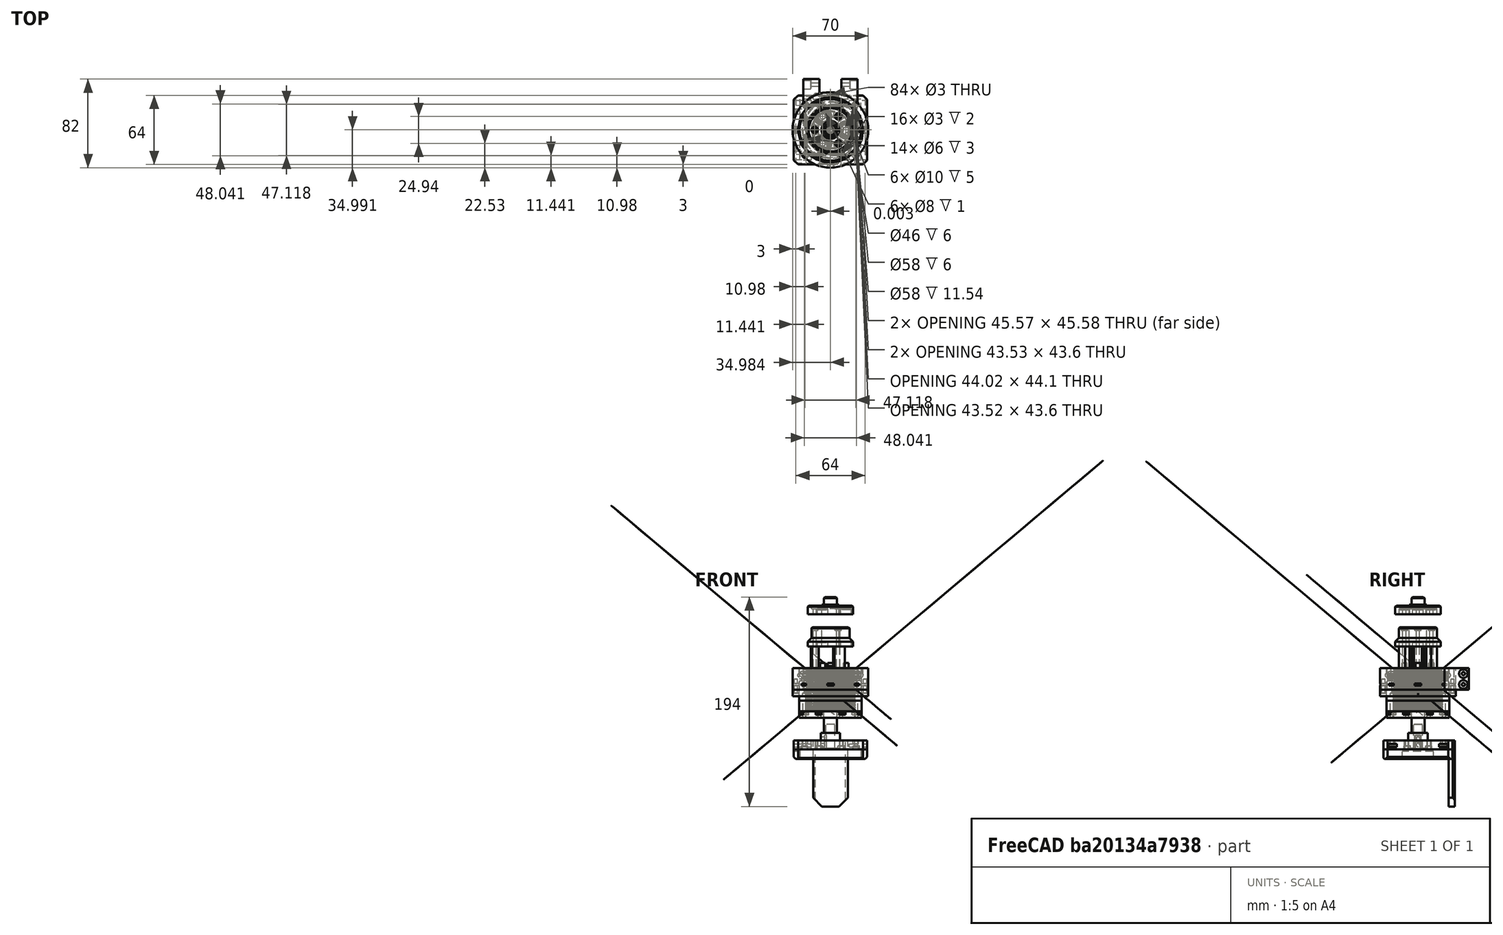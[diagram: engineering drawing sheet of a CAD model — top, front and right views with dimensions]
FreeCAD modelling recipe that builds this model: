
FCSTD DOCUMENT  (FreeCAD 0.19R24276 (Git))
Label: G-midi_gearbox_049
License: All rights reserved
LicenseURL: http://en.wikipedia.org/wiki/All_rights_reserved
objects: Part::Cylinder×393, Part::Cut×179, Part::Compound×131, Part::Box×129, Part::FeaturePython×71, Mesh::Feature×26, Part::Chamfer×22, Part::Torus×9
note: 934 computed .brp shape members not serialized (recipe doc carries the construction recipe); baked Part::Feature solids carry a one-line shape summary decoded from their .brp

FEATURE [Part::FeaturePython] wormgear031  # WARN: FeaturePython — macro-defined, semantics opaque (R4)
  AttacherType = Attacher::AttachEngine3D
  Placement = pos=(14.4,0,-10) rot=(0,0,1;0.991347rad)
  beta = 34.439
  clearance = 0.25
  diameter = 14
  head = 0.5
  height = 10
  module = 0.8
  pressure_angle = 20
  reverse_pitch = false
  teeth = 12
  version = 0.0.3
FEATURE [Part::FeaturePython] wormgear025  # WARN: FeaturePython — macro-defined, semantics opaque (R4)
  AttacherType = Attacher::AttachEngine3D
  Placement = pos=(14.4,0,0) rot=(0,0,1;0.977384rad)
  beta = 34.439
  clearance = 0.25
  diameter = 14
  head = 0.5
  height = 10
  module = 0.8
  pressure_angle = 20
  reverse_pitch = true
  teeth = 12
  version = 0.0.3
FEATURE [Part::FeaturePython] wormgear033  # WARN: FeaturePython — macro-defined, semantics opaque (R4)
  AttacherType = Attacher::AttachEngine3D
  Placement = pos=(14.4,0,10) rot=(0,0,1;0.977384rad)
  beta = 38.6598
  clearance = 0.25
  diameter = 12
  head = 0.5
  height = 10
  module = 0.8
  pressure_angle = 20
  reverse_pitch = false
  teeth = 12
  version = 0.0.3
FEATURE [Part::FeaturePython] wormgear032  # WARN: FeaturePython — macro-defined, semantics opaque (R4)
  AttacherType = Attacher::AttachEngine3D
  Placement = pos=(14.4,0,20) rot=(0,0,1;0.968658rad)
  beta = 38.6598
  clearance = 0.25
  diameter = 12
  head = 0.5
  height = 10
  module = 0.8
  pressure_angle = 20
  reverse_pitch = true
  teeth = 12
  version = 0.0.3
FEATURE [Part::Cylinder] Cylinder017  label="Válec017"
  Angle = 360
  AttacherType = Attacher::AttachEngine3D
  Height = 60
  Placement = pos=(14.4,0,-20) rot=(0,0,1;0rad)
  Radius = 2.65
FEATURE [Part::Cut] Cut317
  Base = -> wormgear031
  Tool = -> Cylinder017
FEATURE [Part::Cylinder] Cylinder025  label="Válec025"
  Angle = 360
  AttacherType = Attacher::AttachEngine3D
  Height = 5
  Placement = pos=(14.4,0,30) rot=(0,0,1;0rad)
  Radius = 2.45
FEATURE [Part::Cylinder] Cylinder016  label="Válec016"
  Angle = 360
  AttacherType = Attacher::AttachEngine3D
  Height = 60
  Placement = pos=(14.4,0,-20) rot=(0,0,1;0rad)
  Radius = 2.65
FEATURE [Part::Cut] Cut314
  Base = -> wormgear025
  Tool = -> Cylinder016
FEATURE [Part::Cylinder] Cylinder018  label="Válec018"
  Angle = 360
  AttacherType = Attacher::AttachEngine3D
  Height = 20
  Placement = pos=(14.4,0,-20) rot=(0,0,1;0rad)
  Radius = 2.65
FEATURE [Part::Cut] Cut316
  Base = -> wormgear032
  Tool = -> Cylinder018
FEATURE [Part::Cylinder] Cylinder019  label="Válec019"
  Angle = 360
  AttacherType = Attacher::AttachEngine3D
  Height = 60
  Placement = pos=(14.4,0,40) rot=(0,0,1;0rad)
  Radius = 2.65
FEATURE [Part::Cut] Cut313
  Base = -> wormgear033
  Tool = -> Cylinder019
FEATURE [Part::Compound] Compound539  label="gearovina_midi_vnejskove"
  Links = -> [Cylinder025,Cut313,Cut316,Cut314,Cut317]
FEATURE [Part::FeaturePython] cycloidgear  # WARN: FeaturePython — macro-defined, semantics opaque (R4)
  AttacherType = Attacher::AttachEngine3D
  Placement = pos=(0,0,10) rot=(0,0,1;0rad)
  backlash = 0
  beta = 50
  clearance = 0.25
  double_helix = true
  height = 20
  inner_diameter = 5
  module = 1
  numpoints = 15
  outer_diameter = 5
  teeth = 12
  version = 0.0.3
FEATURE [Part::FeaturePython] wormgear034  # WARN: FeaturePython — macro-defined, semantics opaque (R4)
  AttacherType = Attacher::AttachEngine3D
  Placement = pos=(0,0,10) rot=(0,0,1;0.977384rad)
  beta = 38.6598
  clearance = 0.25
  diameter = 12
  head = 0.5
  height = 10
  module = 0.8
  pressure_angle = 20
  reverse_pitch = false
  teeth = 12
  version = 0.0.3
FEATURE [Part::FeaturePython] cycloidgear001  # WARN: FeaturePython — macro-defined, semantics opaque (R4)
  AttacherType = Attacher::AttachEngine3D
  Placement = pos=(0,0,-10) rot=(0,0,1;0.331613rad)
  backlash = 0
  beta = 50
  clearance = 0.25
  double_helix = true
  height = 20
  inner_diameter = 5
  module = 1.2
  numpoints = 15
  outer_diameter = 5
  teeth = 12
  version = 0.0.3
FEATURE [Part::FeaturePython] wormgear035  # WARN: FeaturePython — macro-defined, semantics opaque (R4)
  AttacherType = Attacher::AttachEngine3D
  Placement = pos=(0,0,0) rot=(0,0,1;0.977384rad)
  beta = 34.439
  clearance = 0.25
  diameter = 14
  head = 0.5
  height = 10
  module = 0.8
  pressure_angle = 20
  reverse_pitch = true
  teeth = 12
  version = 0.0.3
FEATURE [Part::Cylinder] Cylinder026  label="Válec026"
  Angle = 360
  AttacherType = Attacher::AttachEngine3D
  Height = 5
  Placement = pos=(0,0,30) rot=(0,0,1;0rad)
  Radius = 2.45
FEATURE [Part::Cylinder] Cylinder027  label="Válec027"
  Angle = 360
  AttacherType = Attacher::AttachEngine3D
  Height = 60
  Placement = pos=(0,0,-20) rot=(0,0,1;0rad)
  Radius = 2.65
FEATURE [Part::Cylinder] Cylinder028  label="Válec028"
  Angle = 360
  AttacherType = Attacher::AttachEngine3D
  Height = 60
  Placement = pos=(0,0,-20) rot=(0,0,1;0rad)
  Radius = 2.65
FEATURE [Part::Cut] Cut
  Base = -> cycloidgear001
  Tool = -> Cylinder027
FEATURE [Part::Compound] Compound  label="G-midi_outer-gear"
  Links = -> [Cut,Cylinder026,cycloidgear]
FEATURE [Mesh::Feature] Mesh  label="G-midi_outer-gear (Meshed)"
FEATURE [Part::Torus] Torus006  label="Anuloid006"
  Angle1 = -180
  Angle2 = 180
  Angle3 = 360
  AttacherType = Attacher::AttachEngine3D
  Placement = pos=(0,0,22.5) rot=(0,0,1;0rad)
  Radius1 = 27.75
  Radius2 = 2.2
FEATURE [Part::Cylinder] Cylinder864  label="Válec864"
  Angle = 360
  AttacherType = Attacher::AttachEngine3D
  Height = 9
  Placement = pos=(0,0,11) rot=(0,0,1;0rad)
  Radius = 28.5
FEATURE [Part::Cylinder] Cylinder874  label="Válec874"
  Angle = 360
  AttacherType = Attacher::AttachEngine3D
  Height = 10
  Placement = pos=(0,0,20) rot=(0,0,1;0rad)
  Radius = 28.5
FEATURE [Part::Cylinder] Cylinder875  label="Válec875"
  Angle = 360
  AttacherType = Attacher::AttachEngine3D
  Height = 10
  Placement = pos=(28,0,23.5) rot=(0,0,1;0.392699rad)
  Radius = 2.2
FEATURE [Part::Box] Box332  label="Krychle332"
  AttacherType = Attacher::AttachEngine3D
  Height = 2
  Length = 6
  Placement = pos=(-11.1907,19.1773,25) rot=(0,0,1;0.392699rad)
  Width = 7
FEATURE [Part::Box] Box333  label="Krychle333"
  AttacherType = Attacher::AttachEngine3D
  Height = 2
  Length = 6
  Placement = pos=(-21.4734,5.6474,25) rot=(0,0,1;1.1781rad)
  Width = 7
FEATURE [Part::FeaturePython] wormgear046  # WARN: FeaturePython — macro-defined, semantics opaque (R4)
  AttacherType = Attacher::AttachEngine3D
  Placement = pos=(0,0,9) rot=(0,0,1;1.17286rad)
  beta = 29.1676
  clearance = 0.25
  diameter = 43
  head = 0
  height = 12
  module = 0.8
  pressure_angle = 20
  reverse_pitch = false
  teeth = 30
  version = 0.0.3
FEATURE [Part::Cut] Cut352
  Base = -> Cylinder864
  Tool = -> wormgear046
FEATURE [Part::FeaturePython] wormgear049  # WARN: FeaturePython — macro-defined, semantics opaque (R4)
  AttacherType = Attacher::AttachEngine3D
  Placement = pos=(0,0,19) rot=(0,0,1;1.1205rad)
  beta = 29.1676
  clearance = 0.25
  diameter = 43
  head = 0
  height = 12
  module = 0.8
  pressure_angle = 20
  reverse_pitch = true
  teeth = 30
  version = 0.0.3
FEATURE [Part::Cut] Cut362
  Base = -> Cylinder874
  Tool = -> wormgear049
FEATURE [Part::Cut] Cut361
  Base = -> Cut362
  Tool = -> Torus006
FEATURE [Part::Cut] Cut360
  Base = -> Cut361
  Tool = -> Cylinder875
FEATURE [Part::Box] Box335  label="Krychle335"
  AttacherType = Attacher::AttachEngine3D
  Height = 2
  Length = 6
  Placement = pos=(-5.6474,-21.4734,25) rot=(0,0,1;2.74889rad)
  Width = 7
FEATURE [Part::Box] Box339  label="Krychle339"
  AttacherType = Attacher::AttachEngine3D
  Height = 2
  Length = 6
  Placement = pos=(5.6474,21.4734,25) rot=(0,0,-1;0.392699rad)
  Width = 7
FEATURE [Part::Cylinder] Cylinder883  label="Válec883"
  Angle = 360
  AttacherType = Attacher::AttachEngine3D
  Height = 10
  Placement = pos=(23.5589,9.75843,25) rot=(0,0,-1;1.1781rad)
  Radius = 1.5
FEATURE [Part::Cylinder] Cylinder878  label="Válec878"
  Angle = 360
  AttacherType = Attacher::AttachEngine3D
  Height = 10
  Placement = pos=(-23.5589,-9.75843,25) rot=(0,0,1;1.96349rad)
  Radius = 1.5
FEATURE [Part::Cylinder] Cylinder879  label="Válec879"
  Angle = 360
  AttacherType = Attacher::AttachEngine3D
  Height = 10
  Placement = pos=(9.75843,-23.5589,25) rot=(0,0,1;3.53429rad)
  Radius = 1.5
FEATURE [Part::Cylinder] Cylinder880  label="Válec880"
  Angle = 360
  AttacherType = Attacher::AttachEngine3D
  Height = 10
  Placement = pos=(9.75843,23.5589,25) rot=(0,0,-1;0.392699rad)
  Radius = 1.5
FEATURE [Part::Cylinder] Cylinder877  label="Válec877"
  Angle = 360
  AttacherType = Attacher::AttachEngine3D
  Height = 10
  Placement = pos=(-9.75843,23.5589,25) rot=(0,0,1;0.392699rad)
  Radius = 1.5
FEATURE [Part::Cylinder] Cylinder881  label="Válec881"
  Angle = 360
  AttacherType = Attacher::AttachEngine3D
  Height = 10
  Placement = pos=(23.5589,-9.75843,25) rot=(0,0,-1;1.96349rad)
  Radius = 1.5
FEATURE [Part::Box] Box334  label="Krychle334"
  AttacherType = Attacher::AttachEngine3D
  Height = 2
  Length = 6
  Placement = pos=(-19.1773,-11.1907,25) rot=(0,0,1;1.96349rad)
  Width = 7
FEATURE [Part::Cylinder] Cylinder882  label="Válec882"
  Angle = 360
  AttacherType = Attacher::AttachEngine3D
  Height = 10
  Placement = pos=(-9.75843,-23.5589,25) rot=(0,0,1;2.74889rad)
  Radius = 1.5
FEATURE [Part::Box] Box338  label="Krychle338"
  AttacherType = Attacher::AttachEngine3D
  Height = 2
  Length = 6
  Placement = pos=(19.1773,11.1907,25) rot=(0,0,-1;1.1781rad)
  Width = 7
FEATURE [Part::Box] Box337  label="Krychle337"
  AttacherType = Attacher::AttachEngine3D
  Height = 2
  Length = 6
  Placement = pos=(21.4734,-5.6474,25) rot=(0,0,-1;1.96349rad)
  Width = 7
FEATURE [Part::Box] Box336  label="Krychle336"
  AttacherType = Attacher::AttachEngine3D
  Height = 2
  Length = 6
  Placement = pos=(11.1907,-19.1773,25) rot=(0,0,1;3.53429rad)
  Width = 7
FEATURE [Part::Compound] Compound561
  Links = -> [Box332,Box333,Box334,Box335,Box336,Box337,Box338,Box339]
FEATURE [Part::Cut] Cut363
  Base = -> Cut360
  Tool = -> Compound561
FEATURE [Part::Cylinder] Cylinder876  label="Válec876"
  Angle = 360
  AttacherType = Attacher::AttachEngine3D
  Height = 10
  Placement = pos=(-23.5589,9.75843,25) rot=(0,0,1;1.1781rad)
  Radius = 1.5
FEATURE [Part::Compound] Compound562
  Links = -> [Cylinder877,Cylinder876,Cylinder878,Cylinder882,Cylinder879,Cylinder881,Cylinder883,Cylinder880]
FEATURE [Part::Cut] Cut364
  Base = -> Cut363
  Tool = -> Compound562
FEATURE [Part::Compound] Compound563  label="gearovina_midi_rybovina"
  Links = -> [Cut364,Cut352]
FEATURE [Part::FeaturePython] wormgear050  # WARN: FeaturePython — macro-defined, semantics opaque (R4)
  AttacherType = Attacher::AttachEngine3D
  Placement = pos=(0,0,19) rot=(0,0,1;1.1205rad)
  beta = 29.1676
  clearance = 0.25
  diameter = 43
  head = 0
  height = 12
  module = 0.8
  pressure_angle = 20
  reverse_pitch = true
  teeth = 30
  version = 0.0.3
FEATURE [Part::FeaturePython] cycloidgear002  # WARN: FeaturePython — macro-defined, semantics opaque (R4)
  AttacherType = Attacher::AttachEngine3D
  Placement = pos=(0,0,-1) rot=(0,0,1;0rad)
  backlash = 0
  beta = 50
  clearance = 0.25
  double_helix = true
  height = 22
  inner_diameter = 5
  module = 1.35
  numpoints = 15
  outer_diameter = 5
  teeth = 33
  version = 0.0.3
FEATURE [Part::Cylinder] Cylinder884  label="Válec884"
  Angle = 360
  AttacherType = Attacher::AttachEngine3D
  Height = 20
  Radius = 29
FEATURE [Part::Cut] Cut365  label="G-midi_exp-ring-cyclo"
  Base = -> Cylinder884
  Tool = -> cycloidgear002
FEATURE [Part::FeaturePython] cycloidgear003  # WARN: FeaturePython — macro-defined, semantics opaque (R4)
  AttacherType = Attacher::AttachEngine3D
  Placement = pos=(0,0,10) rot=(0,0,1;0.418879rad)
  backlash = 0
  beta = 50
  clearance = 0
  double_helix = true
  height = 20
  inner_diameter = 3
  module = 1.25
  numpoints = 15
  outer_diameter = 5
  teeth = 9
  version = 0.0.3
FEATURE [Part::FeaturePython] cycloidgear004  # WARN: FeaturePython — macro-defined, semantics opaque (R4)
  AttacherType = Attacher::AttachEngine3D
  Placement = pos=(0,0,-10) rot=(0,0,-1;0.453786rad)
  backlash = 0
  beta = 50
  clearance = 0.25
  double_helix = true
  height = 20
  inner_diameter = 5
  module = 1.32
  numpoints = 15
  outer_diameter = 5
  teeth = 12
  version = 0.0.3
FEATURE [Part::Cylinder] Cylinder885  label="Válec885"
  Angle = 360
  AttacherType = Attacher::AttachEngine3D
  Height = 60
  Placement = pos=(0,0,-20) rot=(0,0,1;0rad)
  Radius = 2.65
FEATURE [Part::Cut] Cut366
  Base = -> cycloidgear004
  Tool = -> Cylinder885
FEATURE [Part::Cylinder] Cylinder886  label="Válec886"
  Angle = 360
  AttacherType = Attacher::AttachEngine3D
  Height = 5
  Placement = pos=(0,0,30) rot=(0,0,1;0rad)
  Radius = 2.45
FEATURE [Part::Compound] Compound564  label="G-midi_outer-gear001-cyclo"
  Links = -> [Cut366,Cylinder886,cycloidgear003]
  Placement = pos=(-14,0,10) rot=(0,0,-1;0.331613rad)
FEATURE [Part::Cylinder] Cylinder887  label="Válec887"
  Angle = 360
  AttacherType = Attacher::AttachEngine3D
  Height = 20
  Radius = 26
FEATURE [Part::FeaturePython] involutegear  # WARN: FeaturePython — macro-defined, semantics opaque (R4)
  AttacherType = Attacher::AttachEngine3D
  Placement = pos=(0,0,-1) rot=(0,0,1;0rad)
  backlash = 0
  beta = 50
  clearance = 0.25
  da = 45.6
  df = 40.2
  double_helix = true
  dw = 43.2
  head = 0
  height = 22
  module = 1.2
  numpoints = 6
  pressure_angle = 20
  properties_from_tool = false
  reversed_backlash = false
  shift = 0
  simple = false
  teeth = 36
  transverse_pitch = 3.76991
  undercut = false
  version = 0.0.3
FEATURE [Part::Cut] Cut367  label="G-midi_exp-ring-invo"
  Base = -> Cylinder887
  Tool = -> involutegear
FEATURE [Part::Cylinder] Cylinder119  label="Válec119"
  Angle = 360
  AttacherType = Attacher::AttachEngine3D
  Height = 3
  Placement = pos=(0,32,4) rot=(0,0,1;0rad)
  Radius = 3
FEATURE [Part::Cylinder] Cylinder109  label="Válec109"
  Angle = 360
  AttacherType = Attacher::AttachEngine3D
  Height = 10
  Radius = 29
FEATURE [Part::Cylinder] Cylinder120  label="Válec120"
  Angle = 360
  AttacherType = Attacher::AttachEngine3D
  Height = 3
  Placement = pos=(-22.6274,22.6274,4) rot=(0,0,1;0.785398rad)
  Radius = 3
FEATURE [Part::Cylinder] Cylinder110  label="Válec110"
  Angle = 360
  AttacherType = Attacher::AttachEngine3D
  Height = 10
  Radius = 29
FEATURE [Part::Cylinder] Cylinder121  label="Válec121"
  Angle = 360
  AttacherType = Attacher::AttachEngine3D
  Height = 3
  Placement = pos=(-32,0,4) rot=(0,0,1;1.5708rad)
  Radius = 3
FEATURE [Part::FeaturePython] wormgear041  # WARN: FeaturePython — macro-defined, semantics opaque (R4)
  AttacherType = Attacher::AttachEngine3D
  Placement = pos=(0,0,0) rot=(0,0,1;1.13796rad)
  beta = 30.9638
  clearance = 0.25
  diameter = 44
  head = 0
  height = 12
  module = 0.8
  pressure_angle = 20
  reverse_pitch = false
  teeth = 33
  version = 0.0.3
FEATURE [Part::Cut] Cut038
  Base = -> Cylinder110
  Placement = pos=(0,0,-10) rot=(0,0,1;0rad)
  Tool = -> wormgear041
FEATURE [Part::FeaturePython] wormgear042  # WARN: FeaturePython — macro-defined, semantics opaque (R4)
  AttacherType = Attacher::AttachEngine3D
  Placement = pos=(0,0,0) rot=(0,0,1;1.13446rad)
  beta = 30.9638
  clearance = 0.25
  diameter = 44
  head = 0
  height = 12
  module = 0.8
  pressure_angle = 20
  reverse_pitch = true
  teeth = 33
  version = 0.0.3
FEATURE [Part::Cut] Cut039
  Base = -> Cylinder109
  Tool = -> wormgear042
FEATURE [Part::Compound] Compound038  label="superokruh"
  Links = -> [Cut038,Cut039]
FEATURE [Part::FeaturePython] Tube008  # WARN: FeaturePython — macro-defined, semantics opaque (R4)
  AttacherType = Attacher::AttachEngine3D
  Height = 6
  InnerRadius = 29
  OuterRadius = 35
  Placement = pos=(0,0,4) rot=(0,0,1;0rad)
FEATURE [Part::Cylinder] Cylinder131  label="Válec131"
  Angle = 360
  AttacherType = Attacher::AttachEngine3D
  Height = 15
  Placement = pos=(1e-14,-32,0) rot=(0,0,1;3.14159rad)
  Radius = 1.5
FEATURE [Part::Cylinder] Cylinder123  label="Válec123"
  Angle = 360
  AttacherType = Attacher::AttachEngine3D
  Height = 3
  Placement = pos=(1e-14,-32,4) rot=(0,0,1;3.14159rad)
  Radius = 3
FEATURE [Part::Cylinder] Cylinder122  label="Válec122"
  Angle = 360
  AttacherType = Attacher::AttachEngine3D
  Height = 3
  Placement = pos=(-22.6274,-22.6274,4) rot=(0,0,1;2.35619rad)
  Radius = 3
FEATURE [Part::Cylinder] Cylinder132  label="Válec132"
  Angle = 360
  AttacherType = Attacher::AttachEngine3D
  Height = 15
  Placement = pos=(22.6274,-22.6274,0) rot=(0,0,1;3.92699rad)
  Radius = 1.5
FEATURE [Part::Cylinder] Cylinder129  label="Válec129"
  Angle = 360
  AttacherType = Attacher::AttachEngine3D
  Height = 15
  Placement = pos=(-32,0,0) rot=(0,0,1;1.5708rad)
  Radius = 1.5
FEATURE [Part::Cylinder] Cylinder127  label="Válec127"
  Angle = 360
  AttacherType = Attacher::AttachEngine3D
  Height = 15
  Placement = pos=(0,32,0) rot=(0,0,1;0rad)
  Radius = 1.5
FEATURE [Part::Cylinder] Cylinder124  label="Válec124"
  Angle = 360
  AttacherType = Attacher::AttachEngine3D
  Height = 3
  Placement = pos=(22.6274,-22.6274,4) rot=(0,0,1;3.92699rad)
  Radius = 3
FEATURE [Part::Cylinder] Cylinder133  label="Válec133"
  Angle = 360
  AttacherType = Attacher::AttachEngine3D
  Height = 15
  Placement = pos=(32,1.1e-14,0) rot=(0,0,-1;1.5708rad)
  Radius = 1.5
FEATURE [Part::Cylinder] Cylinder126  label="Válec126"
  Angle = 360
  AttacherType = Attacher::AttachEngine3D
  Height = 3
  Placement = pos=(22.6274,22.6274,4) rot=(0,0,-1;0.785398rad)
  Radius = 3
FEATURE [Part::Cylinder] Cylinder125  label="Válec125"
  Angle = 360
  AttacherType = Attacher::AttachEngine3D
  Height = 3
  Placement = pos=(32,1.1e-14,4) rot=(0,0,-1;1.5708rad)
  Radius = 3
FEATURE [Part::Compound] Compound040
  Links = -> [Cylinder119,Cylinder120,Cylinder121,Cylinder122,Cylinder123,Cylinder124,Cylinder125,Cylinder126]
FEATURE [Part::Cut] Cut041
  Base = -> Tube008
  Tool = -> Compound040
FEATURE [Part::Cylinder] Cylinder134  label="Válec134"
  Angle = 360
  AttacherType = Attacher::AttachEngine3D
  Height = 15
  Placement = pos=(22.6274,22.6274,0) rot=(0,0,-1;0.785398rad)
  Radius = 1.5
FEATURE [Part::Cylinder] Cylinder128  label="Válec128"
  Angle = 360
  AttacherType = Attacher::AttachEngine3D
  Height = 15
  Placement = pos=(-22.6274,22.6274,0) rot=(0,0,1;0.785398rad)
  Radius = 1.5
FEATURE [Part::Cylinder] Cylinder130  label="Válec130"
  Angle = 360
  AttacherType = Attacher::AttachEngine3D
  Height = 15
  Placement = pos=(-22.6274,-22.6274,0) rot=(0,0,1;2.35619rad)
  Radius = 1.5
FEATURE [Part::Compound] Compound041
  Links = -> [Cylinder127,Cylinder128,Cylinder129,Cylinder130,Cylinder131,Cylinder132,Cylinder133,Cylinder134]
FEATURE [Part::Cut] Cut042
  Base = -> Cut041
  Tool = -> Compound041
FEATURE [Part::Cylinder] Cylinder139  label="Válec139"
  Angle = 360
  AttacherType = Attacher::AttachEngine3D
  Height = 20
  Placement = pos=(-24,38,-11) rot=(0,1,0;1.5708rad)
  Radius = 1.5
FEATURE [Part::Cylinder] Cylinder141  label="Válec141"
  Angle = 360
  AttacherType = Attacher::AttachEngine3D
  Height = 20
  Placement = pos=(-34,38,-11) rot=(0,1,0;1.5708rad)
  Radius = 4
FEATURE [Part::Cylinder] Cylinder142  label="Válec142"
  Angle = 360
  AttacherType = Attacher::AttachEngine3D
  Height = 20
  Placement = pos=(4,38,5) rot=(0,1,0;1.5708rad)
  Radius = 1.5
FEATURE [Part::Cylinder] Cylinder144  label="Válec144"
  Angle = 360
  AttacherType = Attacher::AttachEngine3D
  Height = 20
  Placement = pos=(14,38,5) rot=(0,1,0;1.5708rad)
  Radius = 4
FEATURE [Part::Cylinder] Cylinder145  label="Válec145"
  Angle = 360
  AttacherType = Attacher::AttachEngine3D
  Height = 20
  Placement = pos=(14,38,-11) rot=(0,1,0;1.5708rad)
  Radius = 4
FEATURE [Part::Compound] Compound044
  Links = -> [Cylinder144,Cylinder145]
FEATURE [Part::Box] Box057  label="Krychle057"
  AttacherType = Attacher::AttachEngine3D
  Height = 26
  Length = 16
  Placement = pos=(-8,20,-16) rot=(0,0,1;0rad)
  Width = 25
FEATURE [Part::Cylinder] Cylinder138  label="Válec138"
  Angle = 360
  AttacherType = Attacher::AttachEngine3D
  Height = 20
  Placement = pos=(-24,38,5) rot=(0,1,0;1.5708rad)
  Radius = 1.5
FEATURE [Part::Compound] Compound043
  Links = -> [Cylinder138,Cylinder139]
FEATURE [Part::Box] Box055  label="Krychle055"
  AttacherType = Attacher::AttachEngine3D
  Height = 26
  Length = 40
  Placement = pos=(-20,15,-16) rot=(0,0,1;0rad)
  Width = 30
FEATURE [Part::Cylinder] Cylinder140  label="Válec140"
  Angle = 360
  AttacherType = Attacher::AttachEngine3D
  Height = 20
  Placement = pos=(-34,38,5) rot=(0,1,0;1.5708rad)
  Radius = 4
FEATURE [Part::Compound] Compound042
  Links = -> [Cylinder140,Cylinder141]
FEATURE [Part::Cylinder] Cylinder143  label="Válec143"
  Angle = 360
  AttacherType = Attacher::AttachEngine3D
  Height = 20
  Placement = pos=(4,38,-11) rot=(0,1,0;1.5708rad)
  Radius = 1.5
FEATURE [Part::Compound] Compound045
  Links = -> [Cylinder142,Cylinder143]
FEATURE [Part::Cylinder] Cylinder136  label="Válec136"
  Angle = 360
  AttacherType = Attacher::AttachEngine3D
  Height = 26
  Placement = pos=(0,0,-16) rot=(0,0,1;0rad)
  Radius = 29
FEATURE [Part::Cut] Cut045
  Base = -> Box055
  Tool = -> Cylinder136
FEATURE [Part::Cut] Cut047
  Base = -> Cut045
  Tool = -> Box057
FEATURE [Part::Cut] Cut048
  Base = -> Cut047
  Tool = -> Compound042
FEATURE [Part::Cut] Cut049
  Base = -> Cut048
  Tool = -> Compound043
FEATURE [Part::Cut] Cut050
  Base = -> Cut049
  Tool = -> Compound044
FEATURE [Part::Cut] Cut051
  Base = -> Cut050
  Tool = -> Compound045
FEATURE [Part::Compound] Compound046  label="gearovina_midi_superokruh1"
  Links = -> [Cut051,Cut042,Compound038]
FEATURE [Part::Cylinder] Cylinder111  label="Válec111"
  Angle = 360
  AttacherType = Attacher::AttachEngine3D
  Height = 15
  Placement = pos=(0,26,-20) rot=(0,0,1;0rad)
  Radius = 1.5
FEATURE [Part::Cylinder] Cylinder112  label="Válec112"
  Angle = 360
  AttacherType = Attacher::AttachEngine3D
  Height = 15
  Placement = pos=(-18.3848,18.3848,-20) rot=(0,0,1;0.785398rad)
  Radius = 1.5
FEATURE [Part::FeaturePython] Tube007  # WARN: FeaturePython — macro-defined, semantics opaque (R4)
  AttacherType = Attacher::AttachEngine3D
  Height = 6
  InnerRadius = 23
  OuterRadius = 29
  Placement = pos=(0,0,-16) rot=(0,0,1;0rad)
FEATURE [Part::Box] Box047  label="Krychle047"
  AttacherType = Attacher::AttachEngine3D
  Height = 2
  Length = 6
  Placement = pos=(-3,23,-13) rot=(0,0,1;0rad)
  Width = 6
FEATURE [Part::Cylinder] Cylinder114  label="Válec114"
  Angle = 360
  AttacherType = Attacher::AttachEngine3D
  Height = 15
  Placement = pos=(-18.3848,-18.3848,-20) rot=(0,0,1;2.35619rad)
  Radius = 1.5
FEATURE [Part::Cylinder] Cylinder113  label="Válec113"
  Angle = 360
  AttacherType = Attacher::AttachEngine3D
  Height = 15
  Placement = pos=(-26,-4e-15,-20) rot=(0,0,1;1.5708rad)
  Radius = 1.5
FEATURE [Part::Cylinder] Cylinder115  label="Válec115"
  Angle = 360
  AttacherType = Attacher::AttachEngine3D
  Height = 15
  Placement = pos=(1.1e-14,-26,-20) rot=(0,0,1;3.14159rad)
  Radius = 1.5
FEATURE [Part::Cylinder] Cylinder116  label="Válec116"
  Angle = 360
  AttacherType = Attacher::AttachEngine3D
  Height = 15
  Placement = pos=(18.3848,-18.3848,-20) rot=(0,0,1;3.92699rad)
  Radius = 1.5
FEATURE [Part::Cylinder] Cylinder118  label="Válec118"
  Angle = 360
  AttacherType = Attacher::AttachEngine3D
  Height = 15
  Placement = pos=(18.3848,18.3848,-20) rot=(0,0,-1;0.785398rad)
  Radius = 1.5
FEATURE [Part::Cylinder] Cylinder117  label="Válec117"
  Angle = 360
  AttacherType = Attacher::AttachEngine3D
  Height = 15
  Placement = pos=(26,1e-14,-20) rot=(0,0,-1;1.5708rad)
  Radius = 1.5
FEATURE [Part::Compound] Compound565
  Links = -> [Cylinder111,Cylinder112,Cylinder113,Cylinder114,Cylinder115,Cylinder116,Cylinder117,Cylinder118]
  Placement = pos=(0,0,0) rot=(0,0,1;0.392699rad)
FEATURE [Part::Cut] Cut368
  Base = -> Tube007
  Tool = -> Compound565
FEATURE [Part::Box] Box048  label="Krychle048"
  AttacherType = Attacher::AttachEngine3D
  Height = 2
  Length = 6
  Placement = pos=(-18.3848,14.1421,-13) rot=(0,0,1;0.785398rad)
  Width = 6
FEATURE [Part::Box] Box050  label="Krychle050"
  AttacherType = Attacher::AttachEngine3D
  Height = 2
  Length = 6
  Placement = pos=(-14.1421,-18.3848,-13) rot=(0,0,1;2.35619rad)
  Width = 6
FEATURE [Part::Box] Box052  label="Krychle052"
  AttacherType = Attacher::AttachEngine3D
  Height = 2
  Length = 6
  Placement = pos=(18.3848,-14.1421,-13) rot=(0,0,1;3.92699rad)
  Width = 6
FEATURE [Part::Box] Box054  label="Krychle054"
  AttacherType = Attacher::AttachEngine3D
  Height = 2
  Length = 6
  Placement = pos=(14.1421,18.3848,-13) rot=(0,0,-1;0.785398rad)
  Width = 6
FEATURE [Part::Box] Box049  label="Krychle049"
  AttacherType = Attacher::AttachEngine3D
  Height = 2
  Length = 6
  Placement = pos=(-23,-3,-13) rot=(0,0,1;1.5708rad)
  Width = 6
FEATURE [Part::Box] Box051  label="Krychle051"
  AttacherType = Attacher::AttachEngine3D
  Height = 2
  Length = 6
  Placement = pos=(3,-23,-13) rot=(0,0,1;3.14159rad)
  Width = 6
FEATURE [Part::Box] Box053  label="Krychle053"
  AttacherType = Attacher::AttachEngine3D
  Height = 2
  Length = 6
  Placement = pos=(23,3,-13) rot=(0,0,-1;1.5708rad)
  Width = 6
FEATURE [Part::Compound] Compound039
  Links = -> [Box048,Box049,Box050,Box051,Box052,Box053,Box054,Box047]
  Placement = pos=(0,0,0) rot=(0,0,1;0.392699rad)
FEATURE [Part::Cut] Cut311
  Base = -> Cut368
  Tool = -> Compound039
FEATURE [Part::Compound] Compound538  label="gearovina_midi_superokruh"
  Links = -> [Compound046,Cut311]
FEATURE [Part::Cylinder] Cylinder889  label="Válec889"
  Angle = 360
  AttacherType = Attacher::AttachEngine3D
  Height = 15
  Placement = pos=(1e-14,-32,0) rot=(0,0,1;3.14159rad)
  Radius = 1.5
FEATURE [Part::Cylinder] Cylinder890  label="Válec890"
  Angle = 360
  AttacherType = Attacher::AttachEngine3D
  Height = 15
  Placement = pos=(22.6274,-22.6274,0) rot=(0,0,1;3.92699rad)
  Radius = 1.5
FEATURE [Part::Cylinder] Cylinder891  label="Válec891"
  Angle = 360
  AttacherType = Attacher::AttachEngine3D
  Height = 3
  Placement = pos=(-22.6274,-22.6274,4) rot=(0,0,1;2.35619rad)
  Radius = 3
FEATURE [Part::Cylinder] Cylinder892  label="Válec892"
  Angle = 360
  AttacherType = Attacher::AttachEngine3D
  Height = 15
  Placement = pos=(0,32,0) rot=(0,0,1;0rad)
  Radius = 1.5
FEATURE [Part::Cylinder] Cylinder893  label="Válec893"
  Angle = 360
  AttacherType = Attacher::AttachEngine3D
  Height = 3
  Placement = pos=(0,32,4) rot=(0,0,1;0rad)
  Radius = 3
FEATURE [Part::Cylinder] Cylinder894  label="Válec894"
  Angle = 360
  AttacherType = Attacher::AttachEngine3D
  Height = 3
  Placement = pos=(-22.6274,22.6274,4) rot=(0,0,1;0.785398rad)
  Radius = 3
FEATURE [Part::Cylinder] Cylinder895  label="Válec895"
  Angle = 360
  AttacherType = Attacher::AttachEngine3D
  Height = 3
  Placement = pos=(-32,0,4) rot=(0,0,1;1.5708rad)
  Radius = 3
FEATURE [Part::Cylinder] Cylinder896  label="Válec896"
  Angle = 360
  AttacherType = Attacher::AttachEngine3D
  Height = 3
  Placement = pos=(1e-14,-32,4) rot=(0,0,1;3.14159rad)
  Radius = 3
FEATURE [Part::Cylinder] Cylinder897  label="Válec897"
  Angle = 360
  AttacherType = Attacher::AttachEngine3D
  Height = 15
  Placement = pos=(-32,0,0) rot=(0,0,1;1.5708rad)
  Radius = 1.5
FEATURE [Part::Cylinder] Cylinder898  label="Válec898"
  Angle = 360
  AttacherType = Attacher::AttachEngine3D
  Height = 3
  Placement = pos=(22.6274,-22.6274,4) rot=(0,0,1;3.92699rad)
  Radius = 3
FEATURE [Part::Cylinder] Cylinder899  label="Válec899"
  Angle = 360
  AttacherType = Attacher::AttachEngine3D
  Height = 3
  Placement = pos=(22.6274,22.6274,4) rot=(0,0,-1;0.785398rad)
  Radius = 3
FEATURE [Part::Cylinder] Cylinder900  label="Válec900"
  Angle = 360
  AttacherType = Attacher::AttachEngine3D
  Height = 15
  Placement = pos=(-22.6274,22.6274,0) rot=(0,0,1;0.785398rad)
  Radius = 1.5
FEATURE [Part::Cylinder] Cylinder901  label="Válec901"
  Angle = 360
  AttacherType = Attacher::AttachEngine3D
  Height = 15
  Placement = pos=(22.6274,22.6274,0) rot=(0,0,-1;0.785398rad)
  Radius = 1.5
FEATURE [Part::Cylinder] Cylinder902  label="Válec902"
  Angle = 360
  AttacherType = Attacher::AttachEngine3D
  Height = 15
  Placement = pos=(32,1.1e-14,0) rot=(0,0,-1;1.5708rad)
  Radius = 1.5
FEATURE [Part::Cylinder] Cylinder903  label="Válec903"
  Angle = 360
  AttacherType = Attacher::AttachEngine3D
  Height = 3
  Placement = pos=(32,1.1e-14,4) rot=(0,0,-1;1.5708rad)
  Radius = 3
FEATURE [Part::Cylinder] Cylinder904  label="Válec904"
  Angle = 360
  AttacherType = Attacher::AttachEngine3D
  Height = 15
  Placement = pos=(-22.6274,-22.6274,0) rot=(0,0,1;2.35619rad)
  Radius = 1.5
FEATURE [Part::FeaturePython] Tube009  # WARN: FeaturePython — macro-defined, semantics opaque (R4)
  AttacherType = Attacher::AttachEngine3D
  Height = 6
  InnerRadius = 29
  OuterRadius = 35
  Placement = pos=(0,0,4) rot=(0,0,1;0rad)
FEATURE [Part::Compound] Compound566
  Links = -> [Cylinder893,Cylinder894,Cylinder895,Cylinder891,Cylinder896,Cylinder898,Cylinder903,Cylinder899]
FEATURE [Part::Compound] Compound567
  Links = -> [Cylinder892,Cylinder900,Cylinder897,Cylinder904,Cylinder889,Cylinder890,Cylinder902,Cylinder901]
FEATURE [Part::Cut] Cut371
  Base = -> Tube009
  Tool = -> Compound566
FEATURE [Part::Cut] Cut370
  Base = -> Cut371
  Placement = pos=(0,0,10) rot=(0,0,1;0rad)
  Tool = -> Compound567
FEATURE [Part::FeaturePython] Tube010  # WARN: FeaturePython — macro-defined, semantics opaque (R4)
  AttacherType = Attacher::AttachEngine3D
  Height = 6
  InnerRadius = 23
  OuterRadius = 29
  Placement = pos=(0,0,-16) rot=(0,0,1;0rad)
FEATURE [Part::Cylinder] Cylinder905  label="Válec905"
  Angle = 360
  AttacherType = Attacher::AttachEngine3D
  Height = 15
  Placement = pos=(-18.3848,-18.3848,-20) rot=(0,0,1;2.35619rad)
  Radius = 1.5
FEATURE [Part::Cylinder] Cylinder906  label="Válec906"
  Angle = 360
  AttacherType = Attacher::AttachEngine3D
  Height = 15
  Placement = pos=(-26,-4e-15,-20) rot=(0,0,1;1.5708rad)
  Radius = 1.5
FEATURE [Part::Box] Box340  label="Krychle340"
  AttacherType = Attacher::AttachEngine3D
  Height = 2
  Length = 6
  Placement = pos=(-3,23,-13) rot=(0,0,1;0rad)
  Width = 6
FEATURE [Part::Box] Box341  label="Krychle341"
  AttacherType = Attacher::AttachEngine3D
  Height = 2
  Length = 6
  Placement = pos=(-14.1421,-18.3848,-13) rot=(0,0,1;2.35619rad)
  Width = 6
FEATURE [Part::Cylinder] Cylinder907  label="Válec907"
  Angle = 360
  AttacherType = Attacher::AttachEngine3D
  Height = 15
  Placement = pos=(-18.3848,18.3848,-20) rot=(0,0,1;0.785398rad)
  Radius = 1.5
FEATURE [Part::Cylinder] Cylinder908  label="Válec908"
  Angle = 360
  AttacherType = Attacher::AttachEngine3D
  Height = 15
  Placement = pos=(18.3848,18.3848,-20) rot=(0,0,-1;0.785398rad)
  Radius = 1.5
FEATURE [Part::Cylinder] Cylinder909  label="Válec909"
  Angle = 360
  AttacherType = Attacher::AttachEngine3D
  Height = 15
  Placement = pos=(0,26,-20) rot=(0,0,1;0rad)
  Radius = 1.5
FEATURE [Part::Cylinder] Cylinder910  label="Válec910"
  Angle = 360
  AttacherType = Attacher::AttachEngine3D
  Height = 15
  Placement = pos=(1.1e-14,-26,-20) rot=(0,0,1;3.14159rad)
  Radius = 1.5
FEATURE [Part::Cylinder] Cylinder911  label="Válec911"
  Angle = 360
  AttacherType = Attacher::AttachEngine3D
  Height = 15
  Placement = pos=(18.3848,-18.3848,-20) rot=(0,0,1;3.92699rad)
  Radius = 1.5
FEATURE [Part::Cylinder] Cylinder912  label="Válec912"
  Angle = 360
  AttacherType = Attacher::AttachEngine3D
  Height = 15
  Placement = pos=(26,1e-14,-20) rot=(0,0,-1;1.5708rad)
  Radius = 1.5
FEATURE [Part::Compound] Compound568
  Links = -> [Cylinder909,Cylinder907,Cylinder906,Cylinder905,Cylinder910,Cylinder911,Cylinder912,Cylinder908]
  Placement = pos=(0,0,0) rot=(0,0,1;0.392699rad)
FEATURE [Part::Cut] Cut372
  Base = -> Tube010
  Tool = -> Compound568
FEATURE [Part::Box] Box342  label="Krychle342"
  AttacherType = Attacher::AttachEngine3D
  Height = 2
  Length = 6
  Placement = pos=(-18.3848,14.1421,-13) rot=(0,0,1;0.785398rad)
  Width = 6
FEATURE [Part::Box] Box343  label="Krychle343"
  AttacherType = Attacher::AttachEngine3D
  Height = 2
  Length = 6
  Placement = pos=(18.3848,-14.1421,-13) rot=(0,0,1;3.92699rad)
  Width = 6
FEATURE [Part::Box] Box344  label="Krychle344"
  AttacherType = Attacher::AttachEngine3D
  Height = 2
  Length = 6
  Placement = pos=(14.1421,18.3848,-13) rot=(0,0,-1;0.785398rad)
  Width = 6
FEATURE [Part::Box] Box345  label="Krychle345"
  AttacherType = Attacher::AttachEngine3D
  Height = 2
  Length = 6
  Placement = pos=(-23,-3,-13) rot=(0,0,1;1.5708rad)
  Width = 6
FEATURE [Part::Box] Box346  label="Krychle346"
  AttacherType = Attacher::AttachEngine3D
  Height = 2
  Length = 6
  Placement = pos=(3,-23,-13) rot=(0,0,1;3.14159rad)
  Width = 6
FEATURE [Part::Box] Box347  label="Krychle347"
  AttacherType = Attacher::AttachEngine3D
  Height = 2
  Length = 6
  Placement = pos=(23,3,-13) rot=(0,0,-1;1.5708rad)
  Width = 6
FEATURE [Part::Compound] Compound569
  Links = -> [Box342,Box345,Box341,Box346,Box343,Box347,Box344,Box340]
  Placement = pos=(0,0,0) rot=(0,0,1;0.392699rad)
FEATURE [Part::Cut] Cut373
  Base = -> Cut372
  Placement = pos=(0,0,10) rot=(0,0,1;0rad)
  Tool = -> Compound569
FEATURE [Part::Cylinder] Cylinder913  label="Válec913"
  Angle = 360
  AttacherType = Attacher::AttachEngine3D
  Height = 20
  Radius = 29
FEATURE [Part::FeaturePython] cycloidgear006  # WARN: FeaturePython — macro-defined, semantics opaque (R4)
  AttacherType = Attacher::AttachEngine3D
  Placement = pos=(0,0,-1) rot=(0,0,1;0rad)
  backlash = 0
  beta = 50
  clearance = 0.25
  double_helix = true
  height = 22
  inner_diameter = 5
  module = 1.32
  numpoints = 15
  outer_diameter = 5
  teeth = 33
  version = 0.0.3
FEATURE [Part::Cut] Cut374  label="G-midi_exp-ring-cyclo002"
  Base = -> Cylinder913
  Tool = -> cycloidgear006
FEATURE [Part::Compound] Compound570  label="G-midi_monoblock-cyclo"
  Links = -> [Cut370,Cut373,Cut374]
FEATURE [Part::Cylinder] Cylinder888  label="Válec888"
  Angle = 360
  AttacherType = Attacher::AttachEngine3D
  Height = 19
  Placement = pos=(0,0,1) rot=(0,0,1;0rad)
  Radius = 28.5
FEATURE [Part::FeaturePython] cycloidgear005  # WARN: FeaturePython — macro-defined, semantics opaque (R4)
  AttacherType = Attacher::AttachEngine3D
  Placement = pos=(0,0,-1) rot=(0,0,1;0rad)
  backlash = 0
  beta = 50
  clearance = 0.25
  double_helix = true
  height = 22
  inner_diameter = 5
  module = 1.2
  numpoints = 15
  outer_diameter = 5
  teeth = 33
  version = 0.0.3
FEATURE [Part::Cut] Cut369  label="G-midi_exp-ring-cyclo001"
  Base = -> Cylinder888
  Placement = pos=(0,0,10) rot=(0,0,1;0rad)
  Tool = -> cycloidgear005
FEATURE [Mesh::Feature] Mesh001  label="G-midi_monoblock-cyclo (Meshed)"
FEATURE [Part::Torus] Torus007  label="Anuloid007"
  Angle1 = -180
  Angle2 = 180
  Angle3 = 360
  AttacherType = Attacher::AttachEngine3D
  Placement = pos=(0,0,22.5) rot=(0,0,1;0rad)
  Radius1 = 27.75
  Radius2 = 2.2
FEATURE [Part::Cylinder] Cylinder914  label="Válec914"
  Angle = 360
  AttacherType = Attacher::AttachEngine3D
  Height = 10
  Placement = pos=(0,0,20) rot=(0,0,1;0rad)
  Radius = 28.5
FEATURE [Part::Cylinder] Cylinder915  label="Válec915"
  Angle = 360
  AttacherType = Attacher::AttachEngine3D
  Height = 10
  Placement = pos=(23.5589,9.75843,25) rot=(0,0,-1;1.1781rad)
  Radius = 1.5
FEATURE [Part::Cylinder] Cylinder916  label="Válec916"
  Angle = 360
  AttacherType = Attacher::AttachEngine3D
  Height = 10
  Placement = pos=(28,0,23.5) rot=(0,0,1;0.392699rad)
  Radius = 2.2
FEATURE [Part::Box] Box348  label="Krychle348"
  AttacherType = Attacher::AttachEngine3D
  Height = 2
  Length = 6
  Placement = pos=(-21.4734,5.6474,25) rot=(0,0,1;1.1781rad)
  Width = 7
FEATURE [Part::Cylinder] Cylinder917  label="Válec917"
  Angle = 360
  AttacherType = Attacher::AttachEngine3D
  Height = 10
  Placement = pos=(9.75843,-23.5589,25) rot=(0,0,1;3.53429rad)
  Radius = 1.5
FEATURE [Part::Cylinder] Cylinder918  label="Válec918"
  Angle = 360
  AttacherType = Attacher::AttachEngine3D
  Height = 10
  Placement = pos=(9.75843,23.5589,25) rot=(0,0,-1;0.392699rad)
  Radius = 1.5
FEATURE [Part::Cylinder] Cylinder919  label="Válec919"
  Angle = 360
  AttacherType = Attacher::AttachEngine3D
  Height = 9
  Placement = pos=(0,0,11) rot=(0,0,1;0rad)
  Radius = 28.5
FEATURE [Part::Box] Box349  label="Krychle349"
  AttacherType = Attacher::AttachEngine3D
  Height = 2
  Length = 6
  Placement = pos=(-11.1907,19.1773,25) rot=(0,0,1;0.392699rad)
  Width = 7
FEATURE [Part::Box] Box350  label="Krychle350"
  AttacherType = Attacher::AttachEngine3D
  Height = 2
  Length = 6
  Placement = pos=(-5.6474,-21.4734,25) rot=(0,0,1;2.74889rad)
  Width = 7
FEATURE [Part::Box] Box351  label="Krychle351"
  AttacherType = Attacher::AttachEngine3D
  Height = 2
  Length = 6
  Placement = pos=(5.6474,21.4734,25) rot=(0,0,-1;0.392699rad)
  Width = 7
FEATURE [Part::Cylinder] Cylinder920  label="Válec920"
  Angle = 360
  AttacherType = Attacher::AttachEngine3D
  Height = 10
  Placement = pos=(-23.5589,-9.75843,25) rot=(0,0,1;1.96349rad)
  Radius = 1.5
FEATURE [Part::FeaturePython] wormgear051  # WARN: FeaturePython — macro-defined, semantics opaque (R4)
  AttacherType = Attacher::AttachEngine3D
  Placement = pos=(0,0,19) rot=(0,0,1;1.1205rad)
  beta = 29.1676
  clearance = 0.25
  diameter = 43
  head = 0
  height = 12
  module = 0.8
  pressure_angle = 20
  reverse_pitch = true
  teeth = 30
  version = 0.0.3
FEATURE [Part::Cut] Cut380
  Base = -> Cylinder914
  Tool = -> wormgear051
FEATURE [Part::Cut] Cut376
  Base = -> Cut380
  Tool = -> Torus007
FEATURE [Part::Cut] Cut379
  Base = -> Cut376
  Tool = -> Cylinder916
FEATURE [Part::FeaturePython] wormgear052  # WARN: FeaturePython — macro-defined, semantics opaque (R4)
  AttacherType = Attacher::AttachEngine3D
  Placement = pos=(0,0,9) rot=(0,0,1;1.17286rad)
  beta = 29.1676
  clearance = 0.25
  diameter = 43
  head = 0
  height = 12
  module = 0.8
  pressure_angle = 20
  reverse_pitch = false
  teeth = 30
  version = 0.0.3
FEATURE [Part::Cut] Cut375
  Base = -> Cylinder919
  Tool = -> wormgear052
FEATURE [Part::Box] Box352  label="Krychle352"
  AttacherType = Attacher::AttachEngine3D
  Height = 2
  Length = 6
  Placement = pos=(19.1773,11.1907,25) rot=(0,0,-1;1.1781rad)
  Width = 7
FEATURE [Part::Cylinder] Cylinder921  label="Válec921"
  Angle = 360
  AttacherType = Attacher::AttachEngine3D
  Height = 10
  Placement = pos=(-23.5589,9.75843,25) rot=(0,0,1;1.1781rad)
  Radius = 1.5
FEATURE [Part::Cylinder] Cylinder922  label="Válec922"
  Angle = 360
  AttacherType = Attacher::AttachEngine3D
  Height = 10
  Placement = pos=(-9.75843,-23.5589,25) rot=(0,0,1;2.74889rad)
  Radius = 1.5
FEATURE [Part::Cylinder] Cylinder923  label="Válec923"
  Angle = 360
  AttacherType = Attacher::AttachEngine3D
  Height = 10
  Placement = pos=(-9.75843,23.5589,25) rot=(0,0,1;0.392699rad)
  Radius = 1.5
FEATURE [Part::Box] Box353  label="Krychle353"
  AttacherType = Attacher::AttachEngine3D
  Height = 2
  Length = 6
  Placement = pos=(21.4734,-5.6474,25) rot=(0,0,-1;1.96349rad)
  Width = 7
FEATURE [Part::Box] Box354  label="Krychle354"
  AttacherType = Attacher::AttachEngine3D
  Height = 2
  Length = 6
  Placement = pos=(-19.1773,-11.1907,25) rot=(0,0,1;1.96349rad)
  Width = 7
FEATURE [Part::Cylinder] Cylinder924  label="Válec924"
  Angle = 360
  AttacherType = Attacher::AttachEngine3D
  Height = 10
  Placement = pos=(23.5589,-9.75843,25) rot=(0,0,-1;1.96349rad)
  Radius = 1.5
FEATURE [Part::Box] Box355  label="Krychle355"
  AttacherType = Attacher::AttachEngine3D
  Height = 2
  Length = 6
  Placement = pos=(11.1907,-19.1773,25) rot=(0,0,1;3.53429rad)
  Width = 7
FEATURE [Part::Compound] Compound572
  Links = -> [Cylinder923,Cylinder921,Cylinder920,Cylinder922,Cylinder917,Cylinder924,Cylinder915,Cylinder918]
FEATURE [Part::Compound] Compound573
  Links = -> [Box349,Box348,Box354,Box350,Box355,Box353,Box352,Box351]
FEATURE [Part::Cut] Cut378
  Base = -> Cut379
  Tool = -> Compound573
FEATURE [Part::Cut] Cut377
  Base = -> Cut378
  Tool = -> Compound572
FEATURE [Part::Compound] Compound571  label="G-midi_rybovina-cyclo1"
  Links = -> [Cut377,Cut375]
FEATURE [Part::Box] Box356  label="Krychle356"
  AttacherType = Attacher::AttachEngine3D
  Height = 2
  Length = 6
  Placement = pos=(19.1773,11.1907,25) rot=(0,0,-1;1.1781rad)
  Width = 7
FEATURE [Part::Box] Box357  label="Krychle357"
  AttacherType = Attacher::AttachEngine3D
  Height = 2
  Length = 6
  Placement = pos=(5.6474,21.4734,25) rot=(0,0,-1;0.392699rad)
  Width = 7
FEATURE [Part::Box] Box358  label="Krychle358"
  AttacherType = Attacher::AttachEngine3D
  Height = 2
  Length = 6
  Placement = pos=(-5.6474,-21.4734,25) rot=(0,0,1;2.74889rad)
  Width = 7
FEATURE [Part::Box] Box359  label="Krychle359"
  AttacherType = Attacher::AttachEngine3D
  Height = 2
  Length = 6
  Placement = pos=(-21.4734,5.6474,25) rot=(0,0,1;1.1781rad)
  Width = 7
FEATURE [Part::Box] Box360  label="Krychle360"
  AttacherType = Attacher::AttachEngine3D
  Height = 2
  Length = 6
  Placement = pos=(-11.1907,19.1773,25) rot=(0,0,1;0.392699rad)
  Width = 7
FEATURE [Part::Box] Box361  label="Krychle361"
  AttacherType = Attacher::AttachEngine3D
  Height = 2
  Length = 6
  Placement = pos=(-19.1773,-11.1907,25) rot=(0,0,1;1.96349rad)
  Width = 7
FEATURE [Part::Box] Box362  label="Krychle362"
  AttacherType = Attacher::AttachEngine3D
  Height = 2
  Length = 6
  Placement = pos=(21.4734,-5.6474,25) rot=(0,0,-1;1.96349rad)
  Width = 7
FEATURE [Part::Box] Box363  label="Krychle363"
  AttacherType = Attacher::AttachEngine3D
  Height = 2
  Length = 6
  Placement = pos=(11.1907,-19.1773,25) rot=(0,0,1;3.53429rad)
  Width = 7
FEATURE [Part::Compound] Compound574
  Links = -> [Box360,Box359,Box361,Box358,Box363,Box362,Box356,Box357]
FEATURE [Part::Cylinder] Cylinder925  label="Válec925"
  Angle = 360
  AttacherType = Attacher::AttachEngine3D
  Height = 10
  Placement = pos=(9.75843,23.5589,25) rot=(0,0,-1;0.392699rad)
  Radius = 1.5
FEATURE [Part::Cylinder] Cylinder926  label="Válec926"
  Angle = 360
  AttacherType = Attacher::AttachEngine3D
  Height = 10
  Placement = pos=(-23.5589,-9.75843,25) rot=(0,0,1;1.96349rad)
  Radius = 1.5
FEATURE [Part::Cylinder] Cylinder927  label="Válec927"
  Angle = 360
  AttacherType = Attacher::AttachEngine3D
  Height = 10
  Placement = pos=(23.5589,9.75843,25) rot=(0,0,-1;1.1781rad)
  Radius = 1.5
FEATURE [Part::Cylinder] Cylinder928  label="Válec928"
  Angle = 360
  AttacherType = Attacher::AttachEngine3D
  Height = 10
  Placement = pos=(9.75843,-23.5589,25) rot=(0,0,1;3.53429rad)
  Radius = 1.5
FEATURE [Part::Cylinder] Cylinder929  label="Válec929"
  Angle = 360
  AttacherType = Attacher::AttachEngine3D
  Height = 10
  Placement = pos=(23.5589,-9.75843,25) rot=(0,0,-1;1.96349rad)
  Radius = 1.5
FEATURE [Part::Cylinder] Cylinder930  label="Válec930"
  Angle = 360
  AttacherType = Attacher::AttachEngine3D
  Height = 10
  Placement = pos=(-23.5589,9.75843,25) rot=(0,0,1;1.1781rad)
  Radius = 1.5
FEATURE [Part::Cylinder] Cylinder931  label="Válec931"
  Angle = 360
  AttacherType = Attacher::AttachEngine3D
  Height = 10
  Placement = pos=(-9.75843,23.5589,25) rot=(0,0,1;0.392699rad)
  Radius = 1.5
FEATURE [Part::Cylinder] Cylinder932  label="Válec932"
  Angle = 360
  AttacherType = Attacher::AttachEngine3D
  Height = 10
  Placement = pos=(-9.75843,-23.5589,25) rot=(0,0,1;2.74889rad)
  Radius = 1.5
FEATURE [Part::Compound] Compound575
  Links = -> [Cylinder931,Cylinder930,Cylinder926,Cylinder932,Cylinder928,Cylinder929,Cylinder927,Cylinder925]
FEATURE [Part::Torus] Torus008  label="Anuloid008"
  Angle1 = -180
  Angle2 = 180
  Angle3 = 360
  AttacherType = Attacher::AttachEngine3D
  Placement = pos=(0,0,22.5) rot=(0,0,1;0rad)
  Radius1 = 27.75
  Radius2 = 2.2
FEATURE [Part::Cylinder] Cylinder933  label="Válec933"
  Angle = 360
  AttacherType = Attacher::AttachEngine3D
  Height = 10
  Placement = pos=(28,0,23.5) rot=(0,0,1;0.392699rad)
  Radius = 2.2
FEATURE [Part::Cut] Cut381
  Base = -> Cut369
  Tool = -> Compound574
FEATURE [Part::Cut] Cut382
  Base = -> Cut381
  Tool = -> Torus008
FEATURE [Part::Cut] Cut383
  Base = -> Cut382
  Tool = -> Cylinder933
FEATURE [Part::Cut] Cut384  label="G-midi_rybovina-cyclo"
  Base = -> Cut383
  Placement = pos=(0,0,10) rot=(0,0,1;0rad)
  Tool = -> Compound575
FEATURE [Mesh::Feature] Mesh002  label="G-midi_rybovina-cyclo (Meshed)"
FEATURE [Mesh::Feature] Mesh003  label="G-midi_outer-gear001 (Meshed)"
FEATURE [Part::Torus] Torus002  label="Anuloid002"
  Angle1 = -180
  Angle2 = 180
  Angle3 = 360
  AttacherType = Attacher::AttachEngine3D
  Placement = pos=(0,0,23.5) rot=(0,0,1;0rad)
  Radius1 = 28
  Radius2 = 2.2
FEATURE [Part::FeaturePython] Tube011  # WARN: FeaturePython — macro-defined, semantics opaque (R4)
  AttacherType = Attacher::AttachEngine3D
  Height = 20
  InnerRadius = 29
  OuterRadius = 35
  Placement = pos=(0,0,10) rot=(0,0,1;0rad)
FEATURE [Part::Cut] Cut052
  Base = -> Tube011
  Tool = -> Torus002
FEATURE [Part::Cylinder] Cylinder152  label="Válec152"
  Angle = 360
  AttacherType = Attacher::AttachEngine3D
  Height = 10
  Placement = pos=(22.6274,-22.6274,10) rot=(0,0,1;3.92699rad)
  Radius = 1.5
FEATURE [Part::Cylinder] Cylinder153  label="Válec153"
  Angle = 360
  AttacherType = Attacher::AttachEngine3D
  Height = 10
  Placement = pos=(32,1.1e-14,10) rot=(0,0,-1;1.5708rad)
  Radius = 1.5
FEATURE [Part::Cylinder] Cylinder154  label="Válec154"
  Angle = 360
  AttacherType = Attacher::AttachEngine3D
  Height = 10
  Placement = pos=(22.6274,22.6274,10) rot=(0,0,-1;0.785398rad)
  Radius = 1.5
FEATURE [Part::Cylinder] Cylinder157  label="Válec157"
  Angle = 360
  AttacherType = Attacher::AttachEngine3D
  Height = 20
  Placement = pos=(18,38,25) rot=(0,1,0;1.5708rad)
  Radius = 4
FEATURE [Part::Box] Box067  label="Krychle067"
  AttacherType = Attacher::AttachEngine3D
  Height = 20
  Length = 20.4
  Placement = pos=(-10.2,20,10) rot=(0,0,1;0rad)
  Width = 27
FEATURE [Part::Cylinder] Cylinder156  label="Válec156"
  Angle = 360
  AttacherType = Attacher::AttachEngine3D
  Height = 20
  Placement = pos=(4,38,25) rot=(0,1,0;1.5708rad)
  Radius = 1.5
FEATURE [Part::Box] Box059  label="Krychle059"
  AttacherType = Attacher::AttachEngine3D
  Height = 2
  Length = 6
  Placement = pos=(-22.6274,18.3848,14) rot=(0,0,1;0.785398rad)
  Width = 6
FEATURE [Part::Cylinder] Cylinder151  label="Válec151"
  Angle = 360
  AttacherType = Attacher::AttachEngine3D
  Height = 10
  Placement = pos=(1e-14,-32,10) rot=(0,0,1;3.14159rad)
  Radius = 1.5
FEATURE [Part::Box] Box063  label="Krychle063"
  AttacherType = Attacher::AttachEngine3D
  Height = 2
  Length = 6
  Placement = pos=(22.6274,-18.3848,14) rot=(0,0,1;3.92699rad)
  Width = 6
FEATURE [Part::Box] Box065  label="Krychle065"
  AttacherType = Attacher::AttachEngine3D
  Height = 2
  Length = 6
  Placement = pos=(18.3848,22.6274,14) rot=(0,0,-1;0.785398rad)
  Width = 6
FEATURE [Part::Box] Box062  label="Krychle062"
  AttacherType = Attacher::AttachEngine3D
  Height = 2
  Length = 6
  Placement = pos=(3,-29,14) rot=(0,0,1;3.14159rad)
  Width = 6
FEATURE [Part::Cylinder] Cylinder158  label="Válec158"
  Angle = 360
  AttacherType = Attacher::AttachEngine3D
  Height = 20
  Placement = pos=(-24,38,25) rot=(0,1,0;1.5708rad)
  Radius = 1.5
FEATURE [Part::Cylinder] Cylinder146  label="Válec146"
  Angle = 360
  AttacherType = Attacher::AttachEngine3D
  Height = 10
  Placement = pos=(28,0,23.5) rot=(0,0,1;0rad)
  Radius = 2.2
FEATURE [Part::Cut] Cut053
  Base = -> Cut052
  Tool = -> Cylinder146
FEATURE [Part::Box] Box060  label="Krychle060"
  AttacherType = Attacher::AttachEngine3D
  Height = 2
  Length = 6
  Placement = pos=(-29,-3,14) rot=(0,0,1;1.5708rad)
  Width = 6
FEATURE [Part::Cylinder] Cylinder147  label="Válec147"
  Angle = 360
  AttacherType = Attacher::AttachEngine3D
  Height = 10
  Placement = pos=(0,32,10) rot=(0,0,1;0rad)
  Radius = 1.5
FEATURE [Part::Cylinder] Cylinder155  label="Válec155"
  Angle = 360
  AttacherType = Attacher::AttachEngine3D
  Height = 20
  Placement = pos=(0,0,10) rot=(0,0,1;0rad)
  Radius = 35
FEATURE [Part::Box] Box058  label="Krychle058"
  AttacherType = Attacher::AttachEngine3D
  Height = 2
  Length = 6
  Placement = pos=(-3,29,14) rot=(0,0,1;0rad)
  Width = 6
FEATURE [Part::Cylinder] Cylinder148  label="Válec148"
  Angle = 360
  AttacherType = Attacher::AttachEngine3D
  Height = 10
  Placement = pos=(-22.6274,22.6274,10) rot=(0,0,1;0.785398rad)
  Radius = 1.5
FEATURE [Part::Cylinder] Cylinder149  label="Válec149"
  Angle = 360
  AttacherType = Attacher::AttachEngine3D
  Height = 10
  Placement = pos=(-32,0,10) rot=(0,0,1;1.5708rad)
  Radius = 1.5
FEATURE [Part::Box] Box064  label="Krychle064"
  AttacherType = Attacher::AttachEngine3D
  Height = 2
  Length = 6
  Placement = pos=(29,3,14) rot=(0,0,-1;1.5708rad)
  Width = 6
FEATURE [Part::Box] Box066  label="Krychle066"
  AttacherType = Attacher::AttachEngine3D
  Height = 20
  Length = 50
  Placement = pos=(-25,15,10) rot=(0,0,1;0rad)
  Width = 32
FEATURE [Part::Cut] Cut056
  Base = -> Box066
  Tool = -> Cylinder155
FEATURE [Part::Cut] Cut057
  Base = -> Cut056
  Tool = -> Box067
FEATURE [Part::Box] Box061  label="Krychle061"
  AttacherType = Attacher::AttachEngine3D
  Height = 2
  Length = 6
  Placement = pos=(-18.3848,-22.6274,14) rot=(0,0,1;2.35619rad)
  Width = 6
FEATURE [Part::Compound] Compound048
  Links = -> [Box059,Box060,Box061,Box062,Box063,Box064,Box065,Box058]
FEATURE [Part::Cylinder] Cylinder159  label="Válec159"
  Angle = 360
  AttacherType = Attacher::AttachEngine3D
  Height = 20
  Placement = pos=(-38,38,25) rot=(0,1,0;1.5708rad)
  Radius = 4
FEATURE [Part::Cylinder] Cylinder150  label="Válec150"
  Angle = 360
  AttacherType = Attacher::AttachEngine3D
  Height = 10
  Placement = pos=(-22.6274,-22.6274,10) rot=(0,0,1;2.35619rad)
  Radius = 1.5
FEATURE [Part::Compound] Compound047
  Links = -> [Cylinder148,Cylinder149,Cylinder150,Cylinder151,Cylinder152,Cylinder153,Cylinder154,Cylinder147]
FEATURE [Part::Cut] Cut054
  Base = -> Cut053
  Tool = -> Compound047
FEATURE [Part::Cut] Cut055  label="gearovina-midi_loziskovina1"
  Base = -> Cut054
  Tool = -> Compound048
FEATURE [Part::Cylinder] Cylinder1817  label="Válec1817"
  Angle = 360
  AttacherType = Attacher::AttachEngine3D
  Height = 20
  Placement = pos=(-38,38,15) rot=(0,1,0;1.5708rad)
  Radius = 4
FEATURE [Part::Cylinder] Cylinder1819  label="Válec1819"
  Angle = 360
  AttacherType = Attacher::AttachEngine3D
  Height = 20
  Placement = pos=(-24,38,15) rot=(0,1,0;1.5708rad)
  Radius = 1.5
FEATURE [Part::Cylinder] Cylinder1816  label="Válec1816"
  Angle = 360
  AttacherType = Attacher::AttachEngine3D
  Height = 20
  Placement = pos=(18,38,15) rot=(0,1,0;1.5708rad)
  Radius = 4
FEATURE [Part::Compound] Compound049
  Links = -> [Cylinder157,Cylinder159,Cylinder1816,Cylinder1817]
  Placement = pos=(0,4,0) rot=(0,0,1;0rad)
FEATURE [Part::Cut] Cut058
  Base = -> Cut057
  Tool = -> Compound049
FEATURE [Part::Cylinder] Cylinder1818  label="Válec1818"
  Angle = 360
  AttacherType = Attacher::AttachEngine3D
  Height = 20
  Placement = pos=(4,38,15) rot=(0,1,0;1.5708rad)
  Radius = 1.5
FEATURE [Part::Compound] Compound050
  Links = -> [Cylinder156,Cylinder158,Cylinder1818,Cylinder1819]
  Placement = pos=(0,4,0) rot=(0,0,1;0rad)
FEATURE [Part::Cut] Cut059
  Base = -> Cut058
  Tool = -> Compound050
FEATURE [Part::Compound] Compound051  label="G-midi_bearing-ring"
  Links = -> [Cut059,Cut055]
FEATURE [Part::Compound] Compound576  label="G-midi_outer-gear002-cyclo"
  Links = -> [Cut366,Cylinder886,cycloidgear003]
  Placement = pos=(-14,0,10) rot=(0,0,-1;0.331613rad)
FEATURE [Part::Compound] Compound577  label="G-midi_outer-gear003-cyclo"
  Links = -> [Cut366,Cylinder886,cycloidgear003]
  Placement = pos=(7,-12.1244,10) rot=(0,0,1;1.76278rad)
FEATURE [Part::Compound] Compound578  label="G-midi_outer-gear004-cyclo"
  Links = -> [Cut366,Cylinder886,cycloidgear003]
  Placement = pos=(7,-12.1244,10) rot=(0,0,1;1.76278rad)
FEATURE [Part::Compound] Compound579  label="G-midi_outer-gear005-cyclo"
  Links = -> [Cut366,Cylinder886,cycloidgear003]
  Placement = pos=(7,12.1244,10) rot=(0,0,1;3.85718rad)
FEATURE [Part::Compound] Compound580  label="G-midi_outer-gear006-cyclo"
  Links = -> [Cut366,Cylinder886,cycloidgear003]
  Placement = pos=(7,12.1244,10) rot=(0,0,1;3.85718rad)
FEATURE [Part::Cylinder] Cylinder  label="Válec"
  Angle = 360
  AttacherType = Attacher::AttachEngine3D
  Height = 30
  Radius = 4.5
FEATURE [Part::FeaturePython] cycloidgear007  # WARN: FeaturePython — macro-defined, semantics opaque (R4)
  AttacherType = Attacher::AttachEngine3D
  Placement = pos=(0,0,30) rot=(0,0,1;0.15708rad)
  backlash = 0
  beta = 50
  clearance = 0.25
  double_helix = false
  height = 10
  inner_diameter = 5
  module = 1.1
  numpoints = 15
  outer_diameter = 5
  teeth = 15
  version = 0.0.3
FEATURE [Mesh::Feature] Mesh004  label="G-midi_outer-gear001 (Meshed)001"
FEATURE [Part::FeaturePython] cycloidgear008  # WARN: FeaturePython — macro-defined, semantics opaque (R4)
  AttacherType = Attacher::AttachEngine3D
  Placement = pos=(0,0,0) rot=(0,0,1;0.436332rad)
  backlash = 0
  beta = 50
  clearance = 0.25
  double_helix = false
  height = 10
  inner_diameter = 3
  module = 1.32
  numpoints = 15
  outer_diameter = 5
  teeth = 9
  version = 0.0.3
FEATURE [Part::Cylinder] Cylinder1820  label="Válec1820"
  Angle = 360
  AttacherType = Attacher::AttachEngine3D
  Height = 10
  Placement = pos=(0,3,-20) rot=(0,0,1;0rad)
  Radius = 1
FEATURE [Part::Cylinder] Cylinder1821  label="Válec1821"
  Angle = 360
  AttacherType = Attacher::AttachEngine3D
  Height = 10
  Placement = pos=(0,0,-10) rot=(0,0,1;0rad)
  Radius = 4.5
FEATURE [Part::Cylinder] Cylinder1822  label="Válec1822"
  Angle = 360
  AttacherType = Attacher::AttachEngine3D
  Height = 10
  Placement = pos=(-3,0,-20) rot=(0,0,1;1.5708rad)
  Radius = 1
FEATURE [Part::Cylinder] Cylinder1823  label="Válec1823"
  Angle = 360
  AttacherType = Attacher::AttachEngine3D
  Height = 10
  Placement = pos=(-1e-15,-3,-20) rot=(0,0,1;3.14159rad)
  Radius = 1
FEATURE [Part::Cylinder] Cylinder1824  label="Válec1824"
  Angle = 360
  AttacherType = Attacher::AttachEngine3D
  Height = 10
  Placement = pos=(3,-1e-15,-20) rot=(0,0,-1;1.5708rad)
  Radius = 1
FEATURE [Part::Cylinder] Cylinder1825  label="Válec1825"
  Angle = 360
  AttacherType = Attacher::AttachEngine3D
  Height = 10
  Placement = pos=(0,0,-10) rot=(0,0,1;0rad)
  Radius = 4.5
FEATURE [Part::Compound] Compound581
  Links = -> [Cylinder1820,Cylinder1822,Cylinder1823,Cylinder1824]
FEATURE [Part::Cylinder] Cylinder1826  label="Válec1826"
  Angle = 360
  AttacherType = Attacher::AttachEngine3D
  Height = 10
  Placement = pos=(0,0,-20) rot=(0,0,1;0rad)
  Radius = 4.5
FEATURE [Part::Cut] Cut385
  Base = -> Cylinder1826
  Tool = -> Compound581
FEATURE [Part::Box] Box  label="Krychle"
  AttacherType = Attacher::AttachEngine3D
  Height = 10
  Length = 16
  Placement = pos=(-8,-0.6,-20) rot=(0,0,1;0rad)
  Width = 1.2
FEATURE [Part::Cylinder] Cylinder1827  label="Válec1827"
  Angle = 360
  AttacherType = Attacher::AttachEngine3D
  Height = 10
  Placement = pos=(0,0,-20) rot=(0,0,1;0rad)
  Radius = 1.4
FEATURE [Part::Box] Box364  label="Krychle364"
  AttacherType = Attacher::AttachEngine3D
  Height = 10
  Length = 16
  Placement = pos=(-5.23259,-6.08112,-20) rot=(0,0,1;0.785398rad)
  Width = 1.2
FEATURE [Part::Box] Box365  label="Krychle365"
  AttacherType = Attacher::AttachEngine3D
  Height = 10
  Length = 16
  Placement = pos=(6.08112,-5.23259,-20) rot=(0,0,1;2.35619rad)
  Width = 1.2
FEATURE [Part::Box] Box366  label="Krychle366"
  AttacherType = Attacher::AttachEngine3D
  Height = 10
  Length = 16
  Placement = pos=(-5.23259,-6.08112,-20) rot=(0,0,1;0.785398rad)
  Width = 1.2
FEATURE [Part::Box] Box367  label="Krychle367"
  AttacherType = Attacher::AttachEngine3D
  Height = 10
  Length = 16
  Placement = pos=(6.08112,-5.23259,-20) rot=(0,0,1;2.35619rad)
  Width = 1.2
FEATURE [Part::Cylinder] Cylinder1828  label="Válec1828"
  Angle = 360
  AttacherType = Attacher::AttachEngine3D
  Height = 10
  Placement = pos=(0,0,-20) rot=(0,0,1;0rad)
  Radius = 1.4
FEATURE [Part::Cylinder] Cylinder1829  label="Válec1829"
  Angle = 360
  AttacherType = Attacher::AttachEngine3D
  Height = 10
  Placement = pos=(0,0,-20) rot=(0,0,1;0rad)
  Radius = 1
FEATURE [Part::Cylinder] Cylinder1830  label="Válec1830"
  Angle = 360
  AttacherType = Attacher::AttachEngine3D
  Height = 10
  Placement = pos=(0,0,-20) rot=(0,0,1;0rad)
  Radius = 1
FEATURE [Part::Cylinder] Cylinder1831  label="Válec1831"
  Angle = 360
  AttacherType = Attacher::AttachEngine3D
  Height = 10
  Placement = pos=(0,0,-20) rot=(0,0,1;0rad)
  Radius = 1
FEATURE [Part::Cut] Cut386
  Base = -> Box365
  Tool = -> Cylinder1831
FEATURE [Part::Cut] Cut387
  Base = -> Box366
  Tool = -> Cylinder1830
FEATURE [Part::Cylinder] Cylinder1832  label="Válec1832"
  Angle = 360
  AttacherType = Attacher::AttachEngine3D
  Height = 10
  Placement = pos=(0,0,-20) rot=(0,0,1;0rad)
  Radius = 1
FEATURE [Part::Cut] Cut388
  Base = -> Cylinder1827
  Tool = -> Cylinder1832
FEATURE [Part::Compound] Compound582  label="G-midi_sun-unmixo"
  Links = -> [Cut388,Cut387,Cut386]
FEATURE [Part::Cut] Cut389
  Base = -> Cut385
  Tool = -> Box364
FEATURE [Part::Cut] Cut390  label="G-midi_sun-mixo1"
  Base = -> Cut389
  Tool = -> Box367
FEATURE [Part::Cylinder] Cylinder1833  label="Válec1833"
  Angle = 360
  AttacherType = Attacher::AttachEngine3D
  Height = 10
  Placement = pos=(0,0,-20) rot=(0,0,1;0rad)
  Radius = 1.4
FEATURE [Part::Cut] Cut391  label="G-midi_sun-mixo"
  Base = -> Cut390
  Tool = -> Cylinder1833
FEATURE [Part::Cylinder] Cylinder1834  label="Válec1834"
  Angle = 360
  AttacherType = Attacher::AttachEngine3D
  Height = 10
  Placement = pos=(3,-1e-15,-20) rot=(0,0,-1;1.5708rad)
  Radius = 1
FEATURE [Part::Cylinder] Cylinder1835  label="Válec1835"
  Angle = 360
  AttacherType = Attacher::AttachEngine3D
  Height = 10
  Placement = pos=(0,3,-20) rot=(0,0,1;0rad)
  Radius = 1
FEATURE [Part::Cylinder] Cylinder1836  label="Válec1836"
  Angle = 360
  AttacherType = Attacher::AttachEngine3D
  Height = 10
  Placement = pos=(-1e-15,-3,-20) rot=(0,0,1;3.14159rad)
  Radius = 1
FEATURE [Part::Cylinder] Cylinder1837  label="Válec1837"
  Angle = 360
  AttacherType = Attacher::AttachEngine3D
  Height = 10
  Placement = pos=(-3,0,-20) rot=(0,0,1;1.5708rad)
  Radius = 1
FEATURE [Part::Compound] Compound583
  Links = -> [Cylinder1835,Cylinder1837,Cylinder1836,Cylinder1834]
FEATURE [Part::Box] Box368  label="Krychle368"
  AttacherType = Attacher::AttachEngine3D
  Height = 10
  Length = 16
  Placement = pos=(-8,0,-20) rot=(0,0,1;0rad)
  Width = 8
FEATURE [Part::Cylinder] Cylinder1838  label="Válec1838"
  Angle = 360
  AttacherType = Attacher::AttachEngine3D
  Height = 10
  Placement = pos=(0,0,-20) rot=(0,0,1;0rad)
  Radius = 1.4
FEATURE [Part::Cylinder] Cylinder1839  label="Válec1839"
  Angle = 360
  AttacherType = Attacher::AttachEngine3D
  Height = 10
  Placement = pos=(0,0,-20) rot=(0,0,1;0rad)
  Radius = 4.5
FEATURE [Part::Box] Box369  label="Krychle369"
  AttacherType = Attacher::AttachEngine3D
  Height = 10
  Length = 16
  Placement = pos=(-5.65685,-5.65685,-20) rot=(0,0,1;0.785398rad)
  Width = 8
FEATURE [Part::Box] Box370  label="Krychle370"
  AttacherType = Attacher::AttachEngine3D
  Height = 10
  Length = 16
  Placement = pos=(5.65685,-5.65685,-20) rot=(0,0,1;2.35619rad)
  Width = 8
FEATURE [Part::Cut] Cut392
  Base = -> Cylinder1839
  Tool = -> Cylinder1838
FEATURE [Part::Cut] Cut393
  Base = -> Cut392
  Tool = -> Box370
FEATURE [Part::Cut] Cut394
  Base = -> Cut393
  Tool = -> Box369
FEATURE [Part::Cylinder] Cylinder1840  label="Válec1840"
  Angle = 360
  AttacherType = Attacher::AttachEngine3D
  Height = 10
  Placement = pos=(3,-1e-15,-20) rot=(0,0,-1;1.5708rad)
  Radius = 1
FEATURE [Part::Cut] Cut395
  Base = -> Cut394
  Tool = -> Cylinder1840
FEATURE [Part::Cut] Cut396
  Base = -> Cut394
  Placement = pos=(0,0,0) rot=(0,0,1;3.14159rad)
  Tool = -> Cylinder1840
FEATURE [Part::Cylinder] Cylinder1841  label="Válec1841"
  Angle = 360
  AttacherType = Attacher::AttachEngine3D
  Height = 5
  Placement = pos=(0,0,-15) rot=(0,0,1;0rad)
  Radius = 1.4
FEATURE [Part::Compound] Compound584  label="G-midi_sun-sym-mixo"
  Links = -> [Cut395,Cut396,Cylinder1841]
FEATURE [Part::Torus] Torus009  label="Anuloid009"
  Angle1 = -180
  Angle2 = 180
  Angle3 = 360
  AttacherType = Attacher::AttachEngine3D
  Placement = pos=(0,0,22.5) rot=(0,0,1;0rad)
  Radius1 = 27.75
  Radius2 = 2.2
FEATURE [Part::FeaturePython] wormgear053  # WARN: FeaturePython — macro-defined, semantics opaque (R4)
  AttacherType = Attacher::AttachEngine3D
  Placement = pos=(0,0,19) rot=(0,0,1;1.1205rad)
  beta = 29.7449
  clearance = 0.25
  diameter = 42
  head = 0
  height = 12
  module = 0.8
  pressure_angle = 20
  reverse_pitch = true
  teeth = 30
  version = 0.0.3
FEATURE [Part::FeaturePython] wormgear054  # WARN: FeaturePython — macro-defined, semantics opaque (R4)
  AttacherType = Attacher::AttachEngine3D
  Placement = pos=(0,0,9) rot=(0,0,1;1.16588rad)
  beta = 29.7449
  clearance = 0.25
  diameter = 42
  head = 0
  height = 12
  module = 0.8
  pressure_angle = 20
  reverse_pitch = false
  teeth = 30
  version = 0.0.3
FEATURE [Part::Box] Box371  label="Krychle371"
  AttacherType = Attacher::AttachEngine3D
  Height = 2
  Length = 6
  Placement = pos=(-19.1773,-11.1907,25) rot=(0,0,1;1.96349rad)
  Width = 7
FEATURE [Part::Box] Box372  label="Krychle372"
  AttacherType = Attacher::AttachEngine3D
  Height = 2
  Length = 6
  Placement = pos=(21.4734,-5.6474,25) rot=(0,0,-1;1.96349rad)
  Width = 7
FEATURE [Part::Box] Box373  label="Krychle373"
  AttacherType = Attacher::AttachEngine3D
  Height = 2
  Length = 6
  Placement = pos=(5.6474,21.4734,25) rot=(0,0,-1;0.392699rad)
  Width = 7
FEATURE [Part::Cylinder] Cylinder1842  label="Válec1842"
  Angle = 360
  AttacherType = Attacher::AttachEngine3D
  Height = 10
  Placement = pos=(-23.5589,-9.75843,25) rot=(0,0,1;1.96349rad)
  Radius = 1.5
FEATURE [Part::Cylinder] Cylinder1843  label="Válec1843"
  Angle = 360
  AttacherType = Attacher::AttachEngine3D
  Height = 10
  Placement = pos=(9.75843,23.5589,25) rot=(0,0,-1;0.392699rad)
  Radius = 1.5
FEATURE [Part::Box] Box374  label="Krychle374"
  AttacherType = Attacher::AttachEngine3D
  Height = 2
  Length = 6
  Placement = pos=(-5.6474,-21.4734,25) rot=(0,0,1;2.74889rad)
  Width = 7
FEATURE [Part::Box] Box375  label="Krychle375"
  AttacherType = Attacher::AttachEngine3D
  Height = 2
  Length = 6
  Placement = pos=(-21.4734,5.6474,25) rot=(0,0,1;1.1781rad)
  Width = 7
FEATURE [Part::Cylinder] Cylinder1844  label="Válec1844"
  Angle = 360
  AttacherType = Attacher::AttachEngine3D
  Height = 9
  Placement = pos=(0,0,11) rot=(0,0,1;0rad)
  Radius = 28.5
FEATURE [Part::Cut] Cut402
  Base = -> Cylinder1844
  Tool = -> wormgear054
FEATURE [Part::Cylinder] Cylinder1845  label="Válec1845"
  Angle = 360
  AttacherType = Attacher::AttachEngine3D
  Height = 10
  Placement = pos=(0,0,20) rot=(0,0,1;0rad)
  Radius = 28.5
FEATURE [Part::Cut] Cut401
  Base = -> Cylinder1845
  Tool = -> wormgear053
FEATURE [Part::Cut] Cut398
  Base = -> Cut401
  Tool = -> Torus009
FEATURE [Part::Box] Box376  label="Krychle376"
  AttacherType = Attacher::AttachEngine3D
  Height = 2
  Length = 6
  Placement = pos=(19.1773,11.1907,25) rot=(0,0,-1;1.1781rad)
  Width = 7
FEATURE [Part::Cylinder] Cylinder1846  label="Válec1846"
  Angle = 360
  AttacherType = Attacher::AttachEngine3D
  Height = 10
  Placement = pos=(28,0,23.5) rot=(0,0,1;0.392699rad)
  Radius = 2.2
FEATURE [Part::Cut] Cut397
  Base = -> Cut398
  Tool = -> Cylinder1846
FEATURE [Part::Box] Box377  label="Krychle377"
  AttacherType = Attacher::AttachEngine3D
  Height = 2
  Length = 6
  Placement = pos=(-11.1907,19.1773,25) rot=(0,0,1;0.392699rad)
  Width = 7
FEATURE [Part::Box] Box378  label="Krychle378"
  AttacherType = Attacher::AttachEngine3D
  Height = 2
  Length = 6
  Placement = pos=(11.1907,-19.1773,25) rot=(0,0,1;3.53429rad)
  Width = 7
FEATURE [Part::Compound] Compound585
  Links = -> [Box377,Box375,Box371,Box374,Box378,Box372,Box376,Box373]
FEATURE [Part::Cut] Cut399
  Base = -> Cut397
  Tool = -> Compound585
FEATURE [Part::Cylinder] Cylinder1847  label="Válec1847"
  Angle = 360
  AttacherType = Attacher::AttachEngine3D
  Height = 10
  Placement = pos=(-23.5589,9.75843,25) rot=(0,0,1;1.1781rad)
  Radius = 1.5
FEATURE [Part::Cylinder] Cylinder1848  label="Válec1848"
  Angle = 360
  AttacherType = Attacher::AttachEngine3D
  Height = 10
  Placement = pos=(-9.75843,23.5589,25) rot=(0,0,1;0.392699rad)
  Radius = 1.5
FEATURE [Part::Cylinder] Cylinder1849  label="Válec1849"
  Angle = 360
  AttacherType = Attacher::AttachEngine3D
  Height = 10
  Placement = pos=(9.75843,-23.5589,25) rot=(0,0,1;3.53429rad)
  Radius = 1.5
FEATURE [Part::Cylinder] Cylinder1850  label="Válec1850"
  Angle = 360
  AttacherType = Attacher::AttachEngine3D
  Height = 10
  Placement = pos=(23.5589,-9.75843,25) rot=(0,0,-1;1.96349rad)
  Radius = 1.5
FEATURE [Part::Cylinder] Cylinder1851  label="Válec1851"
  Angle = 360
  AttacherType = Attacher::AttachEngine3D
  Height = 10
  Placement = pos=(23.5589,9.75843,25) rot=(0,0,-1;1.1781rad)
  Radius = 1.5
FEATURE [Part::Cylinder] Cylinder1852  label="Válec1852"
  Angle = 360
  AttacherType = Attacher::AttachEngine3D
  Height = 10
  Placement = pos=(-9.75843,-23.5589,25) rot=(0,0,1;2.74889rad)
  Radius = 1.5
FEATURE [Part::Compound] Compound587
  Links = -> [Cylinder1848,Cylinder1847,Cylinder1842,Cylinder1852,Cylinder1849,Cylinder1850,Cylinder1851,Cylinder1843]
FEATURE [Part::Cut] Cut400
  Base = -> Cut399
  Tool = -> Compound587
FEATURE [Part::Compound] Compound586  label="G-midi_rybovina"
  Links = -> [Cut400,Cut402]
FEATURE [Part::FeaturePython] wormgear055  # WARN: FeaturePython — macro-defined, semantics opaque (R4)
  AttacherType = Attacher::AttachEngine3D
  Placement = pos=(14.4,0,0) rot=(0,0,1;1.01578rad)
  beta = 34.439
  clearance = 0.25
  diameter = 14
  head = 0.5
  height = 10
  module = 0.8
  pressure_angle = 20
  reverse_pitch = true
  teeth = 12
  version = 0.0.3
FEATURE [Part::FeaturePython] wormgear056  # WARN: FeaturePython — macro-defined, semantics opaque (R4)
  AttacherType = Attacher::AttachEngine3D
  Placement = pos=(14.4,0,10) rot=(0,0,1;1.38754rad)
  beta = 30.9638
  clearance = 0.25
  diameter = 12
  head = 0.5
  height = 10
  module = 0.8
  pressure_angle = 20
  reverse_pitch = false
  teeth = 9
  version = 0.0.3
FEATURE [Part::FeaturePython] wormgear057  # WARN: FeaturePython — macro-defined, semantics opaque (R4)
  AttacherType = Attacher::AttachEngine3D
  Placement = pos=(14.4,0,-10) rot=(0,0,1;1.02974rad)
  beta = 34.439
  clearance = 0.25
  diameter = 14
  head = 0.5
  height = 10
  module = 0.8
  pressure_angle = 20
  reverse_pitch = false
  teeth = 12
  version = 0.0.3
FEATURE [Part::Cylinder] Cylinder1853  label="Válec1853"
  Angle = 360
  AttacherType = Attacher::AttachEngine3D
  Height = 5
  Placement = pos=(14.4,0,30) rot=(0,0,1;0rad)
  Radius = 2.45
FEATURE [Part::Cylinder] Cylinder1854  label="Válec1854"
  Angle = 360
  AttacherType = Attacher::AttachEngine3D
  Height = 20
  Placement = pos=(14.4,0,-20) rot=(0,0,1;0rad)
  Radius = 2.6
FEATURE [Part::Cylinder] Cylinder1855  label="Válec1855"
  Angle = 360
  AttacherType = Attacher::AttachEngine3D
  Height = 60
  Placement = pos=(14.4,0,-20) rot=(0,0,1;0rad)
  Radius = 2.6
FEATURE [Part::Cut] Cut403
  Base = -> wormgear055
  Tool = -> Cylinder1855
FEATURE [Part::Cylinder] Cylinder1856  label="Válec1856"
  Angle = 360
  AttacherType = Attacher::AttachEngine3D
  Height = 60
  Placement = pos=(14.4,0,-20) rot=(0,0,1;0rad)
  Radius = 2.6
FEATURE [Part::Cut] Cut405
  Base = -> wormgear057
  Tool = -> Cylinder1856
FEATURE [Part::Cylinder] Cylinder1857  label="Válec1857"
  Angle = 360
  AttacherType = Attacher::AttachEngine3D
  Height = 60
  Placement = pos=(14.4,0,40) rot=(0,0,1;0rad)
  Radius = 2.6
FEATURE [Part::Cut] Cut406
  Base = -> wormgear056
  Tool = -> Cylinder1857
FEATURE [Part::FeaturePython] wormgear058  # WARN: FeaturePython — macro-defined, semantics opaque (R4)
  AttacherType = Attacher::AttachEngine3D
  Placement = pos=(14.4,0,20) rot=(0,0,1;1.37008rad)
  beta = 30.9638
  clearance = 0.25
  diameter = 12
  head = 0.5
  height = 10
  module = 0.8
  pressure_angle = 20
  reverse_pitch = true
  teeth = 9
  version = 0.0.3
FEATURE [Part::Cut] Cut404
  Base = -> wormgear058
  Tool = -> Cylinder1854
FEATURE [Part::Compound] Compound588  label="G-midi_outer-gear001"
  Links = -> [Cylinder1853,Cut406,Cut404,Cut403,Cut405]
FEATURE [Mesh::Feature] Mesh006  label="G-midi_rybovina (Meshed)"
FEATURE [Part::Cylinder] Cylinder1858  label="Válec1858"
  Angle = 360
  AttacherType = Attacher::AttachEngine3D
  Height = 3
  Placement = pos=(32,1.1e-14,4) rot=(0,0,-1;1.5708rad)
  Radius = 3
FEATURE [Part::Cylinder] Cylinder1859  label="Válec1859"
  Angle = 360
  AttacherType = Attacher::AttachEngine3D
  Height = 3
  Placement = pos=(0,32,4) rot=(0,0,1;0rad)
  Radius = 3
FEATURE [Part::Cylinder] Cylinder1860  label="Válec1860"
  Angle = 360
  AttacherType = Attacher::AttachEngine3D
  Height = 3
  Placement = pos=(-32,0,4) rot=(0,0,1;1.5708rad)
  Radius = 3
FEATURE [Part::Cylinder] Cylinder1861  label="Válec1861"
  Angle = 360
  AttacherType = Attacher::AttachEngine3D
  Height = 3
  Placement = pos=(-22.6274,-22.6274,4) rot=(0,0,1;2.35619rad)
  Radius = 3
FEATURE [Part::Cylinder] Cylinder1862  label="Válec1862"
  Angle = 360
  AttacherType = Attacher::AttachEngine3D
  Height = 3
  Placement = pos=(-22.6274,22.6274,4) rot=(0,0,1;0.785398rad)
  Radius = 3
FEATURE [Part::Cylinder] Cylinder1863  label="Válec1863"
  Angle = 360
  AttacherType = Attacher::AttachEngine3D
  Height = 3
  Placement = pos=(22.6274,-22.6274,4) rot=(0,0,1;3.92699rad)
  Radius = 3
FEATURE [Part::Cylinder] Cylinder1864  label="Válec1864"
  Angle = 360
  AttacherType = Attacher::AttachEngine3D
  Height = 3
  Placement = pos=(1e-14,-32,4) rot=(0,0,1;3.14159rad)
  Radius = 3
FEATURE [Part::FeaturePython] Tube012  # WARN: FeaturePython — macro-defined, semantics opaque (R4)
  AttacherType = Attacher::AttachEngine3D
  Height = 6
  InnerRadius = 29
  OuterRadius = 35
  Placement = pos=(0,0,4) rot=(0,0,1;0rad)
FEATURE [Part::Cylinder] Cylinder1865  label="Válec1865"
  Angle = 360
  AttacherType = Attacher::AttachEngine3D
  Height = 15
  Placement = pos=(1e-14,-32,0) rot=(0,0,1;3.14159rad)
  Radius = 1.5
FEATURE [Part::Cylinder] Cylinder1866  label="Válec1866"
  Angle = 360
  AttacherType = Attacher::AttachEngine3D
  Height = 15
  Placement = pos=(-22.6274,-22.6274,0) rot=(0,0,1;2.35619rad)
  Radius = 1.5
FEATURE [Part::Cylinder] Cylinder1867  label="Válec1867"
  Angle = 360
  AttacherType = Attacher::AttachEngine3D
  Height = 15
  Placement = pos=(32,1.1e-14,0) rot=(0,0,-1;1.5708rad)
  Radius = 1.5
FEATURE [Part::Cylinder] Cylinder1868  label="Válec1868"
  Angle = 360
  AttacherType = Attacher::AttachEngine3D
  Height = 3
  Placement = pos=(22.6274,22.6274,4) rot=(0,0,-1;0.785398rad)
  Radius = 3
FEATURE [Part::Compound] Compound590
  Links = -> [Cylinder1859,Cylinder1862,Cylinder1860,Cylinder1861,Cylinder1864,Cylinder1863,Cylinder1858,Cylinder1868]
FEATURE [Part::Cut] Cut407
  Base = -> Tube012
  Tool = -> Compound590
FEATURE [Part::Cylinder] Cylinder1869  label="Válec1869"
  Angle = 360
  AttacherType = Attacher::AttachEngine3D
  Height = 15
  Placement = pos=(-22.6274,22.6274,0) rot=(0,0,1;0.785398rad)
  Radius = 1.5
FEATURE [Part::Cylinder] Cylinder1870  label="Válec1870"
  Angle = 360
  AttacherType = Attacher::AttachEngine3D
  Height = 15
  Placement = pos=(22.6274,22.6274,0) rot=(0,0,-1;0.785398rad)
  Radius = 1.5
FEATURE [Part::Cylinder] Cylinder1871  label="Válec1871"
  Angle = 360
  AttacherType = Attacher::AttachEngine3D
  Height = 15
  Placement = pos=(22.6274,-22.6274,0) rot=(0,0,1;3.92699rad)
  Radius = 1.5
FEATURE [Part::Cylinder] Cylinder1872  label="Válec1872"
  Angle = 360
  AttacherType = Attacher::AttachEngine3D
  Height = 15
  Placement = pos=(-32,0,0) rot=(0,0,1;1.5708rad)
  Radius = 1.5
FEATURE [Part::Cylinder] Cylinder1873  label="Válec1873"
  Angle = 360
  AttacherType = Attacher::AttachEngine3D
  Height = 15
  Placement = pos=(0,32,0) rot=(0,0,1;0rad)
  Radius = 1.5
FEATURE [Part::Compound] Compound589
  Links = -> [Cylinder1873,Cylinder1869,Cylinder1872,Cylinder1866,Cylinder1865,Cylinder1871,Cylinder1867,Cylinder1870]
FEATURE [Part::Cut] Cut408
  Base = -> Cut407
  Tool = -> Compound589
FEATURE [Part::Cylinder] Cylinder1874  label="Válec1874"
  Angle = 360
  AttacherType = Attacher::AttachEngine3D
  Height = 10
  Radius = 29
FEATURE [Part::Cylinder] Cylinder1875  label="Válec1875"
  Angle = 360
  AttacherType = Attacher::AttachEngine3D
  Height = 10
  Radius = 29
FEATURE [Part::FeaturePython] wormgear059  # WARN: FeaturePython — macro-defined, semantics opaque (R4)
  AttacherType = Attacher::AttachEngine3D
  Placement = pos=(0,0,0) rot=(0,0,1;1.13796rad)
  beta = 30.9638
  clearance = 0.25
  diameter = 44
  head = 0
  height = 12
  module = 0.8
  pressure_angle = 20
  reverse_pitch = false
  teeth = 33
  version = 0.0.3
FEATURE [Part::Cut] Cut409
  Base = -> Cylinder1875
  Placement = pos=(0,0,-10) rot=(0,0,1;0rad)
  Tool = -> wormgear059
FEATURE [Part::FeaturePython] wormgear060  # WARN: FeaturePython — macro-defined, semantics opaque (R4)
  AttacherType = Attacher::AttachEngine3D
  Placement = pos=(0,0,0) rot=(0,0,1;1.13446rad)
  beta = 30.9638
  clearance = 0.25
  diameter = 44
  head = 0
  height = 12
  module = 0.8
  pressure_angle = 20
  reverse_pitch = true
  teeth = 33
  version = 0.0.3
FEATURE [Part::Cut] Cut410
  Base = -> Cylinder1874
  Tool = -> wormgear060
FEATURE [Part::Compound] Compound591  label="superokruh001"
  Links = -> [Cut409,Cut410]
FEATURE [Part::FeaturePython] Tube013  # WARN: FeaturePython — macro-defined, semantics opaque (R4)
  AttacherType = Attacher::AttachEngine3D
  Height = 6
  InnerRadius = 23
  OuterRadius = 29
  Placement = pos=(0,0,-16) rot=(0,0,1;0rad)
FEATURE [Part::Cylinder] Cylinder1876  label="Válec1876"
  Angle = 360
  AttacherType = Attacher::AttachEngine3D
  Height = 15
  Placement = pos=(-18.3848,-18.3848,-20) rot=(0,0,1;2.35619rad)
  Radius = 1.5
FEATURE [Part::Cylinder] Cylinder1877  label="Válec1877"
  Angle = 360
  AttacherType = Attacher::AttachEngine3D
  Height = 15
  Placement = pos=(-18.3848,18.3848,-20) rot=(0,0,1;0.785398rad)
  Radius = 1.5
FEATURE [Part::Cylinder] Cylinder1878  label="Válec1878"
  Angle = 360
  AttacherType = Attacher::AttachEngine3D
  Height = 15
  Placement = pos=(18.3848,18.3848,-20) rot=(0,0,-1;0.785398rad)
  Radius = 1.5
FEATURE [Part::Cylinder] Cylinder1879  label="Válec1879"
  Angle = 360
  AttacherType = Attacher::AttachEngine3D
  Height = 15
  Placement = pos=(18.3848,-18.3848,-20) rot=(0,0,1;3.92699rad)
  Radius = 1.5
FEATURE [Part::Cylinder] Cylinder1880  label="Válec1880"
  Angle = 360
  AttacherType = Attacher::AttachEngine3D
  Height = 15
  Placement = pos=(26,1e-14,-20) rot=(0,0,-1;1.5708rad)
  Radius = 1.5
FEATURE [Part::Box] Box379  label="Krychle379"
  AttacherType = Attacher::AttachEngine3D
  Height = 2
  Length = 6
  Placement = pos=(-18.3848,14.1421,-13) rot=(0,0,1;0.785398rad)
  Width = 6
FEATURE [Part::Cylinder] Cylinder1881  label="Válec1881"
  Angle = 360
  AttacherType = Attacher::AttachEngine3D
  Height = 15
  Placement = pos=(-26,-4e-15,-20) rot=(0,0,1;1.5708rad)
  Radius = 1.5
FEATURE [Part::Cylinder] Cylinder1882  label="Válec1882"
  Angle = 360
  AttacherType = Attacher::AttachEngine3D
  Height = 15
  Placement = pos=(0,26,-20) rot=(0,0,1;0rad)
  Radius = 1.5
FEATURE [Part::Cylinder] Cylinder1883  label="Válec1883"
  Angle = 360
  AttacherType = Attacher::AttachEngine3D
  Height = 15
  Placement = pos=(1.1e-14,-26,-20) rot=(0,0,1;3.14159rad)
  Radius = 1.5
FEATURE [Part::Compound] Compound592
  Links = -> [Cylinder1882,Cylinder1877,Cylinder1881,Cylinder1876,Cylinder1883,Cylinder1879,Cylinder1880,Cylinder1878]
  Placement = pos=(0,0,0) rot=(0,0,1;0.392699rad)
FEATURE [Part::Cut] Cut411
  Base = -> Tube013
  Tool = -> Compound592
FEATURE [Part::Box] Box380  label="Krychle380"
  AttacherType = Attacher::AttachEngine3D
  Height = 2
  Length = 6
  Placement = pos=(-14.1421,-18.3848,-13) rot=(0,0,1;2.35619rad)
  Width = 6
FEATURE [Part::Box] Box381  label="Krychle381"
  AttacherType = Attacher::AttachEngine3D
  Height = 2
  Length = 6
  Placement = pos=(-23,-3,-13) rot=(0,0,1;1.5708rad)
  Width = 6
FEATURE [Part::Box] Box382  label="Krychle382"
  AttacherType = Attacher::AttachEngine3D
  Height = 2
  Length = 6
  Placement = pos=(14.1421,18.3848,-13) rot=(0,0,-1;0.785398rad)
  Width = 6
FEATURE [Part::Box] Box383  label="Krychle383"
  AttacherType = Attacher::AttachEngine3D
  Height = 2
  Length = 6
  Placement = pos=(-3,23,-13) rot=(0,0,1;0rad)
  Width = 6
FEATURE [Part::Box] Box384  label="Krychle384"
  AttacherType = Attacher::AttachEngine3D
  Height = 2
  Length = 6
  Placement = pos=(18.3848,-14.1421,-13) rot=(0,0,1;3.92699rad)
  Width = 6
FEATURE [Part::Box] Box385  label="Krychle385"
  AttacherType = Attacher::AttachEngine3D
  Height = 2
  Length = 6
  Placement = pos=(3,-23,-13) rot=(0,0,1;3.14159rad)
  Width = 6
FEATURE [Part::Box] Box386  label="Krychle386"
  AttacherType = Attacher::AttachEngine3D
  Height = 2
  Length = 6
  Placement = pos=(23,3,-13) rot=(0,0,-1;1.5708rad)
  Width = 6
FEATURE [Part::Compound] Compound593
  Links = -> [Box379,Box381,Box380,Box385,Box384,Box386,Box382,Box383]
  Placement = pos=(0,0,0) rot=(0,0,1;0.392699rad)
FEATURE [Part::Cut] Cut412
  Base = -> Cut411
  Tool = -> Compound593
FEATURE [Part::Compound] Compound594  label="G-midi_monoblock_old"
  Links = -> [Cut408,Compound591,Cut412]
FEATURE [Mesh::Feature] Mesh007  label="G-midi_monoblock (Meshed)"
FEATURE [Part::Cylinder] Cylinder852  label="Válec852"
  Angle = 360
  AttacherType = Attacher::AttachEngine3D
  Height = 20
  Placement = pos=(-14.5,0,25) rot=(0,0,1;3.14159rad)
  Radius = 1.5
FEATURE [Part::Box] Box329  label="Krychle329"
  AttacherType = Attacher::AttachEngine3D
  Height = 60
  Length = 20
  Placement = pos=(-19.32,-5.18,0) rot=(0,0,1;0.314159rad)
  Width = 20
FEATURE [Part::Cylinder] Cylinder855  label="Válec855"
  Angle = 360
  AttacherType = Attacher::AttachEngine3D
  Height = 3
  Placement = pos=(7.25,12.5574,35) rot=(0,0,1;1.0472rad)
  Radius = 3
FEATURE [Part::Box] Box330  label="Krychle330"
  AttacherType = Attacher::AttachEngine3D
  Height = 60
  Length = 20
  Placement = pos=(0,0,0) rot=(0,0,-1;0.314159rad)
  Width = 20
FEATURE [Part::Cylinder] Cylinder850  label="Válec850"
  Angle = 360
  AttacherType = Attacher::AttachEngine3D
  Height = 8
  Placement = pos=(0,0,30) rot=(0,0,1;0rad)
  Radius = 21
FEATURE [Part::Cylinder] Cylinder854  label="Válec854"
  Angle = 360
  AttacherType = Attacher::AttachEngine3D
  Height = 3
  Placement = pos=(7.25,-12.5574,35) rot=(0,0,-1;1.0472rad)
  Radius = 3
FEATURE [Part::Cylinder] Cylinder856  label="Válec856"
  Angle = 360
  AttacherType = Attacher::AttachEngine3D
  Height = 3
  Placement = pos=(-14.5,0,35) rot=(0,0,1;3.14159rad)
  Radius = 3
FEATURE [Part::Compound] Compound558
  Links = -> [Cylinder854,Cylinder855,Cylinder856]
  Placement = pos=(0,0,10) rot=(0,0,1;0rad)
FEATURE [Part::Cylinder] Cylinder851  label="Válec851"
  Angle = 360
  AttacherType = Attacher::AttachEngine3D
  Height = 20
  Placement = pos=(7.25,12.5574,25) rot=(0,0,1;1.0472rad)
  Radius = 1.5
FEATURE [Part::Cylinder] Cylinder857  label="Válec857"
  Angle = 360
  AttacherType = Attacher::AttachEngine3D
  Height = 5
  Placement = pos=(14.4,0,30) rot=(0,0,1;0rad)
  Radius = 5
FEATURE [Part::Box] Box328  label="Krychle328"
  AttacherType = Attacher::AttachEngine3D
  Height = 60
  Length = 40
  Placement = pos=(-20,-20,0) rot=(0,0,1;0rad)
  Width = 20
FEATURE [Part::Cylinder] Cylinder849  label="Válec849"
  Angle = 360
  AttacherType = Attacher::AttachEngine3D
  Height = 60
  Placement = pos=(0,14.5,0) rot=(0,0,1;0rad)
  Radius = 1.5
FEATURE [Part::Cylinder] Cylinder853  label="Válec853"
  Angle = 360
  AttacherType = Attacher::AttachEngine3D
  Height = 20
  Placement = pos=(7.25,-12.5574,25) rot=(0,0,-1;1.0472rad)
  Radius = 1.5
FEATURE [Part::Compound] Compound559
  Links = -> [Cylinder851,Cylinder852,Cylinder853]
FEATURE [Part::Cut] Cut347
  Base = -> Cylinder850
  Tool = -> Compound559
FEATURE [Part::Cut] Cut346
  Base = -> Cut347
  Tool = -> Compound558
FEATURE [Part::FeaturePython] Tube050  # WARN: FeaturePython — macro-defined, semantics opaque (R4)
  AttacherType = Attacher::AttachEngine3D
  Height = 42
  InnerRadius = 11.5
  OuterRadius = 18
  Placement = pos=(0,0,10) rot=(0,0,1;0rad)
FEATURE [Part::Cut] Cut342
  Base = -> Tube050
  Tool = -> Cylinder849
FEATURE [Part::Cut] Cut343
  Base = -> Cut342
  Tool = -> Box329
FEATURE [Part::Cut] Cut341
  Base = -> Cut343
  Tool = -> Box330
FEATURE [Part::Cut] Cut344  label="gearovina_midi_vzperovina"
  Base = -> Cut341
  Placement = pos=(0,0,-2) rot=(0,0,-1;0.523599rad)
  Tool = -> Box328
FEATURE [Part::Cut] Cut348  label="gearovina_midi_vzperovina001"
  Base = -> Cut341
  Placement = pos=(0,0,-2) rot=(0,0,1;1.5708rad)
  Tool = -> Box328
FEATURE [Part::Cut] Cut349  label="gearovina_midi_vzperovina002"
  Base = -> Cut341
  Placement = pos=(0,0,-2) rot=(0,0,1;3.66519rad)
  Tool = -> Box328
FEATURE [Part::Cylinder] Cylinder858  label="Válec858"
  Angle = 360
  AttacherType = Attacher::AttachEngine3D
  Height = 5
  Placement = pos=(-7.2,12.4708,30) rot=(0,0,1;2.0944rad)
  Radius = 5
FEATURE [Part::Cylinder] Cylinder860  label="Válec860"
  Angle = 360
  AttacherType = Attacher::AttachEngine3D
  Height = 14
  Placement = pos=(0,0,30) rot=(0,0,1;0rad)
  Radius = 8
FEATURE [Part::Cylinder] Cylinder859  label="Válec859"
  Angle = 360
  AttacherType = Attacher::AttachEngine3D
  Height = 5
  Placement = pos=(-7.2,-12.4708,30) rot=(0,0,1;4.18879rad)
  Radius = 5
FEATURE [Part::Compound] Compound557
  Links = -> [Cylinder857,Cylinder858,Cylinder859,Cylinder860]
FEATURE [Part::Cut] Cut345
  Base = -> Cut346
  Placement = pos=(0,0,20) rot=(0,0,1;0rad)
  Tool = -> Compound557
FEATURE [Part::Compound] Compound560  label="gearovina_midi_vzeprena_pikovina"
  Links = -> [Cut348,Cut349,Cut345,Cut344]
FEATURE [Part::FeaturePython] Tube  # WARN: FeaturePython — macro-defined, semantics opaque (R4)
  AttacherType = Attacher::AttachEngine3D
  Height = 10
  InnerRadius = 17.5
  OuterRadius = 21
  Placement = pos=(0,0,58) rot=(0,0,1;0rad)
FEATURE [Part::FeaturePython] Tube051  # WARN: FeaturePython — macro-defined, semantics opaque (R4)
  AttacherType = Attacher::AttachEngine3D
  Height = 10
  InnerRadius = 8
  OuterRadius = 17.6
  Placement = pos=(0,0,58) rot=(0,0,1;0rad)
FEATURE [Part::Cylinder] Cylinder1884  label="Válec1884"
  Angle = 360
  AttacherType = Attacher::AttachEngine3D
  Height = 20
  Placement = pos=(7.25,-12.5574,35) rot=(0,0,-1;1.0472rad)
  Radius = 3
FEATURE [Part::Cylinder] Cylinder1885  label="Válec1885"
  Angle = 360
  AttacherType = Attacher::AttachEngine3D
  Height = 20
  Placement = pos=(7.25,12.5574,35) rot=(0,0,1;1.0472rad)
  Radius = 3
FEATURE [Part::Cylinder] Cylinder1886  label="Válec1886"
  Angle = 360
  AttacherType = Attacher::AttachEngine3D
  Height = 20
  Placement = pos=(-14.5,0,35) rot=(0,0,1;3.14159rad)
  Radius = 3
FEATURE [Part::Compound] Compound595
  Links = -> [Cylinder1884,Cylinder1885,Cylinder1886]
  Placement = pos=(0,0,30) rot=(0,0,1;0rad)
FEATURE [Part::Cylinder] Cylinder1887  label="Válec1887"
  Angle = 360
  AttacherType = Attacher::AttachEngine3D
  Height = 20
  Placement = pos=(7.25,-12.5574,35) rot=(0,0,-1;1.0472rad)
  Radius = 1.5
FEATURE [Part::Cylinder] Cylinder1888  label="Válec1888"
  Angle = 360
  AttacherType = Attacher::AttachEngine3D
  Height = 20
  Placement = pos=(7.25,12.5574,35) rot=(0,0,1;1.0472rad)
  Radius = 1.5
FEATURE [Part::Cylinder] Cylinder1889  label="Válec1889"
  Angle = 360
  AttacherType = Attacher::AttachEngine3D
  Height = 20
  Placement = pos=(-14.5,0,35) rot=(0,0,1;3.14159rad)
  Radius = 1.5
FEATURE [Part::Compound] Compound596
  Links = -> [Cylinder1887,Cylinder1888,Cylinder1889]
  Placement = pos=(0,0,20) rot=(0,0,1;0rad)
FEATURE [Part::Chamfer] Chamfer
  Base = -> Compound560
  Edges = 1 edges r=3.5: [Edge31]
FEATURE [Part::Cut] Cut413
  Base = -> Tube051
  Tool = -> Compound596
FEATURE [Part::FeaturePython] Tube052  # WARN: FeaturePython — macro-defined, semantics opaque (R4)
  AttacherType = Attacher::AttachEngine3D
  Height = 10
  InnerRadius = 8
  OuterRadius = 17.5
  Placement = pos=(0,0,58) rot=(0,0,1;0rad)
FEATURE [Part::FeaturePython] Tube053  # WARN: FeaturePython — macro-defined, semantics opaque (R4)
  AttacherType = Attacher::AttachEngine3D
  Height = 42
  InnerRadius = 11.5
  OuterRadius = 18
  Placement = pos=(0,0,10) rot=(0,0,1;0rad)
FEATURE [Part::Cylinder] Cylinder1890  label="Válec1890"
  Angle = 360
  AttacherType = Attacher::AttachEngine3D
  Height = 5
  Placement = pos=(-7.2,12.4708,30) rot=(0,0,1;2.0944rad)
  Radius = 5
FEATURE [Part::Cylinder] Cylinder1891  label="Válec1891"
  Angle = 360
  AttacherType = Attacher::AttachEngine3D
  Height = 14
  Placement = pos=(0,0,30) rot=(0,0,1;0rad)
  Radius = 8
FEATURE [Part::Cylinder] Cylinder1892  label="Válec1892"
  Angle = 360
  AttacherType = Attacher::AttachEngine3D
  Height = 8
  Placement = pos=(0,0,30) rot=(0,0,1;0rad)
  Radius = 21
FEATURE [Part::Cylinder] Cylinder1893  label="Válec1893"
  Angle = 360
  AttacherType = Attacher::AttachEngine3D
  Height = 5
  Placement = pos=(14.4,0,30) rot=(0,0,1;0rad)
  Radius = 5
FEATURE [Part::Cylinder] Cylinder1894  label="Válec1894"
  Angle = 360
  AttacherType = Attacher::AttachEngine3D
  Height = 20
  Placement = pos=(7.25,12.5574,25) rot=(0,0,1;1.0472rad)
  Radius = 1.5
FEATURE [Part::Cylinder] Cylinder1895  label="Válec1895"
  Angle = 360
  AttacherType = Attacher::AttachEngine3D
  Height = 60
  Placement = pos=(0,14.5,0) rot=(0,0,1;0rad)
  Radius = 1.5
FEATURE [Part::Cut] Cut417
  Base = -> Tube053
  Tool = -> Cylinder1895
FEATURE [Part::Box] Box387  label="Krychle387"
  AttacherType = Attacher::AttachEngine3D
  Height = 60
  Length = 40
  Placement = pos=(-20,-20,0) rot=(0,0,1;0rad)
  Width = 20
FEATURE [Part::Cylinder] Cylinder1896  label="Válec1896"
  Angle = 360
  AttacherType = Attacher::AttachEngine3D
  Height = 20
  Placement = pos=(7.25,-12.5574,25) rot=(0,0,-1;1.0472rad)
  Radius = 1.5
FEATURE [Part::Cylinder] Cylinder1897  label="Válec1897"
  Angle = 360
  AttacherType = Attacher::AttachEngine3D
  Height = 20
  Placement = pos=(-14.5,0,25) rot=(0,0,1;3.14159rad)
  Radius = 1.5
FEATURE [Part::Compound] Compound600
  Links = -> [Cylinder1894,Cylinder1897,Cylinder1896]
FEATURE [Part::Cut] Cut424
  Base = -> Cylinder1892
  Tool = -> Compound600
FEATURE [Part::Box] Box388  label="Krychle388"
  AttacherType = Attacher::AttachEngine3D
  Height = 60
  Length = 20
  Placement = pos=(-19.32,-5.18,0) rot=(0,0,1;0.314159rad)
  Width = 20
FEATURE [Part::Cut] Cut422
  Base = -> Cut417
  Tool = -> Box388
FEATURE [Part::Box] Box389  label="Krychle389"
  AttacherType = Attacher::AttachEngine3D
  Height = 60
  Length = 20
  Placement = pos=(0,0,0) rot=(0,0,-1;0.314159rad)
  Width = 20
FEATURE [Part::Cut] Cut416
  Base = -> Cut422
  Tool = -> Box389
FEATURE [Part::Cut] Cut418  label="gearovina_midi_vzperovina003"
  Base = -> Cut416
  Placement = pos=(0,0,-2) rot=(0,0,1;1.5708rad)
  Tool = -> Box387
FEATURE [Part::Cut] Cut419  label="gearovina_midi_vzperovina004"
  Base = -> Cut416
  Placement = pos=(0,0,-2) rot=(0,0,1;3.66519rad)
  Tool = -> Box387
FEATURE [Part::Cut] Cut423  label="gearovina_midi_vzperovina005"
  Base = -> Cut416
  Placement = pos=(0,0,-2) rot=(0,0,-1;0.523599rad)
  Tool = -> Box387
FEATURE [Part::Cylinder] Cylinder1898  label="Válec1898"
  Angle = 360
  AttacherType = Attacher::AttachEngine3D
  Height = 3
  Placement = pos=(7.25,-12.5574,35) rot=(0,0,-1;1.0472rad)
  Radius = 3
FEATURE [Part::Cylinder] Cylinder1899  label="Válec1899"
  Angle = 360
  AttacherType = Attacher::AttachEngine3D
  Height = 3
  Placement = pos=(7.25,12.5574,35) rot=(0,0,1;1.0472rad)
  Radius = 3
FEATURE [Part::Cylinder] Cylinder1900  label="Válec1900"
  Angle = 360
  AttacherType = Attacher::AttachEngine3D
  Height = 3
  Placement = pos=(-14.5,0,35) rot=(0,0,1;3.14159rad)
  Radius = 3
FEATURE [Part::Compound] Compound599
  Links = -> [Cylinder1898,Cylinder1899,Cylinder1900]
  Placement = pos=(0,0,10) rot=(0,0,1;0rad)
FEATURE [Part::Cut] Cut420
  Base = -> Cut424
  Tool = -> Compound599
FEATURE [Part::Cylinder] Cylinder1901  label="Válec1901"
  Angle = 360
  AttacherType = Attacher::AttachEngine3D
  Height = 5
  Placement = pos=(-7.2,-12.4708,30) rot=(0,0,1;4.18879rad)
  Radius = 5
FEATURE [Part::Compound] Compound601
  Links = -> [Cylinder1893,Cylinder1890,Cylinder1901,Cylinder1891]
FEATURE [Part::Cut] Cut421
  Base = -> Cut420
  Placement = pos=(0,0,20) rot=(0,0,1;0rad)
  Tool = -> Compound601
FEATURE [Part::Compound] Compound602  label="gearovina_midi_vzeprena_pikovina001"
  Links = -> [Cut418,Cut419,Cut421,Cut423]
FEATURE [Part::Cylinder] Cylinder1902  label="Válec1902"
  Angle = 360
  AttacherType = Attacher::AttachEngine3D
  Height = 20
  Placement = pos=(7.25,12.5574,35) rot=(0,0,1;1.0472rad)
  Radius = 1.5
FEATURE [Part::Cylinder] Cylinder1903  label="Válec1903"
  Angle = 360
  AttacherType = Attacher::AttachEngine3D
  Height = 20
  Placement = pos=(7.25,-12.5574,35) rot=(0,0,-1;1.0472rad)
  Radius = 1.5
FEATURE [Part::Cylinder] Cylinder1904  label="Válec1904"
  Angle = 360
  AttacherType = Attacher::AttachEngine3D
  Height = 20
  Placement = pos=(7.25,-12.5574,35) rot=(0,0,-1;1.0472rad)
  Radius = 3
FEATURE [Part::Cylinder] Cylinder1905  label="Válec1905"
  Angle = 360
  AttacherType = Attacher::AttachEngine3D
  Height = 20
  Placement = pos=(7.25,12.5574,35) rot=(0,0,1;1.0472rad)
  Radius = 3
FEATURE [Part::Cylinder] Cylinder1906  label="Válec1906"
  Angle = 360
  AttacherType = Attacher::AttachEngine3D
  Height = 20
  Placement = pos=(-14.5,0,35) rot=(0,0,1;3.14159rad)
  Radius = 3
FEATURE [Part::Cylinder] Cylinder1907  label="Válec1907"
  Angle = 360
  AttacherType = Attacher::AttachEngine3D
  Height = 20
  Placement = pos=(-14.5,0,35) rot=(0,0,1;3.14159rad)
  Radius = 1.5
FEATURE [Part::Compound] Compound598
  Links = -> [Cylinder1903,Cylinder1902,Cylinder1907]
  Placement = pos=(0,0,20) rot=(0,0,1;0rad)
FEATURE [Part::Compound] Compound603
  Links = -> [Cylinder1904,Cylinder1905,Cylinder1906]
  Placement = pos=(0,0,30) rot=(0,0,1;0rad)
FEATURE [Part::Cut] Cut425
  Base = -> Tube052
  Tool = -> Compound598
FEATURE [Part::Cut] Cut415
  Base = -> Cut425
  Tool = -> Compound603
FEATURE [Part::Chamfer] Chamfer001
  Base = -> Compound602
  Edges = 1 edges r=3.5: [Edge31]
FEATURE [Part::Compound] Compound604  label="G-midi_pikovina_rot"
  Links = -> [Cut415,Chamfer001]
  Placement = pos=(0,0,39) rot=(1,0,0;3.14159rad)
FEATURE [Part::FeaturePython] Tube054  label="HK-3512"  # WARN: FeaturePython — macro-defined, semantics opaque (R4)
  AttacherType = Attacher::AttachEngine3D
  Height = 12
  InnerRadius = 17.5
  OuterRadius = 21
  Placement = pos=(0,0,-31) rot=(0,0,1;0rad)
FEATURE [Part::FeaturePython] Tube034  # WARN: FeaturePython — macro-defined, semantics opaque (R4)
  AttacherType = Attacher::AttachEngine3D
  Height = 4
  InnerRadius = 23
  OuterRadius = 29
  Placement = pos=(0,0,-22) rot=(0,0,1;0rad)
FEATURE [Part::Cylinder] Cylinder783  label="Válec783"
  Angle = 360
  AttacherType = Attacher::AttachEngine3D
  Height = 10
  Placement = pos=(-26,-4e-15,-24) rot=(0,0,1;1.5708rad)
  Radius = 1.5
FEATURE [Part::Cylinder] Cylinder782  label="Válec782"
  Angle = 360
  AttacherType = Attacher::AttachEngine3D
  Height = 10
  Placement = pos=(-18.3848,18.3848,-24) rot=(0,0,1;0.785398rad)
  Radius = 1.5
FEATURE [Part::Cylinder] Cylinder786  label="Válec786"
  Angle = 360
  AttacherType = Attacher::AttachEngine3D
  Height = 10
  Placement = pos=(1.1e-14,-26,-24) rot=(0,0,1;3.14159rad)
  Radius = 1.5
FEATURE [Part::Cylinder] Cylinder785  label="Válec785"
  Angle = 360
  AttacherType = Attacher::AttachEngine3D
  Height = 10
  Placement = pos=(-18.3848,-18.3848,-24) rot=(0,0,1;2.35619rad)
  Radius = 1.5
FEATURE [Part::Cylinder] Cylinder789  label="Válec789"
  Angle = 360
  AttacherType = Attacher::AttachEngine3D
  Height = 10
  Placement = pos=(18.3848,18.3848,-24) rot=(0,0,-1;0.785398rad)
  Radius = 1.5
FEATURE [Part::Cylinder] Cylinder784  label="Válec784"
  Angle = 360
  AttacherType = Attacher::AttachEngine3D
  Height = 10
  Placement = pos=(0,26,-24) rot=(0,0,1;0rad)
  Radius = 1.5
FEATURE [Part::Cylinder] Cylinder788  label="Válec788"
  Angle = 360
  AttacherType = Attacher::AttachEngine3D
  Height = 10
  Placement = pos=(26,1e-14,-24) rot=(0,0,-1;1.5708rad)
  Radius = 1.5
FEATURE [Part::Cylinder] Cylinder787  label="Válec787"
  Angle = 360
  AttacherType = Attacher::AttachEngine3D
  Height = 10
  Placement = pos=(18.3848,-18.3848,-24) rot=(0,0,1;3.92699rad)
  Radius = 1.5
FEATURE [Part::Compound] Compound537
  Links = -> [Cylinder784,Cylinder782,Cylinder783,Cylinder785,Cylinder786,Cylinder787,Cylinder788,Cylinder789]
  Placement = pos=(0,0,0) rot=(0,0,1;0.392699rad)
FEATURE [Part::Cut] Cut310  label="under-moto"
  Base = -> Tube034
  Placement = pos=(0,0,2) rot=(0,0,1;0rad)
  Tool = -> Compound537
FEATURE [Part::Cylinder] Cylinder1908  label="Válec1908"
  Angle = 360
  AttacherType = Attacher::AttachEngine3D
  Height = 20
  Placement = pos=(-26,-4e-15,-24) rot=(0,0,1;1.5708rad)
  Radius = 1.5
FEATURE [Part::Cylinder] Cylinder1909  label="Válec1909"
  Angle = 360
  AttacherType = Attacher::AttachEngine3D
  Height = 20
  Placement = pos=(-18.3848,18.3848,-24) rot=(0,0,1;0.785398rad)
  Radius = 1.5
FEATURE [Part::Cylinder] Cylinder1910  label="Válec1910"
  Angle = 360
  AttacherType = Attacher::AttachEngine3D
  Height = 20
  Placement = pos=(18.3848,-18.3848,-24) rot=(0,0,1;3.92699rad)
  Radius = 1.5
FEATURE [Part::Cylinder] Cylinder1911  label="Válec1911"
  Angle = 360
  AttacherType = Attacher::AttachEngine3D
  Height = 20
  Placement = pos=(18.3848,18.3848,-24) rot=(0,0,-1;0.785398rad)
  Radius = 1.5
FEATURE [Part::Cylinder] Cylinder1912  label="Válec1912"
  Angle = 360
  AttacherType = Attacher::AttachEngine3D
  Height = 20
  Placement = pos=(1.1e-14,-26,-24) rot=(0,0,1;3.14159rad)
  Radius = 1.5
FEATURE [Part::Cylinder] Cylinder1913  label="Válec1913"
  Angle = 360
  AttacherType = Attacher::AttachEngine3D
  Height = 20
  Placement = pos=(0,26,-24) rot=(0,0,1;0rad)
  Radius = 1.5
FEATURE [Part::Cylinder] Cylinder1914  label="Válec1914"
  Angle = 360
  AttacherType = Attacher::AttachEngine3D
  Height = 20
  Placement = pos=(-18.3848,-18.3848,-24) rot=(0,0,1;2.35619rad)
  Radius = 1.5
FEATURE [Part::Cylinder] Cylinder1915  label="Válec1915"
  Angle = 360
  AttacherType = Attacher::AttachEngine3D
  Height = 20
  Placement = pos=(26,1e-14,-24) rot=(0,0,-1;1.5708rad)
  Radius = 1.5
FEATURE [Part::Compound] Compound605
  Links = -> [Cylinder1913,Cylinder1909,Cylinder1908,Cylinder1914,Cylinder1912,Cylinder1910,Cylinder1915,Cylinder1911]
  Placement = pos=(0,0,0) rot=(0,0,1;0.392699rad)
FEATURE [Part::FeaturePython] Tube055  # WARN: FeaturePython — macro-defined, semantics opaque (R4)
  AttacherType = Attacher::AttachEngine3D
  Height = 11
  InnerRadius = 21.2
  OuterRadius = 29
  Placement = pos=(0,0,-22) rot=(0,0,1;0rad)
FEATURE [Part::Cut] Cut426  label="under-moto001"
  Base = -> Tube055
  Placement = pos=(0,0,-9) rot=(0,0,1;0rad)
  Tool = -> Compound605
FEATURE [Part::Chamfer] Chamfer002
  Base = -> Cut413
  Edges = 1 edges r=1: [Edge1]
FEATURE [Part::Cut] Cut427
  Base = -> Chamfer002
  Tool = -> Compound595
FEATURE [Mesh::Feature] Mesh009  label="G-midi_pikovina (Meshed)"
FEATURE [Part::Cylinder] Cylinder755  label="Válec755"
  Angle = 360
  AttacherType = Attacher::AttachEngine3D
  Height = 20
  Placement = pos=(-23.55,23.55,-34) rot=(0,0,1;0rad)
  Radius = 2.5
FEATURE [Part::Box] Box312  label="Krychle312"
  AttacherType = Attacher::AttachEngine3D
  Height = 40
  Length = 56.5
  Placement = pos=(-28.25,-28.25,32) rot=(0,0,1;0rad)
  Width = 56.5
FEATURE [Part::Box] Box311  label="Krychle311"
  AttacherType = Attacher::AttachEngine3D
  Height = 9
  Length = 64
  Placement = pos=(-32,-34,32) rot=(0,0,1;0rad)
  Width = 68
FEATURE [Part::Cut] Cut304
  Base = -> Box311
  Tool = -> Box312
FEATURE [Part::Compound] Compound529  label="hrubo_holder020"
  Links = -> [Cut304]
FEATURE [Part::Compound] Compound528  label="hrubo_holder019"
  Links = -> [Compound529]
FEATURE [Part::Box] Box313  label="Krychle313"
  AttacherType = Attacher::AttachEngine3D
  Height = 20
  Length = 28.8
  Placement = pos=(-14.4,-8,34) rot=(0,0,1;0rad)
  Width = 43.38
FEATURE [Part::Cut] Cut305
  Base = -> Compound528
  Placement = pos=(-29,18,30) rot=(0,0,1;0rad)
  Tool = -> Box313
FEATURE [Part::Box] Box306  label="Krychle306"
  AttacherType = Attacher::AttachEngine3D
  Height = 3
  Length = 20
  Placement = pos=(17.55,-27.55,-28) rot=(0,0,1;0rad)
  Width = 8
FEATURE [Part::Box] Box308  label="Krychle308"
  AttacherType = Attacher::AttachEngine3D
  Height = 3
  Length = 20
  Placement = pos=(17.55,19.55,-28) rot=(0,0,1;0rad)
  Width = 8
FEATURE [Part::Box] Box309  label="Krychle309"
  AttacherType = Attacher::AttachEngine3D
  Height = 3
  Length = 20
  Placement = pos=(-37.45,19.55,-28) rot=(0,0,1;0rad)
  Width = 8
FEATURE [Part::Box] Box310  label="Krychle310"
  AttacherType = Attacher::AttachEngine3D
  Height = 8
  Length = 68
  Placement = pos=(-34,-32,-30) rot=(0,0,1;0rad)
  Width = 64
FEATURE [Part::Cylinder] Cylinder753  label="Válec753"
  Angle = 360
  AttacherType = Attacher::AttachEngine3D
  Height = 20
  Placement = pos=(23.55,-23.55,-34) rot=(0,0,1;0rad)
  Radius = 2.5
FEATURE [Part::Cylinder] Cylinder754  label="Válec754"
  Angle = 360
  AttacherType = Attacher::AttachEngine3D
  Height = 20
  Placement = pos=(-23.55,-23.55,-34) rot=(0,0,1;0rad)
  Radius = 2.5
FEATURE [Part::Cylinder] Cylinder756  label="Válec756"
  Angle = 360
  AttacherType = Attacher::AttachEngine3D
  Height = 20
  Placement = pos=(23.55,23.55,-34) rot=(0,0,1;0rad)
  Radius = 2.5
FEATURE [Part::Compound] Compound527
  Links = -> [Cylinder756,Cylinder755,Cylinder754,Cylinder753]
FEATURE [Part::Cylinder] Cylinder757  label="Válec757"
  Angle = 360
  AttacherType = Attacher::AttachEngine3D
  Height = 20
  Placement = pos=(0,0,-39) rot=(0,0,1;0rad)
  Radius = 12
FEATURE [Part::Box] Box307  label="Krychle307"
  AttacherType = Attacher::AttachEngine3D
  Height = 3
  Length = 20
  Placement = pos=(-37.45,-27.55,-28) rot=(0,0,1;0rad)
  Width = 8
FEATURE [Part::Compound] Compound526
  Links = -> [Box308,Box306,Box309,Box307]
FEATURE [Part::Cut] Cut301
  Base = -> Box310
  Tool = -> Compound526
FEATURE [Part::Cut] Cut302
  Base = -> Cut301
  Tool = -> Compound527
FEATURE [Part::Cut] Cut303
  Base = -> Cut302
  Tool = -> Cylinder757
FEATURE [Part::Compound] Compound530
  Links = -> [Cut305]
  Placement = pos=(18,-29,32) rot=(0.707107,-0.707107,0;3.14159rad)
FEATURE [Part::Cylinder] Cylinder765  label="Válec765"
  Angle = 360
  AttacherType = Attacher::AttachEngine3D
  Height = 20
  Placement = pos=(-24.0209,-9.94977,-32) rot=(0,0,1;1.96349rad)
  Radius = 1.5
FEATURE [Part::Cylinder] Cylinder760  label="Válec760"
  Angle = 360
  AttacherType = Attacher::AttachEngine3D
  Height = 20
  Placement = pos=(-9.94977,24.0209,-32) rot=(0,0,1;0.392699rad)
  Radius = 1.5
FEATURE [Part::Cylinder] Cylinder764  label="Válec764"
  Angle = 360
  AttacherType = Attacher::AttachEngine3D
  Height = 20
  Placement = pos=(-24.0209,9.94977,-32) rot=(0,0,1;1.1781rad)
  Radius = 1.5
FEATURE [Part::Cylinder] Cylinder774  label="Válec774"
  Angle = 360
  AttacherType = Attacher::AttachEngine3D
  Height = 3
  Placement = pos=(9.95,-24.02,-30) rot=(0,0,1;3.53429rad)
  Radius = 3
FEATURE [Part::Cylinder] Cylinder781  label="Válec781"
  Angle = 360
  AttacherType = Attacher::AttachEngine3D
  Height = 20
  Placement = pos=(-15.75,10.48,-35) rot=(0,0,1;0rad)
  Radius = 2
FEATURE [Part::Cylinder] Cylinder771  label="Válec771"
  Angle = 360
  AttacherType = Attacher::AttachEngine3D
  Height = 3
  Placement = pos=(-24.0204,9.94899,-30) rot=(0,0,1;1.1781rad)
  Radius = 3
FEATURE [Part::Cylinder] Cylinder768  label="Válec768"
  Angle = 360
  AttacherType = Attacher::AttachEngine3D
  Height = 20
  Placement = pos=(24.0209,-9.94977,-32) rot=(0,0,-1;1.96349rad)
  Radius = 1.5
FEATURE [Part::Cylinder] Cylinder759  label="Válec759"
  Angle = 360
  AttacherType = Attacher::AttachEngine3D
  Height = 3
  Placement = pos=(-9.95,24.02,-30) rot=(0,0,1;0.392699rad)
  Radius = 3
FEATURE [Part::Cylinder] Cylinder776  label="Válec776"
  Angle = 360
  AttacherType = Attacher::AttachEngine3D
  Height = 3
  Placement = pos=(24.02,9.95,-30) rot=(0,0,-1;1.1781rad)
  Radius = 3
FEATURE [Part::Cylinder] Cylinder769  label="Válec769"
  Angle = 360
  AttacherType = Attacher::AttachEngine3D
  Height = 20
  Placement = pos=(24.0209,9.94977,-32) rot=(0,0,-1;1.1781rad)
  Radius = 1.5
FEATURE [Part::Cylinder] Cylinder772  label="Válec772"
  Angle = 360
  AttacherType = Attacher::AttachEngine3D
  Height = 3
  Placement = pos=(-24.02,-9.95,-30) rot=(0,0,1;1.96349rad)
  Radius = 3
FEATURE [Part::Cylinder] Cylinder766  label="Válec766"
  Angle = 360
  AttacherType = Attacher::AttachEngine3D
  Height = 20
  Placement = pos=(-9.94977,-24.0209,-32) rot=(0,0,1;2.74889rad)
  Radius = 1.5
FEATURE [Part::Cylinder] Cylinder767  label="Válec767"
  Angle = 360
  AttacherType = Attacher::AttachEngine3D
  Height = 20
  Placement = pos=(9.94977,-24.0209,-32) rot=(0,0,1;3.53429rad)
  Radius = 1.5
FEATURE [Part::Cylinder] Cylinder770  label="Válec770"
  Angle = 360
  AttacherType = Attacher::AttachEngine3D
  Height = 20
  Placement = pos=(9.94977,24.0209,-32) rot=(0,0,-1;0.392699rad)
  Radius = 1.5
FEATURE [Part::Compound] Compound532
  Links = -> [Cylinder760,Cylinder764,Cylinder765,Cylinder766,Cylinder767,Cylinder768,Cylinder769,Cylinder770]
FEATURE [Part::Cut] Cut307
  Base = -> Cut303
  Tool = -> Compound532
FEATURE [Part::Cylinder] Cylinder773  label="Válec773"
  Angle = 360
  AttacherType = Attacher::AttachEngine3D
  Height = 3
  Placement = pos=(-9.94899,-24.0204,-30) rot=(0,0,1;2.74889rad)
  Radius = 3
FEATURE [Part::Cylinder] Cylinder775  label="Válec775"
  Angle = 360
  AttacherType = Attacher::AttachEngine3D
  Height = 3
  Placement = pos=(24.0204,-9.94899,-30) rot=(0,0,-1;1.96349rad)
  Radius = 3
FEATURE [Part::Cylinder] Cylinder777  label="Válec777"
  Angle = 360
  AttacherType = Attacher::AttachEngine3D
  Height = 3
  Placement = pos=(9.94899,24.0204,-30) rot=(0,0,-1;0.392699rad)
  Radius = 3
FEATURE [Part::Compound] Compound533
  Links = -> [Cylinder759,Cylinder771,Cylinder772,Cylinder773,Cylinder774,Cylinder775,Cylinder776,Cylinder777]
FEATURE [Part::Cut] Cut308
  Base = -> Cut307
  Tool = -> Compound533
FEATURE [Part::Cylinder] Cylinder780  label="Válec780"
  Angle = 360
  AttacherType = Attacher::AttachEngine3D
  Height = 20
  Placement = pos=(-15.75,-10.48,-35) rot=(0,0,1;0rad)
  Radius = 2
FEATURE [Part::Compound] Compound534
  Links = -> [Cylinder780,Cylinder781]
FEATURE [Part::Cut] Cut309
  Base = -> Cut308
  Tool = -> Compound534
FEATURE [Part::Box] Box315  label="Krychle315"
  AttacherType = Attacher::AttachEngine3D
  Height = 61
  Length = 32
  Placement = pos=(-16,28.25,-83) rot=(0,0,1;0rad)
  Width = 6
FEATURE [Part::Compound] Compound535
  Links = -> [Cut309,Box315]
FEATURE [Part::Compound] Compound536  label="gearovina_midi_motohold_hrubo"
  Links = -> [Compound530,Compound535]
FEATURE [Part::Chamfer] Chamfer003
  Base = -> Compound536
  Edges = 4 edges r=4: [Edge3,Edge18,Edge37,Edge40]
FEATURE [Part::Chamfer] Chamfer004
  Base = -> Chamfer003
  Edges = 4 edges r=4: [Edge2,Edge21,Edge117,Edge118]
FEATURE [Part::Chamfer] Chamfer005
  Base = -> Chamfer004
  Edges = 2 edges r=2: [Edge6,Edge10]
FEATURE [Part::Chamfer] Chamfer006
  Base = -> Chamfer005
  Edges = 2 edges r=1: [Edge4,Edge16]
FEATURE [Part::Chamfer] Chamfer007
  Base = -> Chamfer006
  Edges = 2 edges r=8: [Edge217,Edge221]
FEATURE [Part::Chamfer] Chamfer008  label="gearovina_midi_motohold2"
  Base = -> Chamfer007
  Edges = 2 edges r=2: [Edge3,Edge15]
FEATURE [Part::Chamfer] Chamfer009  label="G-midi_motohold"
  Base = -> Chamfer008
  Edges = 1 edges r=2: [Edge38]
  Placement = pos=(0,0,-15) rot=(0,0,1;0rad)
FEATURE [Part::Compound] Compound607  label="G-midi_undermotor"
  Links = -> [Cut310,Cut426]
FEATURE [Part::Cylinder] Cylinder827  label="Válec827"
  Angle = 360
  AttacherType = Attacher::AttachEngine3D
  Height = 5
  Placement = pos=(-7.2,12.4708,30) rot=(0,0,1;2.0944rad)
  Radius = 5
FEATURE [Part::Cylinder] Cylinder825  label="Válec825"
  Angle = 360
  AttacherType = Attacher::AttachEngine3D
  Height = 8
  Placement = pos=(0,0,30) rot=(0,0,1;0rad)
  Radius = 21
FEATURE [Part::Cylinder] Cylinder826  label="Válec826"
  Angle = 360
  AttacherType = Attacher::AttachEngine3D
  Height = 5
  Placement = pos=(14.4,0,30) rot=(0,0,1;0rad)
  Radius = 5
FEATURE [Part::FeaturePython] Tube046  # WARN: FeaturePython — macro-defined, semantics opaque (R4)
  AttacherType = Attacher::AttachEngine3D
  Height = 1
  InnerRadius = 7
  OuterRadius = 8
  Placement = pos=(0,0,35) rot=(0,0,1;0rad)
FEATURE [Part::FeaturePython] Tube049  # WARN: FeaturePython — macro-defined, semantics opaque (R4)
  AttacherType = Attacher::AttachEngine3D
  Height = 1
  InnerRadius = 4
  OuterRadius = 5
  Placement = pos=(-7.2,-12.47,34) rot=(0,0,1;4.18879rad)
FEATURE [Part::FeaturePython] Tube048  # WARN: FeaturePython — macro-defined, semantics opaque (R4)
  AttacherType = Attacher::AttachEngine3D
  Height = 1
  InnerRadius = 4
  OuterRadius = 5
  Placement = pos=(-7.2,12.47,34) rot=(0,0,1;2.0944rad)
FEATURE [Part::FeaturePython] Tube047  # WARN: FeaturePython — macro-defined, semantics opaque (R4)
  AttacherType = Attacher::AttachEngine3D
  Height = 1
  InnerRadius = 4
  OuterRadius = 5
  Placement = pos=(14.4,0,34) rot=(0,0,1;0rad)
FEATURE [Part::Compound] Compound551
  Links = -> [Tube046,Tube047,Tube048,Tube049]
FEATURE [Part::Cylinder] Cylinder832  label="Válec832"
  Angle = 360
  AttacherType = Attacher::AttachEngine3D
  Height = 3
  Placement = pos=(-14.5,0,35) rot=(0,0,1;3.14159rad)
  Radius = 3
FEATURE [Part::Cylinder] Cylinder831  label="Válec831"
  Angle = 360
  AttacherType = Attacher::AttachEngine3D
  Height = 20
  Placement = pos=(-14.5,0,25) rot=(0,0,1;3.14159rad)
  Radius = 1.5
FEATURE [Part::Cylinder] Cylinder828  label="Válec828"
  Angle = 360
  AttacherType = Attacher::AttachEngine3D
  Height = 5
  Placement = pos=(-7.2,-12.4708,30) rot=(0,0,1;4.18879rad)
  Radius = 5
FEATURE [Part::Cylinder] Cylinder835  label="Válec835"
  Angle = 360
  AttacherType = Attacher::AttachEngine3D
  Height = 3
  Placement = pos=(7.25,-12.5574,35) rot=(0,0,-1;1.0472rad)
  Radius = 3
FEATURE [Part::Cylinder] Cylinder829  label="Válec829"
  Angle = 360
  AttacherType = Attacher::AttachEngine3D
  Height = 6
  Placement = pos=(0,0,30) rot=(0,0,1;0rad)
  Radius = 8
FEATURE [Part::Compound] Compound550
  Links = -> [Cylinder826,Cylinder827,Cylinder828,Cylinder829]
FEATURE [Part::Cylinder] Cylinder836  label="Válec836"
  Angle = 360
  AttacherType = Attacher::AttachEngine3D
  Height = 3
  Placement = pos=(7.25,12.5574,35) rot=(0,0,1;1.0472rad)
  Radius = 3
FEATURE [Part::Compound] Compound552
  Links = -> [Cylinder835,Cylinder836,Cylinder832]
FEATURE [Part::Cylinder] Cylinder833  label="Válec833"
  Angle = 360
  AttacherType = Attacher::AttachEngine3D
  Height = 20
  Placement = pos=(7.25,-12.5574,25) rot=(0,0,-1;1.0472rad)
  Radius = 1.5
FEATURE [Part::Cylinder] Cylinder834  label="Válec834"
  Angle = 360
  AttacherType = Attacher::AttachEngine3D
  Height = 20
  Placement = pos=(7.25,12.5574,25) rot=(0,0,1;1.0472rad)
  Radius = 1.5
FEATURE [Part::Compound] Compound553
  Links = -> [Cylinder834,Cylinder831,Cylinder833]
FEATURE [Part::Cut] Cut329
  Base = -> Cylinder825
  Tool = -> Compound553
FEATURE [Part::Cut] Cut330
  Base = -> Cut329
  Tool = -> Compound552
FEATURE [Part::Cut] Cut331
  Base = -> Cut330
  Tool = -> Compound550
FEATURE [Part::Compound] Compound554  label="G-midi_quikovina1"
  Links = -> [Compound551,Cut331]
  Placement = pos=(0,0,50) rot=(0,0,1;0rad)
FEATURE [Part::FeaturePython] Tube056  label="6002-2RS"  # WARN: FeaturePython — macro-defined, semantics opaque (R4)
  AttacherType = Attacher::AttachEngine3D
  Height = 9
  InnerRadius = 7.5
  OuterRadius = 16
  Placement = pos=(0,0,88) rot=(0,0,1;0rad)
FEATURE [Part::FeaturePython] Tube057  label="6001-2RS"  # WARN: FeaturePython — macro-defined, semantics opaque (R4)
  AttacherType = Attacher::AttachEngine3D
  Height = 8
  InnerRadius = 6
  OuterRadius = 14
  Placement = pos=(0,0,88) rot=(0,0,1;0rad)
FEATURE [Part::Cylinder] Cylinder1916  label="Válec1916"
  Angle = 360
  AttacherType = Attacher::AttachEngine3D
  Height = 8
  Placement = pos=(0,0,88) rot=(0,0,1;0rad)
  Radius = 6
FEATURE [Part::Chamfer] Chamfer010
  Base = -> Cylinder1916
  Edges = 1 edges r=1: [Edge1]
FEATURE [Part::Chamfer] Chamfer011
  Base = -> Compound554
  Edges = 1 edges r=1: [Edge25]
FEATURE [Part::FeaturePython] Tube058  # WARN: FeaturePython — macro-defined, semantics opaque (R4)
  AttacherType = Attacher::AttachEngine3D
  Height = 1
  InnerRadius = 4
  OuterRadius = 5
  Placement = pos=(14.4,0,34) rot=(0,0,1;0rad)
FEATURE [Part::FeaturePython] Tube059  # WARN: FeaturePython — macro-defined, semantics opaque (R4)
  AttacherType = Attacher::AttachEngine3D
  Height = 1
  InnerRadius = 4
  OuterRadius = 5
  Placement = pos=(-7.2,12.47,34) rot=(0,0,1;2.0944rad)
FEATURE [Part::FeaturePython] Tube060  # WARN: FeaturePython — macro-defined, semantics opaque (R4)
  AttacherType = Attacher::AttachEngine3D
  Height = 1
  InnerRadius = 4
  OuterRadius = 5
  Placement = pos=(-7.2,-12.47,34) rot=(0,0,1;4.18879rad)
FEATURE [Part::Compound] Compound609  label="G-midi_washers"
  Links = -> [Tube058,Tube059,Tube060]
  Placement = pos=(0,0,20) rot=(0,0,1;0rad)
FEATURE [Part::Compound] Compound606  label="G-midi_pikovina"
  Links = -> [Chamfer,Cut427,Compound609]
FEATURE [Part::FeaturePython] Tube061  # WARN: FeaturePython — macro-defined, semantics opaque (R4)
  AttacherType = Attacher::AttachEngine3D
  Height = 1
  InnerRadius = 6
  OuterRadius = 8
  Placement = pos=(0,0,88) rot=(0,0,1;0rad)
FEATURE [Part::Compound] Compound608  label="G-midi_quikovina"
  Links = -> [Chamfer010,Chamfer011,Tube061]
FEATURE [Part::Compound] Compound610  label="G-midi_outer-gear002"
  Links = -> [Cylinder1853,Cut406,Cut404,Cut403,Cut405]
  Placement = pos=(0,0,0) rot=(0,0,1;2.0944rad)
FEATURE [Part::Compound] Compound611  label="G-midi_outer-gear003"
  Links = -> [Cylinder1853,Cut406,Cut404,Cut403,Cut405]
  Placement = pos=(0,0,0) rot=(0,0,1;2.0944rad)
FEATURE [Part::Compound] Compound612  label="G-midi_outer-gear004"
  Links = -> [Cylinder1853,Cut406,Cut404,Cut403,Cut405]
  Placement = pos=(0,0,0) rot=(0,0,1;4.18879rad)
FEATURE [Part::Compound] Compound613  label="G-midi_outer-gear005"
  Links = -> [Cylinder1853,Cut406,Cut404,Cut403,Cut405]
  Placement = pos=(0,0,0) rot=(0,0,1;4.18879rad)
FEATURE [Part::FeaturePython] wormgear061  # WARN: FeaturePython — macro-defined, semantics opaque (R4)
  AttacherType = Attacher::AttachEngine3D
  Placement = pos=(0,0,20) rot=(0,0,1;0.881391rad)
  beta = 30.9638
  clearance = 0.25
  diameter = 16
  head = 0.5
  height = 10
  module = 0.8
  pressure_angle = 20
  reverse_pitch = false
  teeth = 12
  version = 0.0.3
FEATURE [Part::Cylinder] Cylinder1917  label="Válec1917"
  Angle = 360
  AttacherType = Attacher::AttachEngine3D
  Height = 10
  Radius = 6
FEATURE [Part::FeaturePython] wormgear062  # WARN: FeaturePython — macro-defined, semantics opaque (R4)
  AttacherType = Attacher::AttachEngine3D
  Placement = pos=(0,0,20) rot=(0,0,1;0.881391rad)
  beta = 30.9638
  clearance = 0.25
  diameter = 16
  head = 0.5
  height = 10
  module = 0.8
  pressure_angle = 20
  reverse_pitch = false
  teeth = 12
  version = 0.0.3
FEATURE [Part::Cylinder] Cylinder1918  label="Válec1918"
  Angle = 360
  AttacherType = Attacher::AttachEngine3D
  Height = 12
  Placement = pos=(0,0,-20) rot=(0,0,1;0rad)
  Radius = 2
FEATURE [Part::Cylinder] Cylinder1919  label="Válec1919"
  Angle = 360
  AttacherType = Attacher::AttachEngine3D
  Height = 6
  Placement = pos=(0,0,-14) rot=(0,0,1;0rad)
  Radius = 2
FEATURE [Part::Box] Box390  label="Krychle390"
  AttacherType = Attacher::AttachEngine3D
  Height = 12
  Length = 16
  Placement = pos=(-5.65685,-5.65685,-20) rot=(0,0,1;0.785398rad)
  Width = 8
FEATURE [Part::Cylinder] Cylinder1920  label="Válec1920"
  Angle = 360
  AttacherType = Attacher::AttachEngine3D
  Height = 20
  Placement = pos=(4,0,-20) rot=(0,0,-1;1.5708rad)
  Radius = 1
FEATURE [Part::Box] Box391  label="Krychle391"
  AttacherType = Attacher::AttachEngine3D
  Height = 12
  Length = 16
  Placement = pos=(5.65685,-5.65685,-20) rot=(0,0,1;2.35619rad)
  Width = 8
FEATURE [Part::Cylinder] Cylinder1921  label="Válec1921"
  Angle = 360
  AttacherType = Attacher::AttachEngine3D
  Height = 12
  Placement = pos=(0,0,-20) rot=(0,0,1;0rad)
  Radius = 6
FEATURE [Part::Cut] Cut430
  Base = -> Cylinder1921
  Tool = -> Cylinder1918
FEATURE [Part::Cut] Cut435
  Base = -> Cut430
  Tool = -> Box391
FEATURE [Part::Cut] Cut432
  Base = -> Cut435
  Tool = -> Box390
FEATURE [Part::Cut] Cut433
  Base = -> Cut432
  Tool = -> Cylinder1920
FEATURE [Part::Cut] Cut434
  Base = -> Cut432
  Placement = pos=(0,0,0) rot=(0,0,1;3.14159rad)
  Tool = -> Cylinder1920
FEATURE [Part::Compound] Compound615  label="G-midi_sun-sym-mixo001"
  Links = -> [Cut433,Cut434,Cylinder1919]
  Placement = pos=(0,0,26) rot=(0,0,1;0rad)
FEATURE [Part::Chamfer] Chamfer012
  Base = -> Compound615
  Edges = 4 edges r=0.75: [Edge8,Edge11,Edge29,Edge32]
FEATURE [Part::Cylinder] Cylinder031  label="Válec031"
  Angle = 360
  AttacherType = Attacher::AttachEngine3D
  Height = 11
  Placement = pos=(0,0,19) rot=(0,0,1;0rad)
  Radius = 2.5
FEATURE [Part::Cylinder] Cylinder1922  label="Válec1922"
  Angle = 360
  AttacherType = Attacher::AttachEngine3D
  Height = 20
  Placement = pos=(4,0,-20) rot=(0,0,-1;1.5708rad)
  Radius = 1
FEATURE [Part::Cylinder] Cylinder1923  label="Válec1923"
  Angle = 360
  AttacherType = Attacher::AttachEngine3D
  Height = 20
  Placement = pos=(-4,0,-20) rot=(0,0,-1;1.5708rad)
  Radius = 1
FEATURE [Part::Compound] Compound614
  Links = -> [Cylinder1922,Cylinder1923]
  Placement = pos=(0,0,24) rot=(0,0,1;0rad)
FEATURE [Part::Cylinder] Cylinder1924  label="Válec1924"
  Angle = 360
  AttacherType = Attacher::AttachEngine3D
  Height = 2
  Placement = pos=(-4,0,-20) rot=(0,0,-1;1.5708rad)
  Radius = 2
FEATURE [Part::Cylinder] Cylinder1925  label="Válec1925"
  Angle = 360
  AttacherType = Attacher::AttachEngine3D
  Height = 2
  Placement = pos=(0,0,18) rot=(0,0,1;0rad)
  Radius = 6
FEATURE [Part::Compound] Compound616
  Links = -> [wormgear062,Cylinder1925]
FEATURE [Part::Cut] Cut431
  Base = -> Compound616
  Tool = -> Cylinder031
FEATURE [Part::Cut] Cut428
  Base = -> Cut431
  Tool = -> Compound614
FEATURE [Part::Cylinder] Cylinder1926  label="Válec1926"
  Angle = 360
  AttacherType = Attacher::AttachEngine3D
  Height = 2
  Placement = pos=(4,0,-20) rot=(0,0,-1;1.5708rad)
  Radius = 2
FEATURE [Part::Compound] Compound617
  Links = -> [Cylinder1926,Cylinder1924]
  Placement = pos=(0,0,26) rot=(0,0,1;0rad)
FEATURE [Part::Cut] Cut429
  Base = -> Chamfer012
  Tool = -> Compound617
FEATURE [Part::Chamfer] Chamfer013
  Base = -> Cut429
  Edges = 1 edges r=0.5: [Edge75]
FEATURE [Part::FeaturePython] wormgear063  # WARN: FeaturePython — macro-defined, semantics opaque (R4)
  AttacherType = Attacher::AttachEngine3D
  Placement = pos=(0,0,20) rot=(0,0,1;0.881391rad)
  beta = 31.9384
  clearance = 0.25
  diameter = 15.4
  head = 0.5
  height = 10
  module = 0.8
  pressure_angle = 20
  reverse_pitch = false
  teeth = 12
  version = 0.0.3
FEATURE [Part::Cylinder] Cylinder1927  label="Válec1927"
  Angle = 360
  AttacherType = Attacher::AttachEngine3D
  Height = 12
  Placement = pos=(0,0,-20) rot=(0,0,1;0rad)
  Radius = 2
FEATURE [Part::Cylinder] Cylinder1928  label="Válec1928"
  Angle = 360
  AttacherType = Attacher::AttachEngine3D
  Height = 6
  Placement = pos=(0,0,-14) rot=(0,0,1;0rad)
  Radius = 2
FEATURE [Part::Box] Box392  label="Krychle392"
  AttacherType = Attacher::AttachEngine3D
  Height = 12
  Length = 16
  Placement = pos=(-5.65685,-5.65685,-20) rot=(0,0,1;0.785398rad)
  Width = 8
FEATURE [Part::Cylinder] Cylinder1929  label="Válec1929"
  Angle = 360
  AttacherType = Attacher::AttachEngine3D
  Height = 20
  Placement = pos=(4,0,-20) rot=(0,0,-1;1.5708rad)
  Radius = 1
FEATURE [Part::Box] Box393  label="Krychle393"
  AttacherType = Attacher::AttachEngine3D
  Height = 12
  Length = 16
  Placement = pos=(5.65685,-5.65685,-20) rot=(0,0,1;2.35619rad)
  Width = 8
FEATURE [Part::Cylinder] Cylinder1930  label="Válec1930"
  Angle = 360
  AttacherType = Attacher::AttachEngine3D
  Height = 12
  Placement = pos=(0,0,-20) rot=(0,0,1;0rad)
  Radius = 6
FEATURE [Part::Cut] Cut438
  Base = -> Cylinder1930
  Tool = -> Cylinder1927
FEATURE [Part::Cut] Cut443
  Base = -> Cut438
  Tool = -> Box393
FEATURE [Part::Cut] Cut440
  Base = -> Cut443
  Tool = -> Box392
FEATURE [Part::Cut] Cut441
  Base = -> Cut440
  Tool = -> Cylinder1929
FEATURE [Part::Cut] Cut442
  Base = -> Cut440
  Placement = pos=(0,0,0) rot=(0,0,1;3.14159rad)
  Tool = -> Cylinder1929
FEATURE [Part::Compound] Compound619  label="G-midi_sun-sym-mixo002"
  Links = -> [Cut441,Cut442,Cylinder1928]
  Placement = pos=(0,0,26) rot=(0,0,1;0rad)
FEATURE [Part::Chamfer] Chamfer014
  Base = -> Compound619
  Edges = 4 edges r=0.75: [Edge8,Edge11,Edge29,Edge32]
FEATURE [Part::Cylinder] Cylinder1931  label="Válec1931"
  Angle = 360
  AttacherType = Attacher::AttachEngine3D
  Height = 11
  Placement = pos=(0,0,19) rot=(0,0,1;0rad)
  Radius = 2.6
FEATURE [Part::Cylinder] Cylinder1932  label="Válec1932"
  Angle = 360
  AttacherType = Attacher::AttachEngine3D
  Height = 20
  Placement = pos=(4,0,-20) rot=(0,0,-1;1.5708rad)
  Radius = 1
FEATURE [Part::Cylinder] Cylinder1933  label="Válec1933"
  Angle = 360
  AttacherType = Attacher::AttachEngine3D
  Height = 20
  Placement = pos=(-4,0,-20) rot=(0,0,-1;1.5708rad)
  Radius = 1
FEATURE [Part::Compound] Compound618
  Links = -> [Cylinder1932,Cylinder1933]
  Placement = pos=(0,0,24) rot=(0,0,1;0rad)
FEATURE [Part::Cylinder] Cylinder1934  label="Válec1934"
  Angle = 360
  AttacherType = Attacher::AttachEngine3D
  Height = 2
  Placement = pos=(-4,0,-20) rot=(0,0,-1;1.5708rad)
  Radius = 2
FEATURE [Part::Cylinder] Cylinder1935  label="Válec1935"
  Angle = 360
  AttacherType = Attacher::AttachEngine3D
  Height = 2
  Placement = pos=(0,0,18) rot=(0,0,1;0rad)
  Radius = 6
FEATURE [Part::Compound] Compound620
  Links = -> [wormgear063,Cylinder1935]
FEATURE [Part::Cut] Cut439
  Base = -> Compound620
  Tool = -> Cylinder1931
FEATURE [Part::Cut] Cut436
  Base = -> Cut439
  Tool = -> Compound618
FEATURE [Part::Cylinder] Cylinder1936  label="Válec1936"
  Angle = 360
  AttacherType = Attacher::AttachEngine3D
  Height = 2
  Placement = pos=(4,0,-20) rot=(0,0,-1;1.5708rad)
  Radius = 2
FEATURE [Part::Compound] Compound621
  Links = -> [Cylinder1936,Cylinder1934]
  Placement = pos=(0,0,26) rot=(0,0,1;0rad)
FEATURE [Part::Cut] Cut437
  Base = -> Chamfer014
  Tool = -> Compound621
FEATURE [Part::Chamfer] Chamfer015
  Base = -> Cut437
  Edges = 1 edges r=0.5: [Edge75]
FEATURE [Part::Compound] Compound622  label="G-midi_inner-gear-part-A"
  Links = -> [Cut436,Chamfer015]
FEATURE [Part::Cylinder] Cylinder751  label="Válec751"
  Angle = 360
  AttacherType = Attacher::AttachEngine3D
  Height = 10
  Placement = pos=(-11,0,-91) rot=(0.57735,0.57735,0.57735;2.0944rad)
  Radius = 1.5
FEATURE [Part::Cylinder] Cylinder1938  label="Válec1938"
  Angle = 360
  AttacherType = Attacher::AttachEngine3D
  Height = 6
  Placement = pos=(0,0,-14) rot=(0,0,1;0rad)
  Radius = 2
FEATURE [Part::Cylinder] Cylinder752  label="Válec752"
  Angle = 360
  AttacherType = Attacher::AttachEngine3D
  Height = 10
  Placement = pos=(-11,0,-97) rot=(0.57735,0.57735,0.57735;2.0944rad)
  Radius = 1.5
FEATURE [Part::Compound] Compound623
  Links = -> [Cylinder751,Cylinder752]
FEATURE [Part::Box] Box394  label="Krychle394"
  AttacherType = Attacher::AttachEngine3D
  Height = 6
  Length = 6
  Placement = pos=(-3.5,-3,-100) rot=(0,0,1;1.5708rad)
  Width = 2
FEATURE [Part::Box] Box314  label="Krychle314"
  AttacherType = Attacher::AttachEngine3D
  Height = 6
  Length = 6
  Placement = pos=(-3.5,-3,-94) rot=(0,0,1;1.5708rad)
  Width = 2
FEATURE [Part::Compound] Compound624
  Links = -> [Box394,Box314]
FEATURE [Part::Cylinder] Cylinder1939  label="Válec1939"
  Angle = 360
  AttacherType = Attacher::AttachEngine3D
  Height = 12
  Placement = pos=(0,0,-20) rot=(0,0,1;0rad)
  Radius = 2
FEATURE [Part::Cylinder] Cylinder1940  label="Válec1940"
  Angle = 360
  AttacherType = Attacher::AttachEngine3D
  Height = 20
  Placement = pos=(4,0,-20) rot=(0,0,-1;1.5708rad)
  Radius = 1
FEATURE [Part::Cylinder] Cylinder1941  label="Válec1941"
  Angle = 360
  AttacherType = Attacher::AttachEngine3D
  Height = 12
  Placement = pos=(0,0,-20) rot=(0,0,1;0rad)
  Radius = 6
FEATURE [Part::Box] Box395  label="Krychle395"
  AttacherType = Attacher::AttachEngine3D
  Height = 12
  Length = 16
  Placement = pos=(5.65685,-5.65685,-20) rot=(0,0,1;2.35619rad)
  Width = 8
FEATURE [Part::Box] Box396  label="Krychle396"
  AttacherType = Attacher::AttachEngine3D
  Height = 12
  Length = 16
  Placement = pos=(-5.65685,-5.65685,-20) rot=(0,0,1;0.785398rad)
  Width = 8
FEATURE [Part::Cylinder] Cylinder1944  label="Válec1944"
  Angle = 360
  AttacherType = Attacher::AttachEngine3D
  Height = 2
  Placement = pos=(4,0,-20) rot=(0,0,-1;1.5708rad)
  Radius = 2
FEATURE [Part::Cylinder] Cylinder1945  label="Válec1945"
  Angle = 360
  AttacherType = Attacher::AttachEngine3D
  Height = 2
  Placement = pos=(-4,0,-20) rot=(0,0,-1;1.5708rad)
  Radius = 2
FEATURE [Part::Compound] Compound626
  Links = -> [Cylinder1944,Cylinder1945]
  Placement = pos=(0,0,26) rot=(0,0,1;0rad)
FEATURE [Part::Cut] Cut448
  Base = -> Cylinder1941
  Tool = -> Cylinder1939
FEATURE [Part::Cut] Cut451
  Base = -> Cut448
  Tool = -> Box395
FEATURE [Part::Cut] Cut449
  Base = -> Cut451
  Tool = -> Box396
FEATURE [Part::Cut] Cut450
  Base = -> Cut449
  Placement = pos=(0,0,0) rot=(0,0,1;3.14159rad)
  Tool = -> Cylinder1940
FEATURE [Part::Cut] Cut452
  Base = -> Cut449
  Tool = -> Cylinder1940
FEATURE [Part::Compound] Compound627  label="G-midi_sun-sym-mixo003"
  Links = -> [Cut452,Cut450,Cylinder1938]
  Placement = pos=(0,0,26) rot=(0,0,1;0rad)
FEATURE [Part::Chamfer] Chamfer016
  Base = -> Compound627
  Edges = 4 edges r=0.75: [Edge8,Edge11,Edge29,Edge32]
FEATURE [Part::Cut] Cut447
  Base = -> Chamfer016
  Tool = -> Compound626
FEATURE [Part::Chamfer] Chamfer017
  Base = -> Cut447
  Edges = 1 edges r=0.5: [Edge75]
  Placement = pos=(0,0,5) rot=(0.707107,0.707107,0;3.14159rad)
FEATURE [Part::FeaturePython] Tube094  # WARN: FeaturePython — macro-defined, semantics opaque (R4)
  AttacherType = Attacher::AttachEngine3D
  Height = 14
  InnerRadius = 4.1
  OuterRadius = 9
  Placement = pos=(0,0,-100) rot=(0,0,1;0rad)
FEATURE [Part::Cut] Cut445
  Base = -> Tube094
  Tool = -> Compound624
FEATURE [Part::Cut] Cut446
  Base = -> Cut445
  Placement = pos=(0,0,37) rot=(0,0,1;0rad)
  Tool = -> Compound623
FEATURE [Part::Cylinder] Cylinder1956  label="Válec1956"
  Angle = 360
  AttacherType = Attacher::AttachEngine3D
  Height = 10
  Radius = 29
FEATURE [Part::Cylinder] Cylinder1957  label="Válec1957"
  Angle = 360
  AttacherType = Attacher::AttachEngine3D
  Height = 15
  Placement = pos=(-18.3848,-18.3848,-20) rot=(0,0,1;2.35619rad)
  Radius = 1.5
FEATURE [Part::Cylinder] Cylinder1958  label="Válec1958"
  Angle = 360
  AttacherType = Attacher::AttachEngine3D
  Height = 15
  Placement = pos=(26,1e-14,-20) rot=(0,0,-1;1.5708rad)
  Radius = 1.5
FEATURE [Part::Cylinder] Cylinder1959  label="Válec1959"
  Angle = 360
  AttacherType = Attacher::AttachEngine3D
  Height = 15
  Placement = pos=(18.3848,-18.3848,-20) rot=(0,0,1;3.92699rad)
  Radius = 1.5
FEATURE [Part::Cylinder] Cylinder1960  label="Válec1960"
  Angle = 360
  AttacherType = Attacher::AttachEngine3D
  Height = 15
  Placement = pos=(-26,-4e-15,-20) rot=(0,0,1;1.5708rad)
  Radius = 1.5
FEATURE [Part::Cylinder] Cylinder1961  label="Válec1961"
  Angle = 360
  AttacherType = Attacher::AttachEngine3D
  Height = 15
  Placement = pos=(1.1e-14,-26,-20) rot=(0,0,1;3.14159rad)
  Radius = 1.5
FEATURE [Part::Cylinder] Cylinder1962  label="Válec1962"
  Angle = 360
  AttacherType = Attacher::AttachEngine3D
  Height = 10
  Radius = 29
FEATURE [Part::Cylinder] Cylinder1963  label="Válec1963"
  Angle = 360
  AttacherType = Attacher::AttachEngine3D
  Height = 15
  Placement = pos=(0,26,-20) rot=(0,0,1;0rad)
  Radius = 1.5
FEATURE [Part::Cylinder] Cylinder1964  label="Válec1964"
  Angle = 360
  AttacherType = Attacher::AttachEngine3D
  Height = 15
  Placement = pos=(-18.3848,18.3848,-20) rot=(0,0,1;0.785398rad)
  Radius = 1.5
FEATURE [Part::Cylinder] Cylinder1965  label="Válec1965"
  Angle = 360
  AttacherType = Attacher::AttachEngine3D
  Height = 15
  Placement = pos=(18.3848,18.3848,-20) rot=(0,0,-1;0.785398rad)
  Radius = 1.5
FEATURE [Part::FeaturePython] wormgear066  # WARN: FeaturePython — macro-defined, semantics opaque (R4)
  AttacherType = Attacher::AttachEngine3D
  Placement = pos=(0,0,0) rot=(0,0,1;1.13796rad)
  beta = 30.9638
  clearance = 0.25
  diameter = 44
  head = 0
  height = 12
  module = 0.8
  pressure_angle = 20
  reverse_pitch = false
  teeth = 33
  version = 0.0.3
FEATURE [Part::FeaturePython] wormgear067  # WARN: FeaturePython — macro-defined, semantics opaque (R4)
  AttacherType = Attacher::AttachEngine3D
  Placement = pos=(0,0,0) rot=(0,0,1;1.13446rad)
  beta = 30.9638
  clearance = 0.25
  diameter = 44
  head = 0
  height = 12
  module = 0.8
  pressure_angle = 20
  reverse_pitch = true
  teeth = 33
  version = 0.0.3
FEATURE [Part::Cut] Cut456
  Base = -> Cylinder1962
  Tool = -> wormgear067
FEATURE [Part::Cut] Cut457
  Base = -> Cylinder1956
  Placement = pos=(0,0,-10) rot=(0,0,1;0rad)
  Tool = -> wormgear066
FEATURE [Part::Compound] Compound631  label="superokruh003"
  Links = -> [Cut457,Cut456]
FEATURE [Part::Compound] Compound632
  Links = -> [Cylinder1963,Cylinder1964,Cylinder1960,Cylinder1957,Cylinder1961,Cylinder1959,Cylinder1958,Cylinder1965]
  Placement = pos=(0,0,5) rot=(0,0,1;0.392699rad)
FEATURE [Part::Cut] Cut458
  Base = -> Compound631
  Tool = -> Compound632
FEATURE [Part::Cylinder] Cylinder1966  label="Válec1966"
  Angle = 360
  AttacherType = Attacher::AttachEngine3D
  Height = 3
  Placement = pos=(32,1.1e-14,4) rot=(0,0,-1;1.5708rad)
  Radius = 3
FEATURE [Part::Cylinder] Cylinder1967  label="Válec1967"
  Angle = 360
  AttacherType = Attacher::AttachEngine3D
  Height = 3
  Placement = pos=(22.6274,22.6274,4) rot=(0,0,-1;0.785398rad)
  Radius = 3
FEATURE [Part::Cylinder] Cylinder1968  label="Válec1968"
  Angle = 360
  AttacherType = Attacher::AttachEngine3D
  Height = 15
  Placement = pos=(-32,0,0) rot=(0,0,1;1.5708rad)
  Radius = 1.5
FEATURE [Part::Cylinder] Cylinder1969  label="Válec1969"
  Angle = 360
  AttacherType = Attacher::AttachEngine3D
  Height = 15
  Placement = pos=(-18.3848,-18.3848,-20) rot=(0,0,1;2.35619rad)
  Radius = 1.5
FEATURE [Part::Cylinder] Cylinder1970  label="Válec1970"
  Angle = 360
  AttacherType = Attacher::AttachEngine3D
  Height = 3
  Placement = pos=(-32,0,4) rot=(0,0,1;1.5708rad)
  Radius = 3
FEATURE [Part::Cylinder] Cylinder1971  label="Válec1971"
  Angle = 360
  AttacherType = Attacher::AttachEngine3D
  Height = 15
  Placement = pos=(32,1.1e-14,0) rot=(0,0,-1;1.5708rad)
  Radius = 1.5
FEATURE [Part::Cylinder] Cylinder1972  label="Válec1972"
  Angle = 360
  AttacherType = Attacher::AttachEngine3D
  Height = 15
  Placement = pos=(22.6274,-22.6274,0) rot=(0,0,1;3.92699rad)
  Radius = 1.5
FEATURE [Part::Cylinder] Cylinder1973  label="Válec1973"
  Angle = 360
  AttacherType = Attacher::AttachEngine3D
  Height = 15
  Placement = pos=(22.6274,22.6274,0) rot=(0,0,-1;0.785398rad)
  Radius = 1.5
FEATURE [Part::Cylinder] Cylinder1974  label="Válec1974"
  Angle = 360
  AttacherType = Attacher::AttachEngine3D
  Height = 3
  Placement = pos=(-22.6274,22.6274,4) rot=(0,0,1;0.785398rad)
  Radius = 3
FEATURE [Part::Cylinder] Cylinder1975  label="Válec1975"
  Angle = 360
  AttacherType = Attacher::AttachEngine3D
  Height = 15
  Placement = pos=(0,32,0) rot=(0,0,1;0rad)
  Radius = 1.5
FEATURE [Part::Cylinder] Cylinder1976  label="Válec1976"
  Angle = 360
  AttacherType = Attacher::AttachEngine3D
  Height = 3
  Placement = pos=(-22.6274,-22.6274,4) rot=(0,0,1;2.35619rad)
  Radius = 3
FEATURE [Part::Cylinder] Cylinder1977  label="Válec1977"
  Angle = 360
  AttacherType = Attacher::AttachEngine3D
  Height = 3
  Placement = pos=(22.6274,-22.6274,4) rot=(0,0,1;3.92699rad)
  Radius = 3
FEATURE [Part::Cylinder] Cylinder1978  label="Válec1978"
  Angle = 360
  AttacherType = Attacher::AttachEngine3D
  Height = 3
  Placement = pos=(1e-14,-32,4) rot=(0,0,1;3.14159rad)
  Radius = 3
FEATURE [Part::Cylinder] Cylinder1979  label="Válec1979"
  Angle = 360
  AttacherType = Attacher::AttachEngine3D
  Height = 15
  Placement = pos=(-22.6274,-22.6274,0) rot=(0,0,1;2.35619rad)
  Radius = 1.5
FEATURE [Part::Cylinder] Cylinder1980  label="Válec1980"
  Angle = 360
  AttacherType = Attacher::AttachEngine3D
  Height = 3
  Placement = pos=(0,32,4) rot=(0,0,1;0rad)
  Radius = 3
FEATURE [Part::Compound] Compound636
  Links = -> [Cylinder1980,Cylinder1974,Cylinder1970,Cylinder1976,Cylinder1978,Cylinder1977,Cylinder1966,Cylinder1967]
FEATURE [Part::Cylinder] Cylinder1981  label="Válec1981"
  Angle = 360
  AttacherType = Attacher::AttachEngine3D
  Height = 15
  Placement = pos=(1e-14,-32,0) rot=(0,0,1;3.14159rad)
  Radius = 1.5
FEATURE [Part::Cylinder] Cylinder1982  label="Válec1982"
  Angle = 360
  AttacherType = Attacher::AttachEngine3D
  Height = 15
  Placement = pos=(-22.6274,22.6274,0) rot=(0,0,1;0.785398rad)
  Radius = 1.5
FEATURE [Part::Compound] Compound634
  Links = -> [Cylinder1975,Cylinder1982,Cylinder1968,Cylinder1979,Cylinder1981,Cylinder1972,Cylinder1971,Cylinder1973]
FEATURE [Part::Box] Box397  label="Krychle397"
  AttacherType = Attacher::AttachEngine3D
  Height = 2
  Length = 6
  Placement = pos=(-18.3848,14.1421,-13) rot=(0,0,1;0.785398rad)
  Width = 6
FEATURE [Part::Box] Box398  label="Krychle398"
  AttacherType = Attacher::AttachEngine3D
  Height = 2
  Length = 6
  Placement = pos=(-14.1421,-18.3848,-13) rot=(0,0,1;2.35619rad)
  Width = 6
FEATURE [Part::Box] Box399  label="Krychle399"
  AttacherType = Attacher::AttachEngine3D
  Height = 2
  Length = 6
  Placement = pos=(18.3848,-14.1421,-13) rot=(0,0,1;3.92699rad)
  Width = 6
FEATURE [Part::Box] Box400  label="Krychle400"
  AttacherType = Attacher::AttachEngine3D
  Height = 2
  Length = 6
  Placement = pos=(3,-23,-13) rot=(0,0,1;3.14159rad)
  Width = 6
FEATURE [Part::Cylinder] Cylinder1983  label="Válec1983"
  Angle = 360
  AttacherType = Attacher::AttachEngine3D
  Height = 15
  Placement = pos=(1.1e-14,-26,-20) rot=(0,0,1;3.14159rad)
  Radius = 1.5
FEATURE [Part::Cylinder] Cylinder1984  label="Válec1984"
  Angle = 360
  AttacherType = Attacher::AttachEngine3D
  Height = 15
  Placement = pos=(0,26,-20) rot=(0,0,1;0rad)
  Radius = 1.5
FEATURE [Part::Cylinder] Cylinder1985  label="Válec1985"
  Angle = 360
  AttacherType = Attacher::AttachEngine3D
  Height = 15
  Placement = pos=(26,1e-14,-20) rot=(0,0,-1;1.5708rad)
  Radius = 1.5
FEATURE [Part::Cylinder] Cylinder1986  label="Válec1986"
  Angle = 360
  AttacherType = Attacher::AttachEngine3D
  Height = 15
  Placement = pos=(-26,-4e-15,-20) rot=(0,0,1;1.5708rad)
  Radius = 1.5
FEATURE [Part::Box] Box401  label="Krychle401"
  AttacherType = Attacher::AttachEngine3D
  Height = 2
  Length = 6
  Placement = pos=(-23,-3,-13) rot=(0,0,1;1.5708rad)
  Width = 6
FEATURE [Part::Box] Box402  label="Krychle402"
  AttacherType = Attacher::AttachEngine3D
  Height = 2
  Length = 6
  Placement = pos=(-3,23,-13) rot=(0,0,1;0rad)
  Width = 6
FEATURE [Part::Box] Box403  label="Krychle403"
  AttacherType = Attacher::AttachEngine3D
  Height = 2
  Length = 6
  Placement = pos=(23,3,-13) rot=(0,0,-1;1.5708rad)
  Width = 6
FEATURE [Part::Cylinder] Cylinder1987  label="Válec1987"
  Angle = 360
  AttacherType = Attacher::AttachEngine3D
  Height = 15
  Placement = pos=(-18.3848,18.3848,-20) rot=(0,0,1;0.785398rad)
  Radius = 1.5
FEATURE [Part::Cylinder] Cylinder1988  label="Válec1988"
  Angle = 360
  AttacherType = Attacher::AttachEngine3D
  Height = 15
  Placement = pos=(18.3848,18.3848,-20) rot=(0,0,-1;0.785398rad)
  Radius = 1.5
FEATURE [Part::Cylinder] Cylinder1989  label="Válec1989"
  Angle = 360
  AttacherType = Attacher::AttachEngine3D
  Height = 15
  Placement = pos=(18.3848,-18.3848,-20) rot=(0,0,1;3.92699rad)
  Radius = 1.5
FEATURE [Part::Compound] Compound635
  Links = -> [Cylinder1984,Cylinder1987,Cylinder1986,Cylinder1969,Cylinder1983,Cylinder1989,Cylinder1985,Cylinder1988]
  Placement = pos=(0,0,0) rot=(0,0,1;0.392699rad)
FEATURE [Part::Box] Box404  label="Krychle404"
  AttacherType = Attacher::AttachEngine3D
  Height = 2
  Length = 6
  Placement = pos=(14.1421,18.3848,-13) rot=(0,0,-1;0.785398rad)
  Width = 6
FEATURE [Part::Compound] Compound633
  Links = -> [Box397,Box401,Box398,Box400,Box399,Box403,Box404,Box402]
  Placement = pos=(0,0,0) rot=(0,0,1;0.392699rad)
FEATURE [Part::FeaturePython] Tube095  # WARN: FeaturePython — macro-defined, semantics opaque (R4)
  AttacherType = Attacher::AttachEngine3D
  Height = 6
  InnerRadius = 29
  OuterRadius = 35
  Placement = pos=(0,0,4) rot=(0,0,1;0rad)
FEATURE [Part::Cut] Cut459
  Base = -> Tube095
  Tool = -> Compound636
FEATURE [Part::Cut] Cut462
  Base = -> Cut459
  Tool = -> Compound634
FEATURE [Part::FeaturePython] Tube096  # WARN: FeaturePython — macro-defined, semantics opaque (R4)
  AttacherType = Attacher::AttachEngine3D
  Height = 6
  InnerRadius = 23
  OuterRadius = 29
  Placement = pos=(0,0,-16) rot=(0,0,1;0rad)
FEATURE [Part::Cut] Cut460
  Base = -> Tube096
  Tool = -> Compound635
FEATURE [Part::Cut] Cut461
  Base = -> Cut460
  Tool = -> Compound633
FEATURE [Part::Compound] Compound637  label="G-midi_monoblock"
  Links = -> [Cut458,Cut461,Cut462]
FEATURE [Mesh::Feature] Mesh015  label="G-midi_inner-gear-part-A (Meshed)"
FEATURE [Part::Cylinder] Cylinder1946  label="Válec1946"
  Angle = 360
  AttacherType = Attacher::AttachEngine3D
  Height = 36
  Placement = pos=(0,0,-43) rot=(0,0,1;0rad)
  Radius = 6
FEATURE [Part::Cylinder] Cylinder1948  label="Válec1948"
  Angle = 360
  AttacherType = Attacher::AttachEngine3D
  Height = 20
  Placement = pos=(4,0,-20) rot=(0,0,-1;1.5708rad)
  Radius = 1
FEATURE [Part::Cylinder] Cylinder1947  label="Válec1947"
  Angle = 360
  AttacherType = Attacher::AttachEngine3D
  Height = 20
  Placement = pos=(-4,0,-20) rot=(0,0,-1;1.5708rad)
  Radius = 1
FEATURE [Part::Compound] Compound629
  Links = -> [Cylinder1948,Cylinder1947]
  Placement = pos=(0,0,1) rot=(0,0,1;1.5708rad)
FEATURE [Part::Cylinder] Cylinder1949  label="Válec1949"
  Angle = 360
  AttacherType = Attacher::AttachEngine3D
  Height = 30
  Placement = pos=(0,0,-65) rot=(0,0,1;0rad)
  Radius = 4.1
FEATURE [Part::Cut] Cut453
  Base = -> Cylinder1946
  Tool = -> Compound629
FEATURE [Part::Cut] Cut463
  Base = -> Cut453
  Placement = pos=(0,0,-6) rot=(0,0,1;0rad)
  Tool = -> Cylinder1949
FEATURE [Part::Compound] Compound625  label="G-midi_inner-gear-part-B"
  Links = -> [Cut446,Chamfer017,Cut463]
  Placement = pos=(0,0,19) rot=(0,0,1;0rad)
FEATURE [Part::FeaturePython] Tube097  # WARN: FeaturePython — macro-defined, semantics opaque (R4)
  AttacherType = Attacher::AttachEngine3D
  Height = 6
  InnerRadius = 19
  OuterRadius = 29
  Placement = pos=(0,0,-22) rot=(0,0,1;0rad)
FEATURE [Part::Cylinder] Cylinder1990  label="Válec1990"
  Angle = 360
  AttacherType = Attacher::AttachEngine3D
  Height = 20
  Placement = pos=(0,26,-24) rot=(0,0,1;0rad)
  Radius = 1.5
FEATURE [Part::Cylinder] Cylinder1991  label="Válec1991"
  Angle = 360
  AttacherType = Attacher::AttachEngine3D
  Height = 20
  Placement = pos=(18.3848,18.3848,-24) rot=(0,0,-1;0.785398rad)
  Radius = 1.5
FEATURE [Part::Cylinder] Cylinder1992  label="Válec1992"
  Angle = 360
  AttacherType = Attacher::AttachEngine3D
  Height = 20
  Placement = pos=(-18.3848,18.3848,-24) rot=(0,0,1;0.785398rad)
  Radius = 1.5
FEATURE [Part::Cylinder] Cylinder1993  label="Válec1993"
  Angle = 360
  AttacherType = Attacher::AttachEngine3D
  Height = 20
  Placement = pos=(-26,-4e-15,-24) rot=(0,0,1;1.5708rad)
  Radius = 1.5
FEATURE [Part::Cylinder] Cylinder1994  label="Válec1994"
  Angle = 360
  AttacherType = Attacher::AttachEngine3D
  Height = 20
  Placement = pos=(18.3848,-18.3848,-24) rot=(0,0,1;3.92699rad)
  Radius = 1.5
FEATURE [Part::Cylinder] Cylinder1995  label="Válec1995"
  Angle = 360
  AttacherType = Attacher::AttachEngine3D
  Height = 20
  Placement = pos=(1.1e-14,-26,-24) rot=(0,0,1;3.14159rad)
  Radius = 1.5
FEATURE [Part::Cylinder] Cylinder1996  label="Válec1996"
  Angle = 360
  AttacherType = Attacher::AttachEngine3D
  Height = 20
  Placement = pos=(-18.3848,-18.3848,-24) rot=(0,0,1;2.35619rad)
  Radius = 1.5
FEATURE [Part::Cylinder] Cylinder1997  label="Válec1997"
  Angle = 360
  AttacherType = Attacher::AttachEngine3D
  Height = 20
  Placement = pos=(26,1e-14,-24) rot=(0,0,-1;1.5708rad)
  Radius = 1.5
FEATURE [Part::Compound] Compound638
  Links = -> [Cylinder1990,Cylinder1992,Cylinder1993,Cylinder1996,Cylinder1995,Cylinder1994,Cylinder1997,Cylinder1991]
  Placement = pos=(0,0,0) rot=(0,0,1;0.392699rad)
FEATURE [Part::Cut] Cut464  label="G-midi_depth-washer"
  Base = -> Tube097
  Placement = pos=(0,0,-15) rot=(0,0,1;0rad)
  Tool = -> Compound638
FEATURE [Mesh::Feature] Mesh018  label="G-midi_depth-washer (Meshed)"
FEATURE [Part::Torus] Torus010  label="Anuloid010"
  Angle1 = -180
  Angle2 = 180
  Angle3 = 360
  AttacherType = Attacher::AttachEngine3D
  Placement = pos=(0,0,20.5) rot=(0,0,1;0rad)
  Radius1 = 28.45
  Radius2 = 2.2
FEATURE [Part::FeaturePython] wormgear068  # WARN: FeaturePython — macro-defined, semantics opaque (R4)
  AttacherType = Attacher::AttachEngine3D
  Placement = pos=(0,0,9) rot=(0,0,1;1.16588rad)
  beta = 29.7449
  clearance = 0.25
  diameter = 42
  head = 0
  height = 12
  module = 0.8
  pressure_angle = 20
  reverse_pitch = false
  teeth = 30
  version = 0.0.3
FEATURE [Part::Cylinder] Cylinder1998  label="Válec1998"
  Angle = 360
  AttacherType = Attacher::AttachEngine3D
  Height = 9
  Placement = pos=(0,0,11) rot=(0,0,1;0rad)
  Radius = 28.5
FEATURE [Part::Cut] Cut465
  Base = -> Cylinder1998
  Tool = -> wormgear068
FEATURE [Part::Cut] Cut466
  Base = -> Cut465
  Tool = -> Torus010
FEATURE [Part::Torus] Torus011  label="Anuloid011"
  Angle1 = -180
  Angle2 = 180
  Angle3 = 360
  AttacherType = Attacher::AttachEngine3D
  Placement = pos=(0,0,20.5) rot=(0,0,1;0rad)
  Radius1 = 28.45
  Radius2 = 2.2
FEATURE [Part::FeaturePython] wormgear070  # WARN: FeaturePython — macro-defined, semantics opaque (R4)
  AttacherType = Attacher::AttachEngine3D
  Placement = pos=(0,0,19) rot=(0,0,1;1.1205rad)
  beta = 29.7449
  clearance = 0.25
  diameter = 42
  head = 0
  height = 12
  module = 0.8
  pressure_angle = 20
  reverse_pitch = true
  teeth = 30
  version = 0.0.3
FEATURE [Part::Box] Box405  label="Krychle405"
  AttacherType = Attacher::AttachEngine3D
  Height = 2
  Length = 6
  Placement = pos=(19.1773,11.1907,25) rot=(0,0,-1;1.1781rad)
  Width = 7
FEATURE [Part::Cylinder] Cylinder2000  label="Válec2000"
  Angle = 360
  AttacherType = Attacher::AttachEngine3D
  Height = 10
  Placement = pos=(-23.5589,-9.75843,25) rot=(0,0,1;1.96349rad)
  Radius = 1.5
FEATURE [Part::Box] Box406  label="Krychle406"
  AttacherType = Attacher::AttachEngine3D
  Height = 2
  Length = 6
  Placement = pos=(21.4734,-5.6474,25) rot=(0,0,-1;1.96349rad)
  Width = 7
FEATURE [Part::Box] Box407  label="Krychle407"
  AttacherType = Attacher::AttachEngine3D
  Height = 2
  Length = 6
  Placement = pos=(5.6474,21.4734,25) rot=(0,0,-1;0.392699rad)
  Width = 7
FEATURE [Part::Box] Box408  label="Krychle408"
  AttacherType = Attacher::AttachEngine3D
  Height = 2
  Length = 6
  Placement = pos=(-19.1773,-11.1907,25) rot=(0,0,1;1.96349rad)
  Width = 7
FEATURE [Part::Cylinder] Cylinder2001  label="Válec2001"
  Angle = 360
  AttacherType = Attacher::AttachEngine3D
  Height = 10
  Placement = pos=(9.75843,23.5589,25) rot=(0,0,-1;0.392699rad)
  Radius = 1.5
FEATURE [Part::Box] Box409  label="Krychle409"
  AttacherType = Attacher::AttachEngine3D
  Height = 2
  Length = 6
  Placement = pos=(-5.6474,-21.4734,25) rot=(0,0,1;2.74889rad)
  Width = 7
FEATURE [Part::Box] Box410  label="Krychle410"
  AttacherType = Attacher::AttachEngine3D
  Height = 2
  Length = 6
  Placement = pos=(-21.4734,5.6474,25) rot=(0,0,1;1.1781rad)
  Width = 7
FEATURE [Part::Cylinder] Cylinder2002  label="Válec2002"
  Angle = 360
  AttacherType = Attacher::AttachEngine3D
  Height = 10
  Placement = pos=(0,0,20) rot=(0,0,1;0rad)
  Radius = 28.5
FEATURE [Part::Cylinder] Cylinder2003  label="Válec2003"
  Angle = 360
  AttacherType = Attacher::AttachEngine3D
  Height = 13
  Placement = pos=(28.4,0,20.5) rot=(0,0,1;0.392699rad)
  Radius = 2.2
FEATURE [Part::Box] Box411  label="Krychle411"
  AttacherType = Attacher::AttachEngine3D
  Height = 2
  Length = 6
  Placement = pos=(-11.1907,19.1773,25) rot=(0,0,1;0.392699rad)
  Width = 7
FEATURE [Part::Cylinder] Cylinder2004  label="Válec2004"
  Angle = 360
  AttacherType = Attacher::AttachEngine3D
  Height = 10
  Placement = pos=(-23.5589,9.75843,25) rot=(0,0,1;1.1781rad)
  Radius = 1.5
FEATURE [Part::Cylinder] Cylinder2005  label="Válec2005"
  Angle = 360
  AttacherType = Attacher::AttachEngine3D
  Height = 10
  Placement = pos=(23.5589,-9.75843,25) rot=(0,0,-1;1.96349rad)
  Radius = 1.5
FEATURE [Part::Cylinder] Cylinder2006  label="Válec2006"
  Angle = 360
  AttacherType = Attacher::AttachEngine3D
  Height = 10
  Placement = pos=(-9.75843,-23.5589,25) rot=(0,0,1;2.74889rad)
  Radius = 1.5
FEATURE [Part::Cylinder] Cylinder2007  label="Válec2007"
  Angle = 360
  AttacherType = Attacher::AttachEngine3D
  Height = 10
  Placement = pos=(9.75843,-23.5589,25) rot=(0,0,1;3.53429rad)
  Radius = 1.5
FEATURE [Part::Cylinder] Cylinder2008  label="Válec2008"
  Angle = 360
  AttacherType = Attacher::AttachEngine3D
  Height = 10
  Placement = pos=(-9.75843,23.5589,25) rot=(0,0,1;0.392699rad)
  Radius = 1.5
FEATURE [Part::Box] Box412  label="Krychle412"
  AttacherType = Attacher::AttachEngine3D
  Height = 2
  Length = 6
  Placement = pos=(11.1907,-19.1773,25) rot=(0,0,1;3.53429rad)
  Width = 7
FEATURE [Part::Compound] Compound640
  Links = -> [Box411,Box410,Box408,Box409,Box412,Box406,Box405,Box407]
FEATURE [Part::Cylinder] Cylinder2009  label="Válec2009"
  Angle = 360
  AttacherType = Attacher::AttachEngine3D
  Height = 10
  Placement = pos=(23.5589,9.75843,25) rot=(0,0,-1;1.1781rad)
  Radius = 1.5
FEATURE [Part::Compound] Compound641
  Links = -> [Cylinder2008,Cylinder2004,Cylinder2000,Cylinder2006,Cylinder2007,Cylinder2005,Cylinder2009,Cylinder2001]
  Placement = pos=(0,0,-2) rot=(0,0,1;0rad)
FEATURE [Part::Cut] Cut472
  Base = -> Cylinder2002
  Tool = -> wormgear070
FEATURE [Part::Cut] Cut468
  Base = -> Cut472
  Tool = -> Torus011
FEATURE [Part::Cut] Cut467
  Base = -> Cut468
  Tool = -> Cylinder2003
FEATURE [Part::Cut] Cut469
  Base = -> Cut467
  Tool = -> Compound640
FEATURE [Part::Cut] Cut471
  Base = -> Cut469
  Tool = -> Compound641
FEATURE [Part::Compound] Compound639  label="G-midi_rybovina001"
  Links = -> [Cut471]
FEATURE [Part::Compound] Compound642  label="G-midi_rybovina-centric"
  Links = -> [Cut466,Compound639]
FEATURE [Mesh::Feature] Mesh023  label="G-midi_rybovina-centric (Meshed)002"
FEATURE [Mesh::Feature] Mesh024  label="G-midi_monoblock (Meshed)001"
FEATURE [Part::Torus] Torus012  label="Anuloid012"
  Angle1 = -180
  Angle2 = 180
  Angle3 = 360
  AttacherType = Attacher::AttachEngine3D
  Placement = pos=(0,0,20.5) rot=(0,0,1;0rad)
  Radius1 = 28.45
  Radius2 = 2.2
FEATURE [Part::Torus] Torus013  label="Anuloid013"
  Angle1 = -180
  Angle2 = 180
  Angle3 = 360
  AttacherType = Attacher::AttachEngine3D
  Placement = pos=(0,0,20.5) rot=(0,0,1;0rad)
  Radius1 = 28.45
  Radius2 = 2.2
FEATURE [Part::FeaturePython] wormgear071  # WARN: FeaturePython — macro-defined, semantics opaque (R4)
  AttacherType = Attacher::AttachEngine3D
  Placement = pos=(0,0,19) rot=(0,0,1;1.1205rad)
  beta = 29.4537
  clearance = 0.25
  diameter = 42.5
  head = 0
  height = 12
  module = 0.8
  pressure_angle = 20
  reverse_pitch = true
  teeth = 30
  version = 0.0.3
FEATURE [Part::FeaturePython] wormgear072  # WARN: FeaturePython — macro-defined, semantics opaque (R4)
  AttacherType = Attacher::AttachEngine3D
  Placement = pos=(0,0,9) rot=(0,0,1;1.16588rad)
  beta = 29.4537
  clearance = 0.25
  diameter = 42.5
  head = 0
  height = 12
  module = 0.8
  pressure_angle = 20
  reverse_pitch = false
  teeth = 30
  version = 0.0.3
FEATURE [Part::Box] Box413  label="Krychle413"
  AttacherType = Attacher::AttachEngine3D
  Height = 2
  Length = 6
  Placement = pos=(-21.4734,5.6474,25) rot=(0,0,1;1.1781rad)
  Width = 7
FEATURE [Part::Box] Box414  label="Krychle414"
  AttacherType = Attacher::AttachEngine3D
  Height = 2
  Length = 6
  Placement = pos=(21.4734,-5.6474,25) rot=(0,0,-1;1.96349rad)
  Width = 7
FEATURE [Part::Box] Box415  label="Krychle415"
  AttacherType = Attacher::AttachEngine3D
  Height = 2
  Length = 6
  Placement = pos=(-5.6474,-21.4734,25) rot=(0,0,1;2.74889rad)
  Width = 7
FEATURE [Part::Box] Box416  label="Krychle416"
  AttacherType = Attacher::AttachEngine3D
  Height = 2
  Length = 6
  Placement = pos=(-19.1773,-11.1907,25) rot=(0,0,1;1.96349rad)
  Width = 7
FEATURE [Part::Cylinder] Cylinder2010  label="Válec2010"
  Angle = 360
  AttacherType = Attacher::AttachEngine3D
  Height = 10
  Placement = pos=(0,0,20) rot=(0,0,1;0rad)
  Radius = 28.5
FEATURE [Part::Cut] Cut479
  Base = -> Cylinder2010
  Tool = -> wormgear071
FEATURE [Part::Cut] Cut476
  Base = -> Cut479
  Tool = -> Torus013
FEATURE [Part::Box] Box417  label="Krychle417"
  AttacherType = Attacher::AttachEngine3D
  Height = 2
  Length = 6
  Placement = pos=(5.6474,21.4734,25) rot=(0,0,-1;0.392699rad)
  Width = 7
FEATURE [Part::Cylinder] Cylinder2011  label="Válec2011"
  Angle = 360
  AttacherType = Attacher::AttachEngine3D
  Height = 10
  Placement = pos=(9.75843,23.5589,25) rot=(0,0,-1;0.392699rad)
  Radius = 1.5
FEATURE [Part::Box] Box418  label="Krychle418"
  AttacherType = Attacher::AttachEngine3D
  Height = 2
  Length = 6
  Placement = pos=(11.1907,-19.1773,25) rot=(0,0,1;3.53429rad)
  Width = 7
FEATURE [Part::Cylinder] Cylinder2012  label="Válec2012"
  Angle = 360
  AttacherType = Attacher::AttachEngine3D
  Height = 10
  Placement = pos=(-23.5589,9.75843,25) rot=(0,0,1;1.1781rad)
  Radius = 1.5
FEATURE [Part::Cylinder] Cylinder2013  label="Válec2013"
  Angle = 360
  AttacherType = Attacher::AttachEngine3D
  Height = 13
  Placement = pos=(28.4,0,20.5) rot=(0,0,1;0.392699rad)
  Radius = 2.2
FEATURE [Part::Cut] Cut474
  Base = -> Cut476
  Tool = -> Cylinder2013
FEATURE [Part::Cylinder] Cylinder2014  label="Válec2014"
  Angle = 360
  AttacherType = Attacher::AttachEngine3D
  Height = 10
  Placement = pos=(9.75843,-23.5589,25) rot=(0,0,1;3.53429rad)
  Radius = 1.5
FEATURE [Part::Cylinder] Cylinder2015  label="Válec2015"
  Angle = 360
  AttacherType = Attacher::AttachEngine3D
  Height = 10
  Placement = pos=(23.5589,9.75843,25) rot=(0,0,-1;1.1781rad)
  Radius = 1.5
FEATURE [Part::Cylinder] Cylinder2016  label="Válec2016"
  Angle = 360
  AttacherType = Attacher::AttachEngine3D
  Height = 10
  Placement = pos=(-9.75843,23.5589,25) rot=(0,0,1;0.392699rad)
  Radius = 1.5
FEATURE [Part::Cylinder] Cylinder2017  label="Válec2017"
  Angle = 360
  AttacherType = Attacher::AttachEngine3D
  Height = 10
  Placement = pos=(-9.75843,-23.5589,25) rot=(0,0,1;2.74889rad)
  Radius = 1.5
FEATURE [Part::Box] Box419  label="Krychle419"
  AttacherType = Attacher::AttachEngine3D
  Height = 2
  Length = 6
  Placement = pos=(19.1773,11.1907,25) rot=(0,0,-1;1.1781rad)
  Width = 7
FEATURE [Part::Cylinder] Cylinder2018  label="Válec2018"
  Angle = 360
  AttacherType = Attacher::AttachEngine3D
  Height = 9
  Placement = pos=(0,0,11) rot=(0,0,1;0rad)
  Radius = 28.5
FEATURE [Part::Cut] Cut478
  Base = -> Cylinder2018
  Tool = -> wormgear072
FEATURE [Part::Cut] Cut473
  Base = -> Cut478
  Tool = -> Torus012
FEATURE [Part::Box] Box420  label="Krychle420"
  AttacherType = Attacher::AttachEngine3D
  Height = 2
  Length = 6
  Placement = pos=(-11.1907,19.1773,25) rot=(0,0,1;0.392699rad)
  Width = 7
FEATURE [Part::Cylinder] Cylinder2019  label="Válec2019"
  Angle = 360
  AttacherType = Attacher::AttachEngine3D
  Height = 10
  Placement = pos=(23.5589,-9.75843,25) rot=(0,0,-1;1.96349rad)
  Radius = 1.5
FEATURE [Part::Cylinder] Cylinder2020  label="Válec2020"
  Angle = 360
  AttacherType = Attacher::AttachEngine3D
  Height = 10
  Placement = pos=(-23.5589,-9.75843,25) rot=(0,0,1;1.96349rad)
  Radius = 1.5
FEATURE [Part::Compound] Compound643
  Links = -> [Cylinder2016,Cylinder2012,Cylinder2020,Cylinder2017,Cylinder2014,Cylinder2019,Cylinder2015,Cylinder2011]
  Placement = pos=(0,0,-2) rot=(0,0,1;0rad)
FEATURE [Part::Compound] Compound646
  Links = -> [Box420,Box413,Box416,Box415,Box418,Box414,Box419,Box417]
FEATURE [Part::Cut] Cut475
  Base = -> Cut474
  Tool = -> Compound646
FEATURE [Part::Cut] Cut477
  Base = -> Cut475
  Tool = -> Compound643
FEATURE [Part::Compound] Compound644  label="G-midi_rybovina002"
  Links = -> [Cut477]
FEATURE [Part::Compound] Compound645  label="G-midi_rybovina-centric-lax"
  Links = -> [Cut473,Compound644]
FEATURE [Mesh::Feature] Mesh025  label="G-midi_rybovina-centric-lax (Meshed)"
FEATURE [Part::Cylinder] Cylinder2021  label="Válec2021"
  Angle = 360
  AttacherType = Attacher::AttachEngine3D
  Height = 12
  Placement = pos=(0,0,-20) rot=(0,0,1;0rad)
  Radius = 6
FEATURE [Part::Cylinder] Cylinder2022  label="Válec2022"
  Angle = 360
  AttacherType = Attacher::AttachEngine3D
  Height = 6
  Placement = pos=(0,0,-14) rot=(0,0,1;0rad)
  Radius = 2
FEATURE [Part::Cylinder] Cylinder2023  label="Válec2023"
  Angle = 360
  AttacherType = Attacher::AttachEngine3D
  Height = 20
  Placement = pos=(-4,0,-20) rot=(0,0,-1;1.5708rad)
  Radius = 1
FEATURE [Part::Cylinder] Cylinder2024  label="Válec2024"
  Angle = 360
  AttacherType = Attacher::AttachEngine3D
  Height = 12
  Placement = pos=(0,0,-20) rot=(0,0,1;0rad)
  Radius = 2
FEATURE [Part::Box] Box421  label="Krychle421"
  AttacherType = Attacher::AttachEngine3D
  Height = 12
  Length = 16
  Placement = pos=(5.65685,-5.65685,-20) rot=(0,0,1;2.35619rad)
  Width = 8
FEATURE [Part::Cylinder] Cylinder2025  label="Válec2025"
  Angle = 360
  AttacherType = Attacher::AttachEngine3D
  Height = 20
  Placement = pos=(4,0,-20) rot=(0,0,-1;1.5708rad)
  Radius = 1
FEATURE [Part::Cylinder] Cylinder2026  label="Válec2026"
  Angle = 360
  AttacherType = Attacher::AttachEngine3D
  Height = 2
  Placement = pos=(-4,0,-20) rot=(0,0,-1;1.5708rad)
  Radius = 2
FEATURE [Part::Cylinder] Cylinder2027  label="Válec2027"
  Angle = 360
  AttacherType = Attacher::AttachEngine3D
  Height = 2
  Placement = pos=(0,0,18) rot=(0,0,1;0rad)
  Radius = 6
FEATURE [Part::Cylinder] Cylinder2028  label="Válec2028"
  Angle = 360
  AttacherType = Attacher::AttachEngine3D
  Height = 11
  Placement = pos=(0,0,19) rot=(0,0,1;0rad)
  Radius = 2.6
FEATURE [Part::Cylinder] Cylinder2029  label="Válec2029"
  Angle = 360
  AttacherType = Attacher::AttachEngine3D
  Height = 20
  Placement = pos=(4,0,-20) rot=(0,0,-1;1.5708rad)
  Radius = 1
FEATURE [Part::Cylinder] Cylinder2030  label="Válec2030"
  Angle = 360
  AttacherType = Attacher::AttachEngine3D
  Height = 2
  Placement = pos=(4,0,-20) rot=(0,0,-1;1.5708rad)
  Radius = 2
FEATURE [Part::Box] Box422  label="Krychle422"
  AttacherType = Attacher::AttachEngine3D
  Height = 12
  Length = 16
  Placement = pos=(-5.65685,-5.65685,-20) rot=(0,0,1;0.785398rad)
  Width = 8
FEATURE [Part::Cut] Cut481
  Base = -> Cylinder2021
  Tool = -> Cylinder2024
FEATURE [Part::FeaturePython] wormgear073  # WARN: FeaturePython — macro-defined, semantics opaque (R4)
  AttacherType = Attacher::AttachEngine3D
  Placement = pos=(0,0,20) rot=(0,0,1;0.881391rad)
  beta = 32.9694
  clearance = 0.25
  diameter = 14.8
  head = 0.5
  height = 10
  module = 0.8
  pressure_angle = 20
  reverse_pitch = false
  teeth = 12
  version = 0.0.3
FEATURE [Part::Compound] Compound647
  Links = -> [wormgear073,Cylinder2027]
FEATURE [Part::Cut] Cut480
  Base = -> Compound647
  Tool = -> Cylinder2028
FEATURE [Part::Compound] Compound650
  Links = -> [Cylinder2025,Cylinder2023]
  Placement = pos=(0,0,24) rot=(0,0,1;0rad)
FEATURE [Part::Cut] Cut483
  Base = -> Cut480
  Tool = -> Compound650
FEATURE [Part::Compound] Compound651
  Links = -> [Cylinder2030,Cylinder2026]
  Placement = pos=(0,0,26) rot=(0,0,1;0rad)
FEATURE [Part::Cut] Cut485
  Base = -> Cut481
  Tool = -> Box421
FEATURE [Part::Cut] Cut487
  Base = -> Cut485
  Tool = -> Box422
FEATURE [Part::Cut] Cut484
  Base = -> Cut487
  Placement = pos=(0,0,0) rot=(0,0,1;3.14159rad)
  Tool = -> Cylinder2029
FEATURE [Part::Cut] Cut486
  Base = -> Cut487
  Tool = -> Cylinder2029
FEATURE [Part::Compound] Compound649  label="G-midi_sun-sym-mixo004"
  Links = -> [Cut486,Cut484,Cylinder2022]
  Placement = pos=(0,0,26) rot=(0,0,1;0rad)
FEATURE [Part::Chamfer] Chamfer018
  Base = -> Compound649
  Edges = 4 edges r=0.75: [Edge8,Edge11,Edge29,Edge32]
FEATURE [Part::Cut] Cut482
  Base = -> Chamfer018
  Tool = -> Compound651
FEATURE [Part::Chamfer] Chamfer019
  Base = -> Cut482
  Edges = 1 edges r=0.5: [Edge75]
FEATURE [Part::Compound] Compound648  label="G-midi_inner-gear-part-A-lax"
  Links = -> [Cut483,Chamfer019]
FEATURE [Mesh::Feature] Mesh026  label="G-midi_inner-gear-part-A-lax (Meshed)"
FEATURE [Part::FeaturePython] Tube098  # WARN: FeaturePython — macro-defined, semantics opaque (R4)
  AttacherType = Attacher::AttachEngine3D
  Height = 14
  InnerRadius = 4.1
  OuterRadius = 9
  Placement = pos=(0,0,-100) rot=(0,0,1;0rad)
FEATURE [Part::Cylinder] Cylinder2031  label="Válec2031"
  Angle = 360
  AttacherType = Attacher::AttachEngine3D
  Height = 12
  Placement = pos=(0,0,-20) rot=(0,0,1;0rad)
  Radius = 6
FEATURE [Part::Box] Box423  label="Krychle423"
  AttacherType = Attacher::AttachEngine3D
  Height = 12
  Length = 16
  Placement = pos=(5.65685,-5.65685,-20) rot=(0,0,1;2.35619rad)
  Width = 8
FEATURE [Part::Cylinder] Cylinder2032  label="Válec2032"
  Angle = 360
  AttacherType = Attacher::AttachEngine3D
  Height = 2
  Placement = pos=(4,0,-20) rot=(0,0,-1;1.5708rad)
  Radius = 2
FEATURE [Part::Cylinder] Cylinder2033  label="Válec2033"
  Angle = 360
  AttacherType = Attacher::AttachEngine3D
  Height = 10
  Placement = pos=(-11,0,-97) rot=(0.57735,0.57735,0.57735;2.0944rad)
  Radius = 1.5
FEATURE [Part::Cylinder] Cylinder2034  label="Válec2034"
  Angle = 360
  AttacherType = Attacher::AttachEngine3D
  Height = 10
  Placement = pos=(-11,0,-91) rot=(0.57735,0.57735,0.57735;2.0944rad)
  Radius = 1.5
FEATURE [Part::Cylinder] Cylinder2035  label="Válec2035"
  Angle = 360
  AttacherType = Attacher::AttachEngine3D
  Height = 6
  Placement = pos=(0,0,-14) rot=(0,0,1;0rad)
  Radius = 2
FEATURE [Part::Box] Box424  label="Krychle424"
  AttacherType = Attacher::AttachEngine3D
  Height = 12
  Length = 16
  Placement = pos=(-5.65685,-5.65685,-20) rot=(0,0,1;0.785398rad)
  Width = 8
FEATURE [Part::Cylinder] Cylinder2036  label="Válec2036"
  Angle = 360
  AttacherType = Attacher::AttachEngine3D
  Height = 20
  Placement = pos=(4,0,-20) rot=(0,0,-1;1.5708rad)
  Radius = 1
FEATURE [Part::Box] Box425  label="Krychle425"
  AttacherType = Attacher::AttachEngine3D
  Height = 6
  Length = 6
  Placement = pos=(-3.5,-3,-94) rot=(0,0,1;1.5708rad)
  Width = 2
FEATURE [Part::Cylinder] Cylinder2037  label="Válec2037"
  Angle = 360
  AttacherType = Attacher::AttachEngine3D
  Height = 2
  Placement = pos=(-4,0,-20) rot=(0,0,-1;1.5708rad)
  Radius = 2
FEATURE [Part::Box] Box426  label="Krychle426"
  AttacherType = Attacher::AttachEngine3D
  Height = 6
  Length = 6
  Placement = pos=(-3.5,-3,-100) rot=(0,0,1;1.5708rad)
  Width = 2
FEATURE [Part::Cylinder] Cylinder2038  label="Válec2038"
  Angle = 360
  AttacherType = Attacher::AttachEngine3D
  Height = 12
  Placement = pos=(0,0,-20) rot=(0,0,1;0rad)
  Radius = 2
FEATURE [Part::Cylinder] Cylinder2039  label="Válec2039"
  Angle = 360
  AttacherType = Attacher::AttachEngine3D
  Height = 50
  Placement = pos=(0,0,-43) rot=(0,0,1;0rad)
  Radius = 6
FEATURE [Part::Cylinder] Cylinder2040  label="Válec2040"
  Angle = 360
  AttacherType = Attacher::AttachEngine3D
  Height = 20
  Placement = pos=(4,0,-20) rot=(0,0,-1;1.5708rad)
  Radius = 1
FEATURE [Part::Cylinder] Cylinder2041  label="Válec2041"
  Angle = 360
  AttacherType = Attacher::AttachEngine3D
  Height = 30
  Placement = pos=(0,0,-65) rot=(0,0,1;0rad)
  Radius = 4.1
FEATURE [Part::Cylinder] Cylinder2042  label="Válec2042"
  Angle = 360
  AttacherType = Attacher::AttachEngine3D
  Height = 20
  Placement = pos=(-4,0,-20) rot=(0,0,-1;1.5708rad)
  Radius = 1
FEATURE [Part::Cut] Cut494
  Base = -> Cylinder2031
  Tool = -> Cylinder2038
FEATURE [Part::Cut] Cut496
  Base = -> Cut494
  Tool = -> Box423
FEATURE [Part::Cut] Cut492
  Base = -> Cut496
  Tool = -> Box424
FEATURE [Part::Cut] Cut489
  Base = -> Cut492
  Tool = -> Cylinder2036
FEATURE [Part::Cut] Cut497
  Base = -> Cut492
  Placement = pos=(0,0,0) rot=(0,0,1;3.14159rad)
  Tool = -> Cylinder2036
FEATURE [Part::Compound] Compound652
  Links = -> [Cylinder2040,Cylinder2042]
  Placement = pos=(0,0,15) rot=(0,0,1;1.5708rad)
FEATURE [Part::Cut] Cut495
  Base = -> Cylinder2039
  Tool = -> Compound652
FEATURE [Part::Cut] Cut488
  Base = -> Cut495
  Placement = pos=(0,0,-6) rot=(0,0,1;0rad)
  Tool = -> Cylinder2041
FEATURE [Part::Compound] Compound653
  Links = -> [Cylinder2034,Cylinder2033]
FEATURE [Part::Compound] Compound654
  Links = -> [Box426,Box425]
FEATURE [Part::Cut] Cut490
  Base = -> Tube098
  Tool = -> Compound654
FEATURE [Part::Cut] Cut493
  Base = -> Cut490
  Placement = pos=(0,0,37) rot=(0,0,1;0rad)
  Tool = -> Compound653
FEATURE [Part::Compound] Compound655  label="G-midi_sun-sym-mixo005"
  Links = -> [Cut489,Cut497,Cylinder2035]
  Placement = pos=(0,0,26) rot=(0,0,1;0rad)
FEATURE [Part::Compound] Compound657
  Links = -> [Cylinder2032,Cylinder2037]
  Placement = pos=(0,0,26) rot=(0,0,1;0rad)
FEATURE [Part::Chamfer] Chamfer021
  Base = -> Compound655
  Edges = 4 edges r=0.75: [Edge8,Edge11,Edge29,Edge32]
FEATURE [Part::Cut] Cut491
  Base = -> Chamfer021
  Tool = -> Compound657
FEATURE [Part::Chamfer] Chamfer020
  Base = -> Cut491
  Edges = 1 edges r=0.5: [Edge75]
  Placement = pos=(0,0,19) rot=(0.707107,0.707107,0;3.14159rad)
FEATURE [Part::Compound] Compound656  label="G-midi_inner-gear-part-B-prolonged"
  Links = -> [Cut493,Chamfer020,Cut488]
  Placement = pos=(0,0,19) rot=(0,0,1;0rad)
FEATURE [Mesh::Feature] Mesh027  label="G-midi_inner-gear-part-B-prolonged (Meshed)"
FEATURE [Mesh::Feature] Mesh028  label="G-midi_inner-gear-part-B (Meshed)"
FEATURE [Mesh::Feature] Mesh029  label="G-midi_bearing-ring (Meshed)"
FEATURE [Mesh::Feature] Mesh030  label="G-midi_rybovina (Meshed)001"
FEATURE [Mesh::Feature] Mesh031  label="G-midi_outer-gear001 (Meshed)002"
FEATURE [Mesh::Feature] Mesh032  label="G-midi_pikovina (Meshed)001"
FEATURE [Mesh::Feature] Mesh033  label="G-midi_motohold (Meshed)"
FEATURE [Mesh::Feature] Mesh034  label="G-midi_quikovina (Meshed)"
FEATURE [Mesh::Feature] Mesh035  label="G-midi_rybovina-centric (Meshed)"
FEATURE [Mesh::Feature] Mesh036  label="G-midi_monoblock (Meshed)002"
FEATURE [Mesh::Feature] Mesh037  label="G-midi_inner-gear-part-A-lax (Meshed)001"
FEATURE [Mesh::Feature] Mesh038  label="G-midi_inner-gear-part-B-prolonged (Meshed)001"
